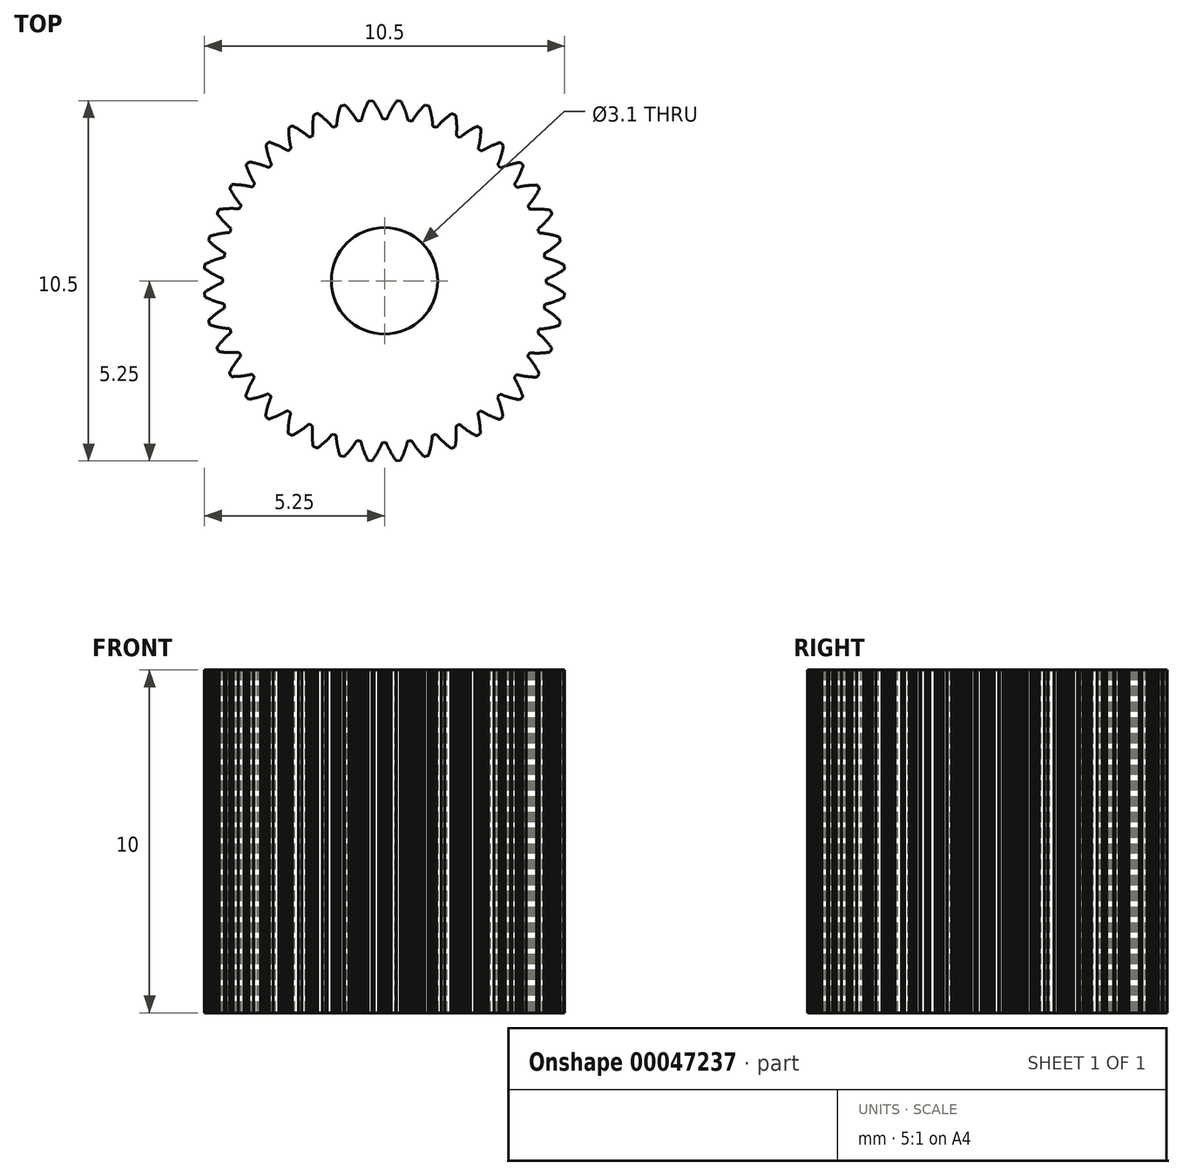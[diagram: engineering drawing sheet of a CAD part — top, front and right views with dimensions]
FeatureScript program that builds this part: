
annotation { "Feature Type Name" : "Feature", "Feature Type Description" : "" }
export const myFeature = defineFeature(function(context is Context, id is Id, definition is map)
    precondition{}
    {
        {
            var Q0;
            Q0=qCreatedBy(makeId("Top.planeOp"),FACE);
            var sketch = newSketch(context, id + "F0", { "sketchPlane" : qUnion([Q0])});
            skLineSegment(sketch, "E0", {"start": v(-0.35, 5.25) * mm, "end": v(-0.46, 5.24) * mm});
            skLineSegment(sketch, "E1", {"start": v(-0.46, 5.24) * mm, "end": v(-0.47, 5.23) * mm});
            skLineSegment(sketch, "E2", {"start": v(-0.47, 5.23) * mm, "end": v(-0.49, 5.2) * mm});
            skLineSegment(sketch, "E3", {"start": v(-0.49, 5.2) * mm, "end": v(-0.5, 5.18) * mm});
            skLineSegment(sketch, "E4", {"start": v(-0.5, 5.18) * mm, "end": v(-0.5, 5.16) * mm});
            skLineSegment(sketch, "E5", {"start": v(-0.5, 5.16) * mm, "end": v(-0.52, 5.14) * mm});
            skLineSegment(sketch, "E6", {"start": v(-0.52, 5.14) * mm, "end": v(-0.52, 5.12) * mm});
            skLineSegment(sketch, "E7", {"start": v(-0.52, 5.12) * mm, "end": v(-0.53, 5.1) * mm});
            skLineSegment(sketch, "E8", {"start": v(-0.53, 5.1) * mm, "end": v(-0.54, 5.08) * mm});
            skLineSegment(sketch, "E9", {"start": v(-0.54, 5.08) * mm, "end": v(-0.55, 5.06) * mm});
            skLineSegment(sketch, "E10", {"start": v(-0.55, 5.06) * mm, "end": v(-0.56, 5.04) * mm});
            skLineSegment(sketch, "E11", {"start": v(-0.56, 5.04) * mm, "end": v(-0.57, 5.02) * mm});
            skLineSegment(sketch, "E12", {"start": v(-0.57, 5.02) * mm, "end": v(-0.57, 5) * mm});
            skLineSegment(sketch, "E13", {"start": v(-0.57, 5) * mm, "end": v(-0.58, 4.98) * mm});
            skLineSegment(sketch, "E14", {"start": v(-0.58, 4.98) * mm, "end": v(-0.59, 4.96) * mm});
            skLineSegment(sketch, "E15", {"start": v(-0.59, 4.96) * mm, "end": v(-0.6, 4.94) * mm});
            skLineSegment(sketch, "E16", {"start": v(-0.6, 4.94) * mm, "end": v(-0.6, 4.93) * mm});
            skLineSegment(sketch, "E17", {"start": v(-0.6, 4.93) * mm, "end": v(-0.6, 4.9) * mm});
            skLineSegment(sketch, "E18", {"start": v(-0.6, 4.9) * mm, "end": v(-0.61, 4.9) * mm});
            skLineSegment(sketch, "E19", {"start": v(-0.61, 4.9) * mm, "end": v(-0.62, 4.87) * mm});
            skLineSegment(sketch, "E20", {"start": v(-0.62, 4.87) * mm, "end": v(-0.62, 4.86) * mm});
            skLineSegment(sketch, "E21", {"start": v(-0.62, 4.86) * mm, "end": v(-0.63, 4.84) * mm});
            skLineSegment(sketch, "E22", {"start": v(-0.63, 4.84) * mm, "end": v(-0.63, 4.82) * mm});
            skLineSegment(sketch, "E23", {"start": v(-0.63, 4.82) * mm, "end": v(-0.64, 4.8) * mm});
            skLineSegment(sketch, "E24", {"start": v(-0.64, 4.8) * mm, "end": v(-0.64, 4.8) * mm});
            skLineSegment(sketch, "E25", {"start": v(-0.64, 4.8) * mm, "end": v(-0.65, 4.78) * mm});
            skLineSegment(sketch, "E26", {"start": v(-0.65, 4.78) * mm, "end": v(-0.65, 4.76) * mm});
            skLineSegment(sketch, "E27", {"start": v(-0.65, 4.76) * mm, "end": v(-0.66, 4.74) * mm});
            skLineSegment(sketch, "E28", {"start": v(-0.66, 4.74) * mm, "end": v(-0.66, 4.73) * mm});
            skLineSegment(sketch, "E29", {"start": v(-0.66, 4.73) * mm, "end": v(-0.66, 4.72) * mm});
            skLineSegment(sketch, "E30", {"start": v(-0.66, 4.72) * mm, "end": v(-0.67, 4.7) * mm});
            skLineSegment(sketch, "E31", {"start": v(-0.67, 4.7) * mm, "end": v(-0.67, 4.69) * mm});
            skLineSegment(sketch, "E32", {"start": v(-0.67, 4.69) * mm, "end": v(-0.67, 4.68) * mm});
            skLineSegment(sketch, "E33", {"start": v(-0.67, 4.68) * mm, "end": v(-0.72, 4.67) * mm});
            skLineSegment(sketch, "E34", {"start": v(-0.72, 4.67) * mm, "end": v(-0.74, 4.66) * mm});
            skLineSegment(sketch, "E35", {"start": v(-0.74, 4.66) * mm, "end": v(-0.8, 4.66) * mm});
            skLineSegment(sketch, "E36", {"start": v(-0.8, 4.66) * mm, "end": v(-0.8, 4.67) * mm});
            skLineSegment(sketch, "E37", {"start": v(-0.8, 4.67) * mm, "end": v(-0.8, 4.68) * mm});
            skLineSegment(sketch, "E38", {"start": v(-0.8, 4.68) * mm, "end": v(-0.81, 4.7) * mm});
            skLineSegment(sketch, "E39", {"start": v(-0.81, 4.7) * mm, "end": v(-0.82, 4.7) * mm});
            skLineSegment(sketch, "E40", {"start": v(-0.82, 4.7) * mm, "end": v(-0.83, 4.72) * mm});
            skLineSegment(sketch, "E41", {"start": v(-0.83, 4.72) * mm, "end": v(-0.84, 4.73) * mm});
            skLineSegment(sketch, "E42", {"start": v(-0.84, 4.73) * mm, "end": v(-0.85, 4.74) * mm});
            skLineSegment(sketch, "E43", {"start": v(-0.85, 4.74) * mm, "end": v(-0.85, 4.76) * mm});
            skLineSegment(sketch, "E44", {"start": v(-0.85, 4.76) * mm, "end": v(-0.86, 4.77) * mm});
            skLineSegment(sketch, "E45", {"start": v(-0.86, 4.77) * mm, "end": v(-0.87, 4.79) * mm});
            skLineSegment(sketch, "E46", {"start": v(-0.87, 4.79) * mm, "end": v(-0.88, 4.8) * mm});
            skLineSegment(sketch, "E47", {"start": v(-0.88, 4.8) * mm, "end": v(-0.9, 4.81) * mm});
            skLineSegment(sketch, "E48", {"start": v(-0.9, 4.81) * mm, "end": v(-0.9, 4.83) * mm});
            skLineSegment(sketch, "E49", {"start": v(-0.9, 4.83) * mm, "end": v(-0.91, 4.84) * mm});
            skLineSegment(sketch, "E50", {"start": v(-0.91, 4.84) * mm, "end": v(-0.92, 4.86) * mm});
            skLineSegment(sketch, "E51", {"start": v(-0.92, 4.86) * mm, "end": v(-0.94, 4.87) * mm});
            skLineSegment(sketch, "E52", {"start": v(-0.94, 4.87) * mm, "end": v(-0.95, 4.89) * mm});
            skLineSegment(sketch, "E53", {"start": v(-0.95, 4.89) * mm, "end": v(-0.96, 4.9) * mm});
            skLineSegment(sketch, "E54", {"start": v(-0.96, 4.9) * mm, "end": v(-0.97, 4.92) * mm});
            skLineSegment(sketch, "E55", {"start": v(-0.97, 4.92) * mm, "end": v(-0.98, 4.94) * mm});
            skLineSegment(sketch, "E56", {"start": v(-0.98, 4.94) * mm, "end": v(-1, 4.95) * mm});
            skLineSegment(sketch, "E57", {"start": v(-1, 4.95) * mm, "end": v(-1.01, 4.97) * mm});
            skLineSegment(sketch, "E58", {"start": v(-1.01, 4.97) * mm, "end": v(-1.02, 4.98) * mm});
            skLineSegment(sketch, "E59", {"start": v(-1.02, 4.98) * mm, "end": v(-1.04, 5) * mm});
            skLineSegment(sketch, "E60", {"start": v(-1.04, 5) * mm, "end": v(-1.05, 5.02) * mm});
            skLineSegment(sketch, "E61", {"start": v(-1.05, 5.02) * mm, "end": v(-1.07, 5.03) * mm});
            skLineSegment(sketch, "E62", {"start": v(-1.07, 5.03) * mm, "end": v(-1.08, 5.05) * mm});
            skLineSegment(sketch, "E63", {"start": v(-1.08, 5.05) * mm, "end": v(-1.1, 5.07) * mm});
            skLineSegment(sketch, "E64", {"start": v(-1.1, 5.07) * mm, "end": v(-1.11, 5.08) * mm});
            skLineSegment(sketch, "E65", {"start": v(-1.11, 5.08) * mm, "end": v(-1.13, 5.1) * mm});
            skLineSegment(sketch, "E66", {"start": v(-1.13, 5.1) * mm, "end": v(-1.15, 5.12) * mm});
            skLineSegment(sketch, "E67", {"start": v(-1.15, 5.12) * mm, "end": v(-1.17, 5.13) * mm});
            skLineSegment(sketch, "E68", {"start": v(-1.17, 5.13) * mm, "end": v(-1.27, 5.1) * mm});
            skLineSegment(sketch, "E69", {"start": v(-1.27, 5.1) * mm, "end": v(-1.29, 5.09) * mm});
            skLineSegment(sketch, "E70", {"start": v(-1.29, 5.09) * mm, "end": v(-1.3, 5.06) * mm});
            skLineSegment(sketch, "E71", {"start": v(-1.3, 5.06) * mm, "end": v(-1.3, 5.04) * mm});
            skLineSegment(sketch, "E72", {"start": v(-1.3, 5.04) * mm, "end": v(-1.3, 5.02) * mm});
            skLineSegment(sketch, "E73", {"start": v(-1.3, 5.02) * mm, "end": v(-1.31, 5) * mm});
            skLineSegment(sketch, "E74", {"start": v(-1.31, 5) * mm, "end": v(-1.32, 4.97) * mm});
            skLineSegment(sketch, "E75", {"start": v(-1.32, 4.97) * mm, "end": v(-1.33, 4.95) * mm});
            skLineSegment(sketch, "E76", {"start": v(-1.33, 4.95) * mm, "end": v(-1.33, 4.93) * mm});
            skLineSegment(sketch, "E77", {"start": v(-1.33, 4.93) * mm, "end": v(-1.34, 4.91) * mm});
            skLineSegment(sketch, "E78", {"start": v(-1.34, 4.91) * mm, "end": v(-1.34, 4.89) * mm});
            skLineSegment(sketch, "E79", {"start": v(-1.34, 4.89) * mm, "end": v(-1.35, 4.87) * mm});
            skLineSegment(sketch, "E80", {"start": v(-1.35, 4.87) * mm, "end": v(-1.35, 4.85) * mm});
            skLineSegment(sketch, "E81", {"start": v(-1.35, 4.85) * mm, "end": v(-1.35, 4.83) * mm});
            skLineSegment(sketch, "E82", {"start": v(-1.35, 4.83) * mm, "end": v(-1.36, 4.8) * mm});
            skLineSegment(sketch, "E83", {"start": v(-1.36, 4.8) * mm, "end": v(-1.36, 4.8) * mm});
            skLineSegment(sketch, "E84", {"start": v(-1.36, 4.8) * mm, "end": v(-1.37, 4.77) * mm});
            skLineSegment(sketch, "E85", {"start": v(-1.37, 4.77) * mm, "end": v(-1.37, 4.75) * mm});
            skLineSegment(sketch, "E86", {"start": v(-1.37, 4.75) * mm, "end": v(-1.37, 4.73) * mm});
            skLineSegment(sketch, "E87", {"start": v(-1.37, 4.73) * mm, "end": v(-1.37, 4.72) * mm});
            skLineSegment(sketch, "E88", {"start": v(-1.37, 4.72) * mm, "end": v(-1.38, 4.7) * mm});
            skLineSegment(sketch, "E89", {"start": v(-1.38, 4.7) * mm, "end": v(-1.38, 4.68) * mm});
            skLineSegment(sketch, "E90", {"start": v(-1.38, 4.68) * mm, "end": v(-1.38, 4.66) * mm});
            skLineSegment(sketch, "E91", {"start": v(-1.38, 4.66) * mm, "end": v(-1.38, 4.65) * mm});
            skLineSegment(sketch, "E92", {"start": v(-1.38, 4.65) * mm, "end": v(-1.39, 4.63) * mm});
            skLineSegment(sketch, "E93", {"start": v(-1.39, 4.63) * mm, "end": v(-1.39, 4.62) * mm});
            skLineSegment(sketch, "E94", {"start": v(-1.39, 4.62) * mm, "end": v(-1.39, 4.6) * mm});
            skLineSegment(sketch, "E95", {"start": v(-1.39, 4.6) * mm, "end": v(-1.4, 4.58) * mm});
            skLineSegment(sketch, "E96", {"start": v(-1.4, 4.58) * mm, "end": v(-1.4, 4.57) * mm});
            skLineSegment(sketch, "E97", {"start": v(-1.4, 4.57) * mm, "end": v(-1.4, 4.55) * mm});
            skLineSegment(sketch, "E98", {"start": v(-1.4, 4.55) * mm, "end": v(-1.4, 4.54) * mm});
            skLineSegment(sketch, "E99", {"start": v(-1.4, 4.54) * mm, "end": v(-1.4, 4.53) * mm});
            skLineSegment(sketch, "E100", {"start": v(-1.4, 4.53) * mm, "end": v(-1.4, 4.52) * mm});
            skLineSegment(sketch, "E101", {"start": v(-1.4, 4.52) * mm, "end": v(-1.45, 4.5) * mm});
            skLineSegment(sketch, "E102", {"start": v(-1.45, 4.5) * mm, "end": v(-1.46, 4.5) * mm});
            skLineSegment(sketch, "E103", {"start": v(-1.46, 4.5) * mm, "end": v(-1.51, 4.48) * mm});
            skLineSegment(sketch, "E104", {"start": v(-1.51, 4.48) * mm, "end": v(-1.52, 4.49) * mm});
            skLineSegment(sketch, "E105", {"start": v(-1.52, 4.49) * mm, "end": v(-1.53, 4.5) * mm});
            skLineSegment(sketch, "E106", {"start": v(-1.53, 4.5) * mm, "end": v(-1.54, 4.5) * mm});
            skLineSegment(sketch, "E107", {"start": v(-1.54, 4.5) * mm, "end": v(-1.55, 4.52) * mm});
            skLineSegment(sketch, "E108", {"start": v(-1.55, 4.52) * mm, "end": v(-1.56, 4.53) * mm});
            skLineSegment(sketch, "E109", {"start": v(-1.56, 4.53) * mm, "end": v(-1.57, 4.54) * mm});
            skLineSegment(sketch, "E110", {"start": v(-1.57, 4.54) * mm, "end": v(-1.58, 4.55) * mm});
            skLineSegment(sketch, "E111", {"start": v(-1.58, 4.55) * mm, "end": v(-1.59, 4.57) * mm});
            skLineSegment(sketch, "E112", {"start": v(-1.59, 4.57) * mm, "end": v(-1.6, 4.58) * mm});
            skLineSegment(sketch, "E113", {"start": v(-1.6, 4.58) * mm, "end": v(-1.61, 4.6) * mm});
            skLineSegment(sketch, "E114", {"start": v(-1.61, 4.6) * mm, "end": v(-1.62, 4.6) * mm});
            skLineSegment(sketch, "E115", {"start": v(-1.62, 4.6) * mm, "end": v(-1.63, 4.62) * mm});
            skLineSegment(sketch, "E116", {"start": v(-1.63, 4.62) * mm, "end": v(-1.65, 4.63) * mm});
            skLineSegment(sketch, "E117", {"start": v(-1.65, 4.63) * mm, "end": v(-1.66, 4.64) * mm});
            skLineSegment(sketch, "E118", {"start": v(-1.66, 4.64) * mm, "end": v(-1.67, 4.65) * mm});
            skLineSegment(sketch, "E119", {"start": v(-1.67, 4.65) * mm, "end": v(-1.69, 4.67) * mm});
            skLineSegment(sketch, "E120", {"start": v(-1.69, 4.67) * mm, "end": v(-1.7, 4.68) * mm});
            skLineSegment(sketch, "E121", {"start": v(-1.7, 4.68) * mm, "end": v(-1.71, 4.7) * mm});
            skLineSegment(sketch, "E122", {"start": v(-1.71, 4.7) * mm, "end": v(-1.73, 4.7) * mm});
            skLineSegment(sketch, "E123", {"start": v(-1.73, 4.7) * mm, "end": v(-1.74, 4.72) * mm});
            skLineSegment(sketch, "E124", {"start": v(-1.74, 4.72) * mm, "end": v(-1.76, 4.74) * mm});
            skLineSegment(sketch, "E125", {"start": v(-1.76, 4.74) * mm, "end": v(-1.78, 4.75) * mm});
            skLineSegment(sketch, "E126", {"start": v(-1.78, 4.75) * mm, "end": v(-1.8, 4.76) * mm});
            skLineSegment(sketch, "E127", {"start": v(-1.8, 4.76) * mm, "end": v(-1.8, 4.78) * mm});
            skLineSegment(sketch, "E128", {"start": v(-1.8, 4.78) * mm, "end": v(-1.82, 4.8) * mm});
            skLineSegment(sketch, "E129", {"start": v(-1.82, 4.8) * mm, "end": v(-1.84, 4.8) * mm});
            skLineSegment(sketch, "E130", {"start": v(-1.84, 4.8) * mm, "end": v(-1.86, 4.82) * mm});
            skLineSegment(sketch, "E131", {"start": v(-1.86, 4.82) * mm, "end": v(-1.88, 4.83) * mm});
            skLineSegment(sketch, "E132", {"start": v(-1.88, 4.83) * mm, "end": v(-1.9, 4.85) * mm});
            skLineSegment(sketch, "E133", {"start": v(-1.9, 4.85) * mm, "end": v(-1.91, 4.86) * mm});
            skLineSegment(sketch, "E134", {"start": v(-1.91, 4.86) * mm, "end": v(-1.94, 4.88) * mm});
            skLineSegment(sketch, "E135", {"start": v(-1.94, 4.88) * mm, "end": v(-1.96, 4.88) * mm});
            skLineSegment(sketch, "E136", {"start": v(-1.96, 4.88) * mm, "end": v(-2.05, 4.84) * mm});
            skLineSegment(sketch, "E137", {"start": v(-2.05, 4.84) * mm, "end": v(-2.07, 4.82) * mm});
            skLineSegment(sketch, "E138", {"start": v(-2.07, 4.82) * mm, "end": v(-2.07, 4.8) * mm});
            skLineSegment(sketch, "E139", {"start": v(-2.07, 4.8) * mm, "end": v(-2.07, 4.78) * mm});
            skLineSegment(sketch, "E140", {"start": v(-2.07, 4.78) * mm, "end": v(-2.08, 4.75) * mm});
            skLineSegment(sketch, "E141", {"start": v(-2.08, 4.75) * mm, "end": v(-2.08, 4.73) * mm});
            skLineSegment(sketch, "E142", {"start": v(-2.08, 4.73) * mm, "end": v(-2.08, 4.7) * mm});
            skLineSegment(sketch, "E143", {"start": v(-2.08, 4.7) * mm, "end": v(-2.08, 4.68) * mm});
            skLineSegment(sketch, "E144", {"start": v(-2.08, 4.68) * mm, "end": v(-2.09, 4.66) * mm});
            skLineSegment(sketch, "E145", {"start": v(-2.09, 4.66) * mm, "end": v(-2.09, 4.64) * mm});
            skLineSegment(sketch, "E146", {"start": v(-2.09, 4.64) * mm, "end": v(-2.09, 4.62) * mm});
            skLineSegment(sketch, "E147", {"start": v(-2.09, 4.62) * mm, "end": v(-2.1, 4.6) * mm});
            skLineSegment(sketch, "E148", {"start": v(-2.1, 4.6) * mm, "end": v(-2.1, 4.58) * mm});
            skLineSegment(sketch, "E149", {"start": v(-2.1, 4.58) * mm, "end": v(-2.1, 4.56) * mm});
            skLineSegment(sketch, "E150", {"start": v(-2.1, 4.56) * mm, "end": v(-2.1, 4.54) * mm});
            skLineSegment(sketch, "E151", {"start": v(-2.1, 4.54) * mm, "end": v(-2.1, 4.52) * mm});
            skLineSegment(sketch, "E152", {"start": v(-2.1, 4.52) * mm, "end": v(-2.1, 4.5) * mm});
            skLineSegment(sketch, "E153", {"start": v(-2.1, 4.5) * mm, "end": v(-2.1, 4.48) * mm});
            skLineSegment(sketch, "E154", {"start": v(-2.1, 4.48) * mm, "end": v(-2.1, 4.46) * mm});
            skLineSegment(sketch, "E155", {"start": v(-2.1, 4.46) * mm, "end": v(-2.1, 4.44) * mm});
            skLineSegment(sketch, "E156", {"start": v(-2.1, 4.44) * mm, "end": v(-2.1, 4.43) * mm});
            skLineSegment(sketch, "E157", {"start": v(-2.1, 4.43) * mm, "end": v(-2.1, 4.4) * mm});
            skLineSegment(sketch, "E158", {"start": v(-2.1, 4.4) * mm, "end": v(-2.1, 4.4) * mm});
            skLineSegment(sketch, "E159", {"start": v(-2.1, 4.4) * mm, "end": v(-2.1, 4.37) * mm});
            skLineSegment(sketch, "E160", {"start": v(-2.1, 4.37) * mm, "end": v(-2.1, 4.36) * mm});
            skLineSegment(sketch, "E161", {"start": v(-2.1, 4.36) * mm, "end": v(-2.1, 4.34) * mm});
            skLineSegment(sketch, "E162", {"start": v(-2.1, 4.34) * mm, "end": v(-2.1, 4.33) * mm});
            skLineSegment(sketch, "E163", {"start": v(-2.1, 4.33) * mm, "end": v(-2.1, 4.31) * mm});
            skLineSegment(sketch, "E164", {"start": v(-2.1, 4.31) * mm, "end": v(-2.09, 4.3) * mm});
            skLineSegment(sketch, "E165", {"start": v(-2.09, 4.3) * mm, "end": v(-2.09, 4.28) * mm});
            skLineSegment(sketch, "E166", {"start": v(-2.09, 4.28) * mm, "end": v(-2.09, 4.27) * mm});
            skLineSegment(sketch, "E167", {"start": v(-2.09, 4.27) * mm, "end": v(-2.08, 4.25) * mm});
            skLineSegment(sketch, "E168", {"start": v(-2.08, 4.25) * mm, "end": v(-2.08, 4.24) * mm});
            skLineSegment(sketch, "E169", {"start": v(-2.08, 4.24) * mm, "end": v(-2.13, 4.21) * mm});
            skLineSegment(sketch, "E170", {"start": v(-2.13, 4.21) * mm, "end": v(-2.14, 4.2) * mm});
            skLineSegment(sketch, "E171", {"start": v(-2.14, 4.2) * mm, "end": v(-2.2, 4.19) * mm});
            skLineSegment(sketch, "E172", {"start": v(-2.2, 4.19) * mm, "end": v(-2.2, 4.2) * mm});
            skLineSegment(sketch, "E173", {"start": v(-2.2, 4.2) * mm, "end": v(-2.21, 4.2) * mm});
            skLineSegment(sketch, "E174", {"start": v(-2.21, 4.2) * mm, "end": v(-2.22, 4.21) * mm});
            skLineSegment(sketch, "E175", {"start": v(-2.22, 4.21) * mm, "end": v(-2.23, 4.22) * mm});
            skLineSegment(sketch, "E176", {"start": v(-2.23, 4.22) * mm, "end": v(-2.25, 4.23) * mm});
            skLineSegment(sketch, "E177", {"start": v(-2.25, 4.23) * mm, "end": v(-2.26, 4.24) * mm});
            skLineSegment(sketch, "E178", {"start": v(-2.26, 4.24) * mm, "end": v(-2.27, 4.25) * mm});
            skLineSegment(sketch, "E179", {"start": v(-2.27, 4.25) * mm, "end": v(-2.28, 4.26) * mm});
            skLineSegment(sketch, "E180", {"start": v(-2.28, 4.26) * mm, "end": v(-2.3, 4.27) * mm});
            skLineSegment(sketch, "E181", {"start": v(-2.3, 4.27) * mm, "end": v(-2.3, 4.28) * mm});
            skLineSegment(sketch, "E182", {"start": v(-2.3, 4.28) * mm, "end": v(-2.32, 4.3) * mm});
            skLineSegment(sketch, "E183", {"start": v(-2.32, 4.3) * mm, "end": v(-2.34, 4.3) * mm});
            skLineSegment(sketch, "E184", {"start": v(-2.34, 4.3) * mm, "end": v(-2.35, 4.31) * mm});
            skLineSegment(sketch, "E185", {"start": v(-2.35, 4.31) * mm, "end": v(-2.37, 4.33) * mm});
            skLineSegment(sketch, "E186", {"start": v(-2.37, 4.33) * mm, "end": v(-2.38, 4.34) * mm});
            skLineSegment(sketch, "E187", {"start": v(-2.38, 4.34) * mm, "end": v(-2.4, 4.35) * mm});
            skLineSegment(sketch, "E188", {"start": v(-2.4, 4.35) * mm, "end": v(-2.41, 4.36) * mm});
            skLineSegment(sketch, "E189", {"start": v(-2.41, 4.36) * mm, "end": v(-2.43, 4.37) * mm});
            skLineSegment(sketch, "E190", {"start": v(-2.43, 4.37) * mm, "end": v(-2.44, 4.38) * mm});
            skLineSegment(sketch, "E191", {"start": v(-2.44, 4.38) * mm, "end": v(-2.46, 4.4) * mm});
            skLineSegment(sketch, "E192", {"start": v(-2.46, 4.4) * mm, "end": v(-2.48, 4.4) * mm});
            skLineSegment(sketch, "E193", {"start": v(-2.48, 4.4) * mm, "end": v(-2.5, 4.41) * mm});
            skLineSegment(sketch, "E194", {"start": v(-2.5, 4.41) * mm, "end": v(-2.51, 4.42) * mm});
            skLineSegment(sketch, "E195", {"start": v(-2.51, 4.42) * mm, "end": v(-2.53, 4.44) * mm});
            skLineSegment(sketch, "E196", {"start": v(-2.53, 4.44) * mm, "end": v(-2.55, 4.45) * mm});
            skLineSegment(sketch, "E197", {"start": v(-2.55, 4.45) * mm, "end": v(-2.57, 4.46) * mm});
            skLineSegment(sketch, "E198", {"start": v(-2.57, 4.46) * mm, "end": v(-2.6, 4.47) * mm});
            skLineSegment(sketch, "E199", {"start": v(-2.6, 4.47) * mm, "end": v(-2.61, 4.48) * mm});
            skLineSegment(sketch, "E200", {"start": v(-2.61, 4.48) * mm, "end": v(-2.63, 4.5) * mm});
            skLineSegment(sketch, "E201", {"start": v(-2.63, 4.5) * mm, "end": v(-2.65, 4.5) * mm});
            skLineSegment(sketch, "E202", {"start": v(-2.65, 4.5) * mm, "end": v(-2.68, 4.52) * mm});
            skLineSegment(sketch, "E203", {"start": v(-2.68, 4.52) * mm, "end": v(-2.7, 4.52) * mm});
            skLineSegment(sketch, "E204", {"start": v(-2.7, 4.52) * mm, "end": v(-2.79, 4.46) * mm});
            skLineSegment(sketch, "E205", {"start": v(-2.79, 4.46) * mm, "end": v(-2.8, 4.44) * mm});
            skLineSegment(sketch, "E206", {"start": v(-2.8, 4.44) * mm, "end": v(-2.8, 4.42) * mm});
            skLineSegment(sketch, "E207", {"start": v(-2.8, 4.42) * mm, "end": v(-2.8, 4.4) * mm});
            skLineSegment(sketch, "E208", {"start": v(-2.8, 4.4) * mm, "end": v(-2.8, 4.37) * mm});
            skLineSegment(sketch, "E209", {"start": v(-2.8, 4.37) * mm, "end": v(-2.8, 4.35) * mm});
            skLineSegment(sketch, "E210", {"start": v(-2.8, 4.35) * mm, "end": v(-2.8, 4.32) * mm});
            skLineSegment(sketch, "E211", {"start": v(-2.8, 4.32) * mm, "end": v(-2.8, 4.3) * mm});
            skLineSegment(sketch, "E212", {"start": v(-2.8, 4.3) * mm, "end": v(-2.79, 4.28) * mm});
            skLineSegment(sketch, "E213", {"start": v(-2.79, 4.28) * mm, "end": v(-2.79, 4.26) * mm});
            skLineSegment(sketch, "E214", {"start": v(-2.79, 4.26) * mm, "end": v(-2.79, 4.24) * mm});
            skLineSegment(sketch, "E215", {"start": v(-2.79, 4.24) * mm, "end": v(-2.78, 4.22) * mm});
            skLineSegment(sketch, "E216", {"start": v(-2.78, 4.22) * mm, "end": v(-2.78, 4.2) * mm});
            skLineSegment(sketch, "E217", {"start": v(-2.78, 4.2) * mm, "end": v(-2.78, 4.17) * mm});
            skLineSegment(sketch, "E218", {"start": v(-2.78, 4.17) * mm, "end": v(-2.78, 4.16) * mm});
            skLineSegment(sketch, "E219", {"start": v(-2.78, 4.16) * mm, "end": v(-2.78, 4.14) * mm});
            skLineSegment(sketch, "E220", {"start": v(-2.78, 4.14) * mm, "end": v(-2.77, 4.12) * mm});
            skLineSegment(sketch, "E221", {"start": v(-2.77, 4.12) * mm, "end": v(-2.77, 4.1) * mm});
            skLineSegment(sketch, "E222", {"start": v(-2.77, 4.1) * mm, "end": v(-2.77, 4.08) * mm});
            skLineSegment(sketch, "E223", {"start": v(-2.77, 4.08) * mm, "end": v(-2.76, 4.06) * mm});
            skLineSegment(sketch, "E224", {"start": v(-2.76, 4.06) * mm, "end": v(-2.76, 4.04) * mm});
            skLineSegment(sketch, "E225", {"start": v(-2.76, 4.04) * mm, "end": v(-2.76, 4.03) * mm});
            skLineSegment(sketch, "E226", {"start": v(-2.76, 4.03) * mm, "end": v(-2.76, 4) * mm});
            skLineSegment(sketch, "E227", {"start": v(-2.76, 4) * mm, "end": v(-2.75, 4) * mm});
            skLineSegment(sketch, "E228", {"start": v(-2.75, 4) * mm, "end": v(-2.75, 3.98) * mm});
            skLineSegment(sketch, "E229", {"start": v(-2.75, 3.98) * mm, "end": v(-2.75, 3.96) * mm});
            skLineSegment(sketch, "E230", {"start": v(-2.75, 3.96) * mm, "end": v(-2.74, 3.95) * mm});
            skLineSegment(sketch, "E231", {"start": v(-2.74, 3.95) * mm, "end": v(-2.74, 3.93) * mm});
            skLineSegment(sketch, "E232", {"start": v(-2.74, 3.93) * mm, "end": v(-2.73, 3.92) * mm});
            skLineSegment(sketch, "E233", {"start": v(-2.73, 3.92) * mm, "end": v(-2.73, 3.9) * mm});
            skLineSegment(sketch, "E234", {"start": v(-2.73, 3.9) * mm, "end": v(-2.73, 3.89) * mm});
            skLineSegment(sketch, "E235", {"start": v(-2.73, 3.89) * mm, "end": v(-2.72, 3.87) * mm});
            skLineSegment(sketch, "E236", {"start": v(-2.72, 3.87) * mm, "end": v(-2.72, 3.87) * mm});
            skLineSegment(sketch, "E237", {"start": v(-2.72, 3.87) * mm, "end": v(-2.76, 3.83) * mm});
            skLineSegment(sketch, "E238", {"start": v(-2.76, 3.83) * mm, "end": v(-2.78, 3.82) * mm});
            skLineSegment(sketch, "E239", {"start": v(-2.78, 3.82) * mm, "end": v(-2.82, 3.8) * mm});
            skLineSegment(sketch, "E240", {"start": v(-2.82, 3.8) * mm, "end": v(-2.83, 3.8) * mm});
            skLineSegment(sketch, "E241", {"start": v(-2.83, 3.8) * mm, "end": v(-2.84, 3.8) * mm});
            skLineSegment(sketch, "E242", {"start": v(-2.84, 3.8) * mm, "end": v(-2.85, 3.81) * mm});
            skLineSegment(sketch, "E243", {"start": v(-2.85, 3.81) * mm, "end": v(-2.87, 3.82) * mm});
            skLineSegment(sketch, "E244", {"start": v(-2.87, 3.82) * mm, "end": v(-2.88, 3.83) * mm});
            skLineSegment(sketch, "E245", {"start": v(-2.88, 3.83) * mm, "end": v(-2.9, 3.84) * mm});
            skLineSegment(sketch, "E246", {"start": v(-2.9, 3.84) * mm, "end": v(-2.9, 3.84) * mm});
            skLineSegment(sketch, "E247", {"start": v(-2.9, 3.84) * mm, "end": v(-2.92, 3.85) * mm});
            skLineSegment(sketch, "E248", {"start": v(-2.92, 3.85) * mm, "end": v(-2.94, 3.86) * mm});
            skLineSegment(sketch, "E249", {"start": v(-2.94, 3.86) * mm, "end": v(-2.95, 3.87) * mm});
            skLineSegment(sketch, "E250", {"start": v(-2.95, 3.87) * mm, "end": v(-2.97, 3.88) * mm});
            skLineSegment(sketch, "E251", {"start": v(-2.97, 3.88) * mm, "end": v(-2.98, 3.89) * mm});
            skLineSegment(sketch, "E252", {"start": v(-2.98, 3.89) * mm, "end": v(-3, 3.9) * mm});
            skLineSegment(sketch, "E253", {"start": v(-3, 3.9) * mm, "end": v(-3.01, 3.9) * mm});
            skLineSegment(sketch, "E254", {"start": v(-3.01, 3.9) * mm, "end": v(-3.03, 3.91) * mm});
            skLineSegment(sketch, "E255", {"start": v(-3.03, 3.91) * mm, "end": v(-3.05, 3.92) * mm});
            skLineSegment(sketch, "E256", {"start": v(-3.05, 3.92) * mm, "end": v(-3.06, 3.93) * mm});
            skLineSegment(sketch, "E257", {"start": v(-3.06, 3.93) * mm, "end": v(-3.08, 3.94) * mm});
            skLineSegment(sketch, "E258", {"start": v(-3.08, 3.94) * mm, "end": v(-3.1, 3.94) * mm});
            skLineSegment(sketch, "E259", {"start": v(-3.1, 3.94) * mm, "end": v(-3.12, 3.95) * mm});
            skLineSegment(sketch, "E260", {"start": v(-3.12, 3.95) * mm, "end": v(-3.14, 3.96) * mm});
            skLineSegment(sketch, "E261", {"start": v(-3.14, 3.96) * mm, "end": v(-3.16, 3.97) * mm});
            skLineSegment(sketch, "E262", {"start": v(-3.16, 3.97) * mm, "end": v(-3.18, 3.98) * mm});
            skLineSegment(sketch, "E263", {"start": v(-3.18, 3.98) * mm, "end": v(-3.2, 3.99) * mm});
            skLineSegment(sketch, "E264", {"start": v(-3.2, 3.99) * mm, "end": v(-3.22, 4) * mm});
            skLineSegment(sketch, "E265", {"start": v(-3.22, 4) * mm, "end": v(-3.24, 4) * mm});
            skLineSegment(sketch, "E266", {"start": v(-3.24, 4) * mm, "end": v(-3.26, 4) * mm});
            skLineSegment(sketch, "E267", {"start": v(-3.26, 4) * mm, "end": v(-3.28, 4.02) * mm});
            skLineSegment(sketch, "E268", {"start": v(-3.28, 4.02) * mm, "end": v(-3.3, 4.03) * mm});
            skLineSegment(sketch, "E269", {"start": v(-3.3, 4.03) * mm, "end": v(-3.32, 4.03) * mm});
            skLineSegment(sketch, "E270", {"start": v(-3.32, 4.03) * mm, "end": v(-3.35, 4.04) * mm});
            skLineSegment(sketch, "E271", {"start": v(-3.35, 4.04) * mm, "end": v(-3.37, 4.04) * mm});
            skLineSegment(sketch, "E272", {"start": v(-3.37, 4.04) * mm, "end": v(-3.45, 3.97) * mm});
            skLineSegment(sketch, "E273", {"start": v(-3.45, 3.97) * mm, "end": v(-3.46, 3.95) * mm});
            skLineSegment(sketch, "E274", {"start": v(-3.46, 3.95) * mm, "end": v(-3.45, 3.92) * mm});
            skLineSegment(sketch, "E275", {"start": v(-3.45, 3.92) * mm, "end": v(-3.45, 3.9) * mm});
            skLineSegment(sketch, "E276", {"start": v(-3.45, 3.9) * mm, "end": v(-3.44, 3.88) * mm});
            skLineSegment(sketch, "E277", {"start": v(-3.44, 3.88) * mm, "end": v(-3.44, 3.86) * mm});
            skLineSegment(sketch, "E278", {"start": v(-3.44, 3.86) * mm, "end": v(-3.43, 3.83) * mm});
            skLineSegment(sketch, "E279", {"start": v(-3.43, 3.83) * mm, "end": v(-3.43, 3.81) * mm});
            skLineSegment(sketch, "E280", {"start": v(-3.43, 3.81) * mm, "end": v(-3.42, 3.8) * mm});
            skLineSegment(sketch, "E281", {"start": v(-3.42, 3.8) * mm, "end": v(-3.42, 3.77) * mm});
            skLineSegment(sketch, "E282", {"start": v(-3.42, 3.77) * mm, "end": v(-3.41, 3.75) * mm});
            skLineSegment(sketch, "E283", {"start": v(-3.41, 3.75) * mm, "end": v(-3.4, 3.73) * mm});
            skLineSegment(sketch, "E284", {"start": v(-3.4, 3.73) * mm, "end": v(-3.4, 3.7) * mm});
            skLineSegment(sketch, "E285", {"start": v(-3.4, 3.7) * mm, "end": v(-3.4, 3.69) * mm});
            skLineSegment(sketch, "E286", {"start": v(-3.4, 3.69) * mm, "end": v(-3.4, 3.67) * mm});
            skLineSegment(sketch, "E287", {"start": v(-3.4, 3.67) * mm, "end": v(-3.39, 3.65) * mm});
            skLineSegment(sketch, "E288", {"start": v(-3.39, 3.65) * mm, "end": v(-3.38, 3.63) * mm});
            skLineSegment(sketch, "E289", {"start": v(-3.38, 3.63) * mm, "end": v(-3.38, 3.61) * mm});
            skLineSegment(sketch, "E290", {"start": v(-3.38, 3.61) * mm, "end": v(-3.37, 3.6) * mm});
            skLineSegment(sketch, "E291", {"start": v(-3.37, 3.6) * mm, "end": v(-3.37, 3.58) * mm});
            skLineSegment(sketch, "E292", {"start": v(-3.37, 3.58) * mm, "end": v(-3.36, 3.56) * mm});
            skLineSegment(sketch, "E293", {"start": v(-3.36, 3.56) * mm, "end": v(-3.35, 3.55) * mm});
            skLineSegment(sketch, "E294", {"start": v(-3.35, 3.55) * mm, "end": v(-3.35, 3.53) * mm});
            skLineSegment(sketch, "E295", {"start": v(-3.35, 3.53) * mm, "end": v(-3.34, 3.51) * mm});
            skLineSegment(sketch, "E296", {"start": v(-3.34, 3.51) * mm, "end": v(-3.34, 3.5) * mm});
            skLineSegment(sketch, "E297", {"start": v(-3.34, 3.5) * mm, "end": v(-3.33, 3.48) * mm});
            skLineSegment(sketch, "E298", {"start": v(-3.33, 3.48) * mm, "end": v(-3.33, 3.47) * mm});
            skLineSegment(sketch, "E299", {"start": v(-3.33, 3.47) * mm, "end": v(-3.32, 3.45) * mm});
            skLineSegment(sketch, "E300", {"start": v(-3.32, 3.45) * mm, "end": v(-3.31, 3.44) * mm});
            skLineSegment(sketch, "E301", {"start": v(-3.31, 3.44) * mm, "end": v(-3.3, 3.43) * mm});
            skLineSegment(sketch, "E302", {"start": v(-3.3, 3.43) * mm, "end": v(-3.3, 3.41) * mm});
            skLineSegment(sketch, "E303", {"start": v(-3.3, 3.41) * mm, "end": v(-3.3, 3.4) * mm});
            skLineSegment(sketch, "E304", {"start": v(-3.3, 3.4) * mm, "end": v(-3.3, 3.4) * mm});
            skLineSegment(sketch, "E305", {"start": v(-3.3, 3.4) * mm, "end": v(-3.33, 3.35) * mm});
            skLineSegment(sketch, "E306", {"start": v(-3.33, 3.35) * mm, "end": v(-3.34, 3.34) * mm});
            skLineSegment(sketch, "E307", {"start": v(-3.34, 3.34) * mm, "end": v(-3.38, 3.3) * mm});
            skLineSegment(sketch, "E308", {"start": v(-3.38, 3.3) * mm, "end": v(-3.39, 3.3) * mm});
            skLineSegment(sketch, "E309", {"start": v(-3.39, 3.3) * mm, "end": v(-3.4, 3.31) * mm});
            skLineSegment(sketch, "E310", {"start": v(-3.4, 3.31) * mm, "end": v(-3.42, 3.32) * mm});
            skLineSegment(sketch, "E311", {"start": v(-3.42, 3.32) * mm, "end": v(-3.43, 3.32) * mm});
            skLineSegment(sketch, "E312", {"start": v(-3.43, 3.32) * mm, "end": v(-3.44, 3.33) * mm});
            skLineSegment(sketch, "E313", {"start": v(-3.44, 3.33) * mm, "end": v(-3.46, 3.34) * mm});
            skLineSegment(sketch, "E314", {"start": v(-3.46, 3.34) * mm, "end": v(-3.47, 3.34) * mm});
            skLineSegment(sketch, "E315", {"start": v(-3.47, 3.34) * mm, "end": v(-3.49, 3.35) * mm});
            skLineSegment(sketch, "E316", {"start": v(-3.49, 3.35) * mm, "end": v(-3.5, 3.35) * mm});
            skLineSegment(sketch, "E317", {"start": v(-3.5, 3.35) * mm, "end": v(-3.52, 3.36) * mm});
            skLineSegment(sketch, "E318", {"start": v(-3.52, 3.36) * mm, "end": v(-3.54, 3.37) * mm});
            skLineSegment(sketch, "E319", {"start": v(-3.54, 3.37) * mm, "end": v(-3.55, 3.37) * mm});
            skLineSegment(sketch, "E320", {"start": v(-3.55, 3.37) * mm, "end": v(-3.57, 3.38) * mm});
            skLineSegment(sketch, "E321", {"start": v(-3.57, 3.38) * mm, "end": v(-3.59, 3.38) * mm});
            skLineSegment(sketch, "E322", {"start": v(-3.59, 3.38) * mm, "end": v(-3.6, 3.39) * mm});
            skLineSegment(sketch, "E323", {"start": v(-3.6, 3.39) * mm, "end": v(-3.62, 3.4) * mm});
            skLineSegment(sketch, "E324", {"start": v(-3.62, 3.4) * mm, "end": v(-3.64, 3.4) * mm});
            skLineSegment(sketch, "E325", {"start": v(-3.64, 3.4) * mm, "end": v(-3.66, 3.4) * mm});
            skLineSegment(sketch, "E326", {"start": v(-3.66, 3.4) * mm, "end": v(-3.68, 3.41) * mm});
            skLineSegment(sketch, "E327", {"start": v(-3.68, 3.41) * mm, "end": v(-3.7, 3.42) * mm});
            skLineSegment(sketch, "E328", {"start": v(-3.7, 3.42) * mm, "end": v(-3.72, 3.42) * mm});
            skLineSegment(sketch, "E329", {"start": v(-3.72, 3.42) * mm, "end": v(-3.74, 3.43) * mm});
            skLineSegment(sketch, "E330", {"start": v(-3.74, 3.43) * mm, "end": v(-3.76, 3.43) * mm});
            skLineSegment(sketch, "E331", {"start": v(-3.76, 3.43) * mm, "end": v(-3.78, 3.44) * mm});
            skLineSegment(sketch, "E332", {"start": v(-3.78, 3.44) * mm, "end": v(-3.8, 3.44) * mm});
            skLineSegment(sketch, "E333", {"start": v(-3.8, 3.44) * mm, "end": v(-3.82, 3.45) * mm});
            skLineSegment(sketch, "E334", {"start": v(-3.82, 3.45) * mm, "end": v(-3.85, 3.45) * mm});
            skLineSegment(sketch, "E335", {"start": v(-3.85, 3.45) * mm, "end": v(-3.87, 3.45) * mm});
            skLineSegment(sketch, "E336", {"start": v(-3.87, 3.45) * mm, "end": v(-3.9, 3.46) * mm});
            skLineSegment(sketch, "E337", {"start": v(-3.9, 3.46) * mm, "end": v(-3.91, 3.46) * mm});
            skLineSegment(sketch, "E338", {"start": v(-3.91, 3.46) * mm, "end": v(-3.94, 3.47) * mm});
            skLineSegment(sketch, "E339", {"start": v(-3.94, 3.47) * mm, "end": v(-3.96, 3.46) * mm});
            skLineSegment(sketch, "E340", {"start": v(-3.96, 3.46) * mm, "end": v(-4.03, 3.38) * mm});
            skLineSegment(sketch, "E341", {"start": v(-4.03, 3.38) * mm, "end": v(-4.03, 3.36) * mm});
            skLineSegment(sketch, "E342", {"start": v(-4.03, 3.36) * mm, "end": v(-4.02, 3.34) * mm});
            skLineSegment(sketch, "E343", {"start": v(-4.02, 3.34) * mm, "end": v(-4.01, 3.31) * mm});
            skLineSegment(sketch, "E344", {"start": v(-4.01, 3.31) * mm, "end": v(-4, 3.3) * mm});
            skLineSegment(sketch, "E345", {"start": v(-4, 3.3) * mm, "end": v(-4, 3.27) * mm});
            skLineSegment(sketch, "E346", {"start": v(-4, 3.27) * mm, "end": v(-4, 3.25) * mm});
            skLineSegment(sketch, "E347", {"start": v(-4, 3.25) * mm, "end": v(-3.98, 3.23) * mm});
            skLineSegment(sketch, "E348", {"start": v(-3.98, 3.23) * mm, "end": v(-3.98, 3.2) * mm});
            skLineSegment(sketch, "E349", {"start": v(-3.98, 3.2) * mm, "end": v(-3.97, 3.19) * mm});
            skLineSegment(sketch, "E350", {"start": v(-3.97, 3.19) * mm, "end": v(-3.96, 3.17) * mm});
            skLineSegment(sketch, "E351", {"start": v(-3.96, 3.17) * mm, "end": v(-3.95, 3.15) * mm});
            skLineSegment(sketch, "E352", {"start": v(-3.95, 3.15) * mm, "end": v(-3.94, 3.13) * mm});
            skLineSegment(sketch, "E353", {"start": v(-3.94, 3.13) * mm, "end": v(-3.93, 3.11) * mm});
            skLineSegment(sketch, "E354", {"start": v(-3.93, 3.11) * mm, "end": v(-3.93, 3.1) * mm});
            skLineSegment(sketch, "E355", {"start": v(-3.93, 3.1) * mm, "end": v(-3.92, 3.08) * mm});
            skLineSegment(sketch, "E356", {"start": v(-3.92, 3.08) * mm, "end": v(-3.9, 3.06) * mm});
            skLineSegment(sketch, "E357", {"start": v(-3.9, 3.06) * mm, "end": v(-3.9, 3.04) * mm});
            skLineSegment(sketch, "E358", {"start": v(-3.9, 3.04) * mm, "end": v(-3.9, 3.02) * mm});
            skLineSegment(sketch, "E359", {"start": v(-3.9, 3.02) * mm, "end": v(-3.88, 3) * mm});
            skLineSegment(sketch, "E360", {"start": v(-3.88, 3) * mm, "end": v(-3.88, 3) * mm});
            skLineSegment(sketch, "E361", {"start": v(-3.88, 3) * mm, "end": v(-3.87, 2.98) * mm});
            skLineSegment(sketch, "E362", {"start": v(-3.87, 2.98) * mm, "end": v(-3.86, 2.96) * mm});
            skLineSegment(sketch, "E363", {"start": v(-3.86, 2.96) * mm, "end": v(-3.85, 2.95) * mm});
            skLineSegment(sketch, "E364", {"start": v(-3.85, 2.95) * mm, "end": v(-3.84, 2.93) * mm});
            skLineSegment(sketch, "E365", {"start": v(-3.84, 2.93) * mm, "end": v(-3.84, 2.92) * mm});
            skLineSegment(sketch, "E366", {"start": v(-3.84, 2.92) * mm, "end": v(-3.83, 2.9) * mm});
            skLineSegment(sketch, "E367", {"start": v(-3.83, 2.9) * mm, "end": v(-3.82, 2.9) * mm});
            skLineSegment(sketch, "E368", {"start": v(-3.82, 2.9) * mm, "end": v(-3.81, 2.88) * mm});
            skLineSegment(sketch, "E369", {"start": v(-3.81, 2.88) * mm, "end": v(-3.8, 2.87) * mm});
            skLineSegment(sketch, "E370", {"start": v(-3.8, 2.87) * mm, "end": v(-3.8, 2.85) * mm});
            skLineSegment(sketch, "E371", {"start": v(-3.8, 2.85) * mm, "end": v(-3.79, 2.84) * mm});
            skLineSegment(sketch, "E372", {"start": v(-3.79, 2.84) * mm, "end": v(-3.78, 2.84) * mm});
            skLineSegment(sketch, "E373", {"start": v(-3.78, 2.84) * mm, "end": v(-3.81, 2.79) * mm});
            skLineSegment(sketch, "E374", {"start": v(-3.81, 2.79) * mm, "end": v(-3.82, 2.78) * mm});
            skLineSegment(sketch, "E375", {"start": v(-3.82, 2.78) * mm, "end": v(-3.86, 2.73) * mm});
            skLineSegment(sketch, "E376", {"start": v(-3.86, 2.73) * mm, "end": v(-3.87, 2.74) * mm});
            skLineSegment(sketch, "E377", {"start": v(-3.87, 2.74) * mm, "end": v(-3.88, 2.74) * mm});
            skLineSegment(sketch, "E378", {"start": v(-3.88, 2.74) * mm, "end": v(-3.9, 2.74) * mm});
            skLineSegment(sketch, "E379", {"start": v(-3.9, 2.74) * mm, "end": v(-3.9, 2.75) * mm});
            skLineSegment(sketch, "E380", {"start": v(-3.9, 2.75) * mm, "end": v(-3.92, 2.75) * mm});
            skLineSegment(sketch, "E381", {"start": v(-3.92, 2.75) * mm, "end": v(-3.94, 2.75) * mm});
            skLineSegment(sketch, "E382", {"start": v(-3.94, 2.75) * mm, "end": v(-3.95, 2.76) * mm});
            skLineSegment(sketch, "E383", {"start": v(-3.95, 2.76) * mm, "end": v(-3.97, 2.76) * mm});
            skLineSegment(sketch, "E384", {"start": v(-3.97, 2.76) * mm, "end": v(-3.98, 2.76) * mm});
            skLineSegment(sketch, "E385", {"start": v(-3.98, 2.76) * mm, "end": v(-4, 2.77) * mm});
            skLineSegment(sketch, "E386", {"start": v(-4, 2.77) * mm, "end": v(-4.02, 2.77) * mm});
            skLineSegment(sketch, "E387", {"start": v(-4.02, 2.77) * mm, "end": v(-4.04, 2.77) * mm});
            skLineSegment(sketch, "E388", {"start": v(-4.04, 2.77) * mm, "end": v(-4.05, 2.78) * mm});
            skLineSegment(sketch, "E389", {"start": v(-4.05, 2.78) * mm, "end": v(-4.07, 2.78) * mm});
            skLineSegment(sketch, "E390", {"start": v(-4.07, 2.78) * mm, "end": v(-4.09, 2.78) * mm});
            skLineSegment(sketch, "E391", {"start": v(-4.09, 2.78) * mm, "end": v(-4.1, 2.79) * mm});
            skLineSegment(sketch, "E392", {"start": v(-4.1, 2.79) * mm, "end": v(-4.13, 2.79) * mm});
            skLineSegment(sketch, "E393", {"start": v(-4.13, 2.79) * mm, "end": v(-4.15, 2.8) * mm});
            skLineSegment(sketch, "E394", {"start": v(-4.15, 2.8) * mm, "end": v(-4.17, 2.8) * mm});
            skLineSegment(sketch, "E395", {"start": v(-4.17, 2.8) * mm, "end": v(-4.19, 2.8) * mm});
            skLineSegment(sketch, "E396", {"start": v(-4.19, 2.8) * mm, "end": v(-4.2, 2.8) * mm});
            skLineSegment(sketch, "E397", {"start": v(-4.2, 2.8) * mm, "end": v(-4.23, 2.8) * mm});
            skLineSegment(sketch, "E398", {"start": v(-4.23, 2.8) * mm, "end": v(-4.25, 2.8) * mm});
            skLineSegment(sketch, "E399", {"start": v(-4.25, 2.8) * mm, "end": v(-4.27, 2.8) * mm});
            skLineSegment(sketch, "E400", {"start": v(-4.27, 2.8) * mm, "end": v(-4.3, 2.8) * mm});
            skLineSegment(sketch, "E401", {"start": v(-4.3, 2.8) * mm, "end": v(-4.31, 2.8) * mm});
            skLineSegment(sketch, "E402", {"start": v(-4.31, 2.8) * mm, "end": v(-4.34, 2.8) * mm});
            skLineSegment(sketch, "E403", {"start": v(-4.34, 2.8) * mm, "end": v(-4.36, 2.8) * mm});
            skLineSegment(sketch, "E404", {"start": v(-4.36, 2.8) * mm, "end": v(-4.38, 2.8) * mm});
            skLineSegment(sketch, "E405", {"start": v(-4.38, 2.8) * mm, "end": v(-4.4, 2.8) * mm});
            skLineSegment(sketch, "E406", {"start": v(-4.4, 2.8) * mm, "end": v(-4.43, 2.8) * mm});
            skLineSegment(sketch, "E407", {"start": v(-4.43, 2.8) * mm, "end": v(-4.45, 2.8) * mm});
            skLineSegment(sketch, "E408", {"start": v(-4.45, 2.8) * mm, "end": v(-4.5, 2.71) * mm});
            skLineSegment(sketch, "E409", {"start": v(-4.5, 2.71) * mm, "end": v(-4.5, 2.69) * mm});
            skLineSegment(sketch, "E410", {"start": v(-4.5, 2.69) * mm, "end": v(-4.5, 2.67) * mm});
            skLineSegment(sketch, "E411", {"start": v(-4.5, 2.67) * mm, "end": v(-4.48, 2.65) * mm});
            skLineSegment(sketch, "E412", {"start": v(-4.48, 2.65) * mm, "end": v(-4.47, 2.62) * mm});
            skLineSegment(sketch, "E413", {"start": v(-4.47, 2.62) * mm, "end": v(-4.46, 2.6) * mm});
            skLineSegment(sketch, "E414", {"start": v(-4.46, 2.6) * mm, "end": v(-4.45, 2.59) * mm});
            skLineSegment(sketch, "E415", {"start": v(-4.45, 2.59) * mm, "end": v(-4.44, 2.57) * mm});
            skLineSegment(sketch, "E416", {"start": v(-4.44, 2.57) * mm, "end": v(-4.43, 2.55) * mm});
            skLineSegment(sketch, "E417", {"start": v(-4.43, 2.55) * mm, "end": v(-4.42, 2.53) * mm});
            skLineSegment(sketch, "E418", {"start": v(-4.42, 2.53) * mm, "end": v(-4.4, 2.51) * mm});
            skLineSegment(sketch, "E419", {"start": v(-4.4, 2.51) * mm, "end": v(-4.4, 2.5) * mm});
            skLineSegment(sketch, "E420", {"start": v(-4.4, 2.5) * mm, "end": v(-4.38, 2.48) * mm});
            skLineSegment(sketch, "E421", {"start": v(-4.38, 2.48) * mm, "end": v(-4.37, 2.46) * mm});
            skLineSegment(sketch, "E422", {"start": v(-4.37, 2.46) * mm, "end": v(-4.36, 2.44) * mm});
            skLineSegment(sketch, "E423", {"start": v(-4.36, 2.44) * mm, "end": v(-4.35, 2.43) * mm});
            skLineSegment(sketch, "E424", {"start": v(-4.35, 2.43) * mm, "end": v(-4.34, 2.4) * mm});
            skLineSegment(sketch, "E425", {"start": v(-4.34, 2.4) * mm, "end": v(-4.33, 2.4) * mm});
            skLineSegment(sketch, "E426", {"start": v(-4.33, 2.4) * mm, "end": v(-4.32, 2.38) * mm});
            skLineSegment(sketch, "E427", {"start": v(-4.32, 2.38) * mm, "end": v(-4.3, 2.36) * mm});
            skLineSegment(sketch, "E428", {"start": v(-4.3, 2.36) * mm, "end": v(-4.3, 2.35) * mm});
            skLineSegment(sketch, "E429", {"start": v(-4.3, 2.35) * mm, "end": v(-4.29, 2.34) * mm});
            skLineSegment(sketch, "E430", {"start": v(-4.29, 2.34) * mm, "end": v(-4.28, 2.32) * mm});
            skLineSegment(sketch, "E431", {"start": v(-4.28, 2.32) * mm, "end": v(-4.27, 2.3) * mm});
            skLineSegment(sketch, "E432", {"start": v(-4.27, 2.3) * mm, "end": v(-4.25, 2.3) * mm});
            skLineSegment(sketch, "E433", {"start": v(-4.25, 2.3) * mm, "end": v(-4.24, 2.28) * mm});
            skLineSegment(sketch, "E434", {"start": v(-4.24, 2.28) * mm, "end": v(-4.23, 2.27) * mm});
            skLineSegment(sketch, "E435", {"start": v(-4.23, 2.27) * mm, "end": v(-4.22, 2.26) * mm});
            skLineSegment(sketch, "E436", {"start": v(-4.22, 2.26) * mm, "end": v(-4.21, 2.25) * mm});
            skLineSegment(sketch, "E437", {"start": v(-4.21, 2.25) * mm, "end": v(-4.2, 2.24) * mm});
            skLineSegment(sketch, "E438", {"start": v(-4.2, 2.24) * mm, "end": v(-4.2, 2.23) * mm});
            skLineSegment(sketch, "E439", {"start": v(-4.2, 2.23) * mm, "end": v(-4.19, 2.22) * mm});
            skLineSegment(sketch, "E440", {"start": v(-4.19, 2.22) * mm, "end": v(-4.18, 2.2) * mm});
            skLineSegment(sketch, "E441", {"start": v(-4.18, 2.2) * mm, "end": v(-4.2, 2.16) * mm});
            skLineSegment(sketch, "E442", {"start": v(-4.2, 2.16) * mm, "end": v(-4.2, 2.14) * mm});
            skLineSegment(sketch, "E443", {"start": v(-4.2, 2.14) * mm, "end": v(-4.24, 2.1) * mm});
            skLineSegment(sketch, "E444", {"start": v(-4.24, 2.1) * mm, "end": v(-4.25, 2.1) * mm});
            skLineSegment(sketch, "E445", {"start": v(-4.25, 2.1) * mm, "end": v(-4.26, 2.1) * mm});
            skLineSegment(sketch, "E446", {"start": v(-4.26, 2.1) * mm, "end": v(-4.27, 2.1) * mm});
            skLineSegment(sketch, "E447", {"start": v(-4.27, 2.1) * mm, "end": v(-4.29, 2.1) * mm});
            skLineSegment(sketch, "E448", {"start": v(-4.29, 2.1) * mm, "end": v(-4.3, 2.1) * mm});
            skLineSegment(sketch, "E449", {"start": v(-4.3, 2.1) * mm, "end": v(-4.32, 2.1) * mm});
            skLineSegment(sketch, "E450", {"start": v(-4.32, 2.1) * mm, "end": v(-4.34, 2.1) * mm});
            skLineSegment(sketch, "E451", {"start": v(-4.34, 2.1) * mm, "end": v(-4.35, 2.1) * mm});
            skLineSegment(sketch, "E452", {"start": v(-4.35, 2.1) * mm, "end": v(-4.37, 2.1) * mm});
            skLineSegment(sketch, "E453", {"start": v(-4.37, 2.1) * mm, "end": v(-4.38, 2.1) * mm});
            skLineSegment(sketch, "E454", {"start": v(-4.38, 2.1) * mm, "end": v(-4.4, 2.1) * mm});
            skLineSegment(sketch, "E455", {"start": v(-4.4, 2.1) * mm, "end": v(-4.42, 2.1) * mm});
            skLineSegment(sketch, "E456", {"start": v(-4.42, 2.1) * mm, "end": v(-4.44, 2.1) * mm});
            skLineSegment(sketch, "E457", {"start": v(-4.44, 2.1) * mm, "end": v(-4.46, 2.1) * mm});
            skLineSegment(sketch, "E458", {"start": v(-4.46, 2.1) * mm, "end": v(-4.47, 2.1) * mm});
            skLineSegment(sketch, "E459", {"start": v(-4.47, 2.1) * mm, "end": v(-4.5, 2.1) * mm});
            skLineSegment(sketch, "E460", {"start": v(-4.5, 2.1) * mm, "end": v(-4.51, 2.1) * mm});
            skLineSegment(sketch, "E461", {"start": v(-4.51, 2.1) * mm, "end": v(-4.53, 2.1) * mm});
            skLineSegment(sketch, "E462", {"start": v(-4.53, 2.1) * mm, "end": v(-4.55, 2.1) * mm});
            skLineSegment(sketch, "E463", {"start": v(-4.55, 2.1) * mm, "end": v(-4.57, 2.1) * mm});
            skLineSegment(sketch, "E464", {"start": v(-4.57, 2.1) * mm, "end": v(-4.6, 2.1) * mm});
            skLineSegment(sketch, "E465", {"start": v(-4.6, 2.1) * mm, "end": v(-4.61, 2.1) * mm});
            skLineSegment(sketch, "E466", {"start": v(-4.61, 2.1) * mm, "end": v(-4.64, 2.1) * mm});
            skLineSegment(sketch, "E467", {"start": v(-4.64, 2.1) * mm, "end": v(-4.66, 2.1) * mm});
            skLineSegment(sketch, "E468", {"start": v(-4.66, 2.1) * mm, "end": v(-4.68, 2.1) * mm});
            skLineSegment(sketch, "E469", {"start": v(-4.68, 2.1) * mm, "end": v(-4.7, 2.1) * mm});
            skLineSegment(sketch, "E470", {"start": v(-4.7, 2.1) * mm, "end": v(-4.72, 2.1) * mm});
            skLineSegment(sketch, "E471", {"start": v(-4.72, 2.1) * mm, "end": v(-4.75, 2.1) * mm});
            skLineSegment(sketch, "E472", {"start": v(-4.75, 2.1) * mm, "end": v(-4.77, 2.09) * mm});
            skLineSegment(sketch, "E473", {"start": v(-4.77, 2.09) * mm, "end": v(-4.8, 2.08) * mm});
            skLineSegment(sketch, "E474", {"start": v(-4.8, 2.08) * mm, "end": v(-4.82, 2.08) * mm});
            skLineSegment(sketch, "E475", {"start": v(-4.82, 2.08) * mm, "end": v(-4.84, 2.07) * mm});
            skLineSegment(sketch, "E476", {"start": v(-4.84, 2.07) * mm, "end": v(-4.88, 1.97) * mm});
            skLineSegment(sketch, "E477", {"start": v(-4.88, 1.97) * mm, "end": v(-4.87, 1.95) * mm});
            skLineSegment(sketch, "E478", {"start": v(-4.87, 1.95) * mm, "end": v(-4.86, 1.93) * mm});
            skLineSegment(sketch, "E479", {"start": v(-4.86, 1.93) * mm, "end": v(-4.84, 1.91) * mm});
            skLineSegment(sketch, "E480", {"start": v(-4.84, 1.91) * mm, "end": v(-4.83, 1.9) * mm});
            skLineSegment(sketch, "E481", {"start": v(-4.83, 1.9) * mm, "end": v(-4.81, 1.87) * mm});
            skLineSegment(sketch, "E482", {"start": v(-4.81, 1.87) * mm, "end": v(-4.8, 1.86) * mm});
            skLineSegment(sketch, "E483", {"start": v(-4.8, 1.86) * mm, "end": v(-4.79, 1.84) * mm});
            skLineSegment(sketch, "E484", {"start": v(-4.79, 1.84) * mm, "end": v(-4.77, 1.82) * mm});
            skLineSegment(sketch, "E485", {"start": v(-4.77, 1.82) * mm, "end": v(-4.76, 1.8) * mm});
            skLineSegment(sketch, "E486", {"start": v(-4.76, 1.8) * mm, "end": v(-4.74, 1.8) * mm});
            skLineSegment(sketch, "E487", {"start": v(-4.74, 1.8) * mm, "end": v(-4.73, 1.77) * mm});
            skLineSegment(sketch, "E488", {"start": v(-4.73, 1.77) * mm, "end": v(-4.72, 1.76) * mm});
            skLineSegment(sketch, "E489", {"start": v(-4.72, 1.76) * mm, "end": v(-4.7, 1.74) * mm});
            skLineSegment(sketch, "E490", {"start": v(-4.7, 1.74) * mm, "end": v(-4.69, 1.73) * mm});
            skLineSegment(sketch, "E491", {"start": v(-4.69, 1.73) * mm, "end": v(-4.68, 1.71) * mm});
            skLineSegment(sketch, "E492", {"start": v(-4.68, 1.71) * mm, "end": v(-4.66, 1.7) * mm});
            skLineSegment(sketch, "E493", {"start": v(-4.66, 1.7) * mm, "end": v(-4.65, 1.69) * mm});
            skLineSegment(sketch, "E494", {"start": v(-4.65, 1.69) * mm, "end": v(-4.64, 1.67) * mm});
            skLineSegment(sketch, "E495", {"start": v(-4.64, 1.67) * mm, "end": v(-4.62, 1.66) * mm});
            skLineSegment(sketch, "E496", {"start": v(-4.62, 1.66) * mm, "end": v(-4.61, 1.65) * mm});
            skLineSegment(sketch, "E497", {"start": v(-4.61, 1.65) * mm, "end": v(-4.6, 1.64) * mm});
            skLineSegment(sketch, "E498", {"start": v(-4.6, 1.64) * mm, "end": v(-4.59, 1.62) * mm});
            skLineSegment(sketch, "E499", {"start": v(-4.59, 1.62) * mm, "end": v(-4.57, 1.61) * mm});
            skLineSegment(sketch, "E500", {"start": v(-4.57, 1.61) * mm, "end": v(-4.56, 1.6) * mm});
            skLineSegment(sketch, "E501", {"start": v(-4.56, 1.6) * mm, "end": v(-4.55, 1.6) * mm});
            skLineSegment(sketch, "E502", {"start": v(-4.55, 1.6) * mm, "end": v(-4.54, 1.58) * mm});
            skLineSegment(sketch, "E503", {"start": v(-4.54, 1.58) * mm, "end": v(-4.53, 1.57) * mm});
            skLineSegment(sketch, "E504", {"start": v(-4.53, 1.57) * mm, "end": v(-4.51, 1.56) * mm});
            skLineSegment(sketch, "E505", {"start": v(-4.51, 1.56) * mm, "end": v(-4.5, 1.55) * mm});
            skLineSegment(sketch, "E506", {"start": v(-4.5, 1.55) * mm, "end": v(-4.5, 1.54) * mm});
            skLineSegment(sketch, "E507", {"start": v(-4.5, 1.54) * mm, "end": v(-4.48, 1.53) * mm});
            skLineSegment(sketch, "E508", {"start": v(-4.48, 1.53) * mm, "end": v(-4.47, 1.53) * mm});
            skLineSegment(sketch, "E509", {"start": v(-4.47, 1.53) * mm, "end": v(-4.49, 1.47) * mm});
            skLineSegment(sketch, "E510", {"start": v(-4.49, 1.47) * mm, "end": v(-4.5, 1.46) * mm});
            skLineSegment(sketch, "E511", {"start": v(-4.5, 1.46) * mm, "end": v(-4.51, 1.4) * mm});
            skLineSegment(sketch, "E512", {"start": v(-4.51, 1.4) * mm, "end": v(-4.52, 1.4) * mm});
            skLineSegment(sketch, "E513", {"start": v(-4.52, 1.4) * mm, "end": v(-4.54, 1.4) * mm});
            skLineSegment(sketch, "E514", {"start": v(-4.54, 1.4) * mm, "end": v(-4.55, 1.4) * mm});
            skLineSegment(sketch, "E515", {"start": v(-4.55, 1.4) * mm, "end": v(-4.57, 1.4) * mm});
            skLineSegment(sketch, "E516", {"start": v(-4.57, 1.4) * mm, "end": v(-4.58, 1.4) * mm});
            skLineSegment(sketch, "E517", {"start": v(-4.58, 1.4) * mm, "end": v(-4.6, 1.4) * mm});
            skLineSegment(sketch, "E518", {"start": v(-4.6, 1.4) * mm, "end": v(-4.61, 1.4) * mm});
            skLineSegment(sketch, "E519", {"start": v(-4.61, 1.4) * mm, "end": v(-4.63, 1.4) * mm});
            skLineSegment(sketch, "E520", {"start": v(-4.63, 1.4) * mm, "end": v(-4.64, 1.4) * mm});
            skLineSegment(sketch, "E521", {"start": v(-4.64, 1.4) * mm, "end": v(-4.66, 1.4) * mm});
            skLineSegment(sketch, "E522", {"start": v(-4.66, 1.4) * mm, "end": v(-4.68, 1.4) * mm});
            skLineSegment(sketch, "E523", {"start": v(-4.68, 1.4) * mm, "end": v(-4.7, 1.4) * mm});
            skLineSegment(sketch, "E524", {"start": v(-4.7, 1.4) * mm, "end": v(-4.71, 1.39) * mm});
            skLineSegment(sketch, "E525", {"start": v(-4.71, 1.39) * mm, "end": v(-4.73, 1.39) * mm});
            skLineSegment(sketch, "E526", {"start": v(-4.73, 1.39) * mm, "end": v(-4.75, 1.38) * mm});
            skLineSegment(sketch, "E527", {"start": v(-4.75, 1.38) * mm, "end": v(-4.77, 1.38) * mm});
            skLineSegment(sketch, "E528", {"start": v(-4.77, 1.38) * mm, "end": v(-4.79, 1.38) * mm});
            skLineSegment(sketch, "E529", {"start": v(-4.79, 1.38) * mm, "end": v(-4.8, 1.37) * mm});
            skLineSegment(sketch, "E530", {"start": v(-4.8, 1.37) * mm, "end": v(-4.83, 1.37) * mm});
            skLineSegment(sketch, "E531", {"start": v(-4.83, 1.37) * mm, "end": v(-4.85, 1.37) * mm});
            skLineSegment(sketch, "E532", {"start": v(-4.85, 1.37) * mm, "end": v(-4.87, 1.36) * mm});
            skLineSegment(sketch, "E533", {"start": v(-4.87, 1.36) * mm, "end": v(-4.89, 1.36) * mm});
            skLineSegment(sketch, "E534", {"start": v(-4.89, 1.36) * mm, "end": v(-4.9, 1.35) * mm});
            skLineSegment(sketch, "E535", {"start": v(-4.9, 1.35) * mm, "end": v(-4.93, 1.35) * mm});
            skLineSegment(sketch, "E536", {"start": v(-4.93, 1.35) * mm, "end": v(-4.95, 1.34) * mm});
            skLineSegment(sketch, "E537", {"start": v(-4.95, 1.34) * mm, "end": v(-4.97, 1.34) * mm});
            skLineSegment(sketch, "E538", {"start": v(-4.97, 1.34) * mm, "end": v(-5, 1.33) * mm});
            skLineSegment(sketch, "E539", {"start": v(-5, 1.33) * mm, "end": v(-5.01, 1.32) * mm});
            skLineSegment(sketch, "E540", {"start": v(-5.01, 1.32) * mm, "end": v(-5.04, 1.32) * mm});
            skLineSegment(sketch, "E541", {"start": v(-5.04, 1.32) * mm, "end": v(-5.06, 1.3) * mm});
            skLineSegment(sketch, "E542", {"start": v(-5.06, 1.3) * mm, "end": v(-5.08, 1.3) * mm});
            skLineSegment(sketch, "E543", {"start": v(-5.08, 1.3) * mm, "end": v(-5.1, 1.29) * mm});
            skLineSegment(sketch, "E544", {"start": v(-5.1, 1.29) * mm, "end": v(-5.13, 1.18) * mm});
            skLineSegment(sketch, "E545", {"start": v(-5.13, 1.18) * mm, "end": v(-5.12, 1.17) * mm});
            skLineSegment(sketch, "E546", {"start": v(-5.12, 1.17) * mm, "end": v(-5.1, 1.15) * mm});
            skLineSegment(sketch, "E547", {"start": v(-5.1, 1.15) * mm, "end": v(-5.08, 1.13) * mm});
            skLineSegment(sketch, "E548", {"start": v(-5.08, 1.13) * mm, "end": v(-5.07, 1.11) * mm});
            skLineSegment(sketch, "E549", {"start": v(-5.07, 1.11) * mm, "end": v(-5.05, 1.1) * mm});
            skLineSegment(sketch, "E550", {"start": v(-5.05, 1.1) * mm, "end": v(-5.03, 1.08) * mm});
            skLineSegment(sketch, "E551", {"start": v(-5.03, 1.08) * mm, "end": v(-5.01, 1.07) * mm});
            skLineSegment(sketch, "E552", {"start": v(-5.01, 1.07) * mm, "end": v(-5, 1.05) * mm});
            skLineSegment(sketch, "E553", {"start": v(-5, 1.05) * mm, "end": v(-4.98, 1.04) * mm});
            skLineSegment(sketch, "E554", {"start": v(-4.98, 1.04) * mm, "end": v(-4.97, 1.03) * mm});
            skLineSegment(sketch, "E555", {"start": v(-4.97, 1.03) * mm, "end": v(-4.95, 1.01) * mm});
            skLineSegment(sketch, "E556", {"start": v(-4.95, 1.01) * mm, "end": v(-4.93, 1) * mm});
            skLineSegment(sketch, "E557", {"start": v(-4.93, 1) * mm, "end": v(-4.92, 0.99) * mm});
            skLineSegment(sketch, "E558", {"start": v(-4.92, 0.99) * mm, "end": v(-4.9, 0.97) * mm});
            skLineSegment(sketch, "E559", {"start": v(-4.9, 0.97) * mm, "end": v(-4.89, 0.96) * mm});
            skLineSegment(sketch, "E560", {"start": v(-4.89, 0.96) * mm, "end": v(-4.87, 0.95) * mm});
            skLineSegment(sketch, "E561", {"start": v(-4.87, 0.95) * mm, "end": v(-4.86, 0.94) * mm});
            skLineSegment(sketch, "E562", {"start": v(-4.86, 0.94) * mm, "end": v(-4.84, 0.93) * mm});
            skLineSegment(sketch, "E563", {"start": v(-4.84, 0.93) * mm, "end": v(-4.83, 0.92) * mm});
            skLineSegment(sketch, "E564", {"start": v(-4.83, 0.92) * mm, "end": v(-4.81, 0.9) * mm});
            skLineSegment(sketch, "E565", {"start": v(-4.81, 0.9) * mm, "end": v(-4.8, 0.9) * mm});
            skLineSegment(sketch, "E566", {"start": v(-4.8, 0.9) * mm, "end": v(-4.78, 0.89) * mm});
            skLineSegment(sketch, "E567", {"start": v(-4.78, 0.89) * mm, "end": v(-4.77, 0.88) * mm});
            skLineSegment(sketch, "E568", {"start": v(-4.77, 0.88) * mm, "end": v(-4.76, 0.87) * mm});
            skLineSegment(sketch, "E569", {"start": v(-4.76, 0.87) * mm, "end": v(-4.74, 0.86) * mm});
            skLineSegment(sketch, "E570", {"start": v(-4.74, 0.86) * mm, "end": v(-4.73, 0.85) * mm});
            skLineSegment(sketch, "E571", {"start": v(-4.73, 0.85) * mm, "end": v(-4.72, 0.84) * mm});
            skLineSegment(sketch, "E572", {"start": v(-4.72, 0.84) * mm, "end": v(-4.7, 0.84) * mm});
            skLineSegment(sketch, "E573", {"start": v(-4.7, 0.84) * mm, "end": v(-4.7, 0.83) * mm});
            skLineSegment(sketch, "E574", {"start": v(-4.7, 0.83) * mm, "end": v(-4.68, 0.82) * mm});
            skLineSegment(sketch, "E575", {"start": v(-4.68, 0.82) * mm, "end": v(-4.67, 0.81) * mm});
            skLineSegment(sketch, "E576", {"start": v(-4.67, 0.81) * mm, "end": v(-4.66, 0.8) * mm});
            skLineSegment(sketch, "E577", {"start": v(-4.66, 0.8) * mm, "end": v(-4.66, 0.75) * mm});
            skLineSegment(sketch, "E578", {"start": v(-4.66, 0.75) * mm, "end": v(-4.67, 0.74) * mm});
            skLineSegment(sketch, "E579", {"start": v(-4.67, 0.74) * mm, "end": v(-4.68, 0.69) * mm});
            skLineSegment(sketch, "E580", {"start": v(-4.68, 0.69) * mm, "end": v(-4.69, 0.68) * mm});
            skLineSegment(sketch, "E581", {"start": v(-4.69, 0.68) * mm, "end": v(-4.7, 0.68) * mm});
            skLineSegment(sketch, "E582", {"start": v(-4.7, 0.68) * mm, "end": v(-4.71, 0.68) * mm});
            skLineSegment(sketch, "E583", {"start": v(-4.71, 0.68) * mm, "end": v(-4.73, 0.67) * mm});
            skLineSegment(sketch, "E584", {"start": v(-4.73, 0.67) * mm, "end": v(-4.74, 0.67) * mm});
            skLineSegment(sketch, "E585", {"start": v(-4.74, 0.67) * mm, "end": v(-4.76, 0.67) * mm});
            skLineSegment(sketch, "E586", {"start": v(-4.76, 0.67) * mm, "end": v(-4.77, 0.66) * mm});
            skLineSegment(sketch, "E587", {"start": v(-4.77, 0.66) * mm, "end": v(-4.79, 0.66) * mm});
            skLineSegment(sketch, "E588", {"start": v(-4.79, 0.66) * mm, "end": v(-4.8, 0.65) * mm});
            skLineSegment(sketch, "E589", {"start": v(-4.8, 0.65) * mm, "end": v(-4.82, 0.65) * mm});
            skLineSegment(sketch, "E590", {"start": v(-4.82, 0.65) * mm, "end": v(-4.84, 0.65) * mm});
            skLineSegment(sketch, "E591", {"start": v(-4.84, 0.65) * mm, "end": v(-4.86, 0.64) * mm});
            skLineSegment(sketch, "E592", {"start": v(-4.86, 0.64) * mm, "end": v(-4.87, 0.64) * mm});
            skLineSegment(sketch, "E593", {"start": v(-4.87, 0.64) * mm, "end": v(-4.89, 0.63) * mm});
            skLineSegment(sketch, "E594", {"start": v(-4.89, 0.63) * mm, "end": v(-4.9, 0.62) * mm});
            skLineSegment(sketch, "E595", {"start": v(-4.9, 0.62) * mm, "end": v(-4.93, 0.62) * mm});
            skLineSegment(sketch, "E596", {"start": v(-4.93, 0.62) * mm, "end": v(-4.94, 0.61) * mm});
            skLineSegment(sketch, "E597", {"start": v(-4.94, 0.61) * mm, "end": v(-4.96, 0.6) * mm});
            skLineSegment(sketch, "E598", {"start": v(-4.96, 0.6) * mm, "end": v(-4.98, 0.6) * mm});
            skLineSegment(sketch, "E599", {"start": v(-4.98, 0.6) * mm, "end": v(-5, 0.6) * mm});
            skLineSegment(sketch, "E600", {"start": v(-5, 0.6) * mm, "end": v(-5.02, 0.58) * mm});
            skLineSegment(sketch, "E601", {"start": v(-5.02, 0.58) * mm, "end": v(-5.04, 0.58) * mm});
            skLineSegment(sketch, "E602", {"start": v(-5.04, 0.58) * mm, "end": v(-5.06, 0.57) * mm});
            skLineSegment(sketch, "E603", {"start": v(-5.06, 0.57) * mm, "end": v(-5.08, 0.56) * mm});
            skLineSegment(sketch, "E604", {"start": v(-5.08, 0.56) * mm, "end": v(-5.1, 0.55) * mm});
            skLineSegment(sketch, "E605", {"start": v(-5.1, 0.55) * mm, "end": v(-5.12, 0.54) * mm});
            skLineSegment(sketch, "E606", {"start": v(-5.12, 0.54) * mm, "end": v(-5.14, 0.53) * mm});
            skLineSegment(sketch, "E607", {"start": v(-5.14, 0.53) * mm, "end": v(-5.16, 0.52) * mm});
            skLineSegment(sketch, "E608", {"start": v(-5.16, 0.52) * mm, "end": v(-5.18, 0.51) * mm});
            skLineSegment(sketch, "E609", {"start": v(-5.18, 0.51) * mm, "end": v(-5.2, 0.5) * mm});
            skLineSegment(sketch, "E610", {"start": v(-5.2, 0.5) * mm, "end": v(-5.23, 0.5) * mm});
            skLineSegment(sketch, "E611", {"start": v(-5.23, 0.5) * mm, "end": v(-5.24, 0.47) * mm});
            skLineSegment(sketch, "E612", {"start": v(-5.24, 0.47) * mm, "end": v(-5.25, 0.37) * mm});
            skLineSegment(sketch, "E613", {"start": v(-5.25, 0.37) * mm, "end": v(-5.24, 0.35) * mm});
            skLineSegment(sketch, "E614", {"start": v(-5.24, 0.35) * mm, "end": v(-5.22, 0.34) * mm});
            skLineSegment(sketch, "E615", {"start": v(-5.22, 0.34) * mm, "end": v(-5.2, 0.32) * mm});
            skLineSegment(sketch, "E616", {"start": v(-5.2, 0.32) * mm, "end": v(-5.18, 0.3) * mm});
            skLineSegment(sketch, "E617", {"start": v(-5.18, 0.3) * mm, "end": v(-5.16, 0.3) * mm});
            skLineSegment(sketch, "E618", {"start": v(-5.16, 0.3) * mm, "end": v(-5.14, 0.28) * mm});
            skLineSegment(sketch, "E619", {"start": v(-5.14, 0.28) * mm, "end": v(-5.12, 0.27) * mm});
            skLineSegment(sketch, "E620", {"start": v(-5.12, 0.27) * mm, "end": v(-5.1, 0.26) * mm});
            skLineSegment(sketch, "E621", {"start": v(-5.1, 0.26) * mm, "end": v(-5.08, 0.25) * mm});
            skLineSegment(sketch, "E622", {"start": v(-5.08, 0.25) * mm, "end": v(-5.07, 0.24) * mm});
            skLineSegment(sketch, "E623", {"start": v(-5.07, 0.24) * mm, "end": v(-5.05, 0.23) * mm});
            skLineSegment(sketch, "E624", {"start": v(-5.05, 0.23) * mm, "end": v(-5.03, 0.22) * mm});
            skLineSegment(sketch, "E625", {"start": v(-5.03, 0.22) * mm, "end": v(-5.01, 0.2) * mm});
            skLineSegment(sketch, "E626", {"start": v(-5.01, 0.2) * mm, "end": v(-5, 0.2) * mm});
            skLineSegment(sketch, "E627", {"start": v(-5, 0.2) * mm, "end": v(-4.98, 0.19) * mm});
            skLineSegment(sketch, "E628", {"start": v(-4.98, 0.19) * mm, "end": v(-4.96, 0.18) * mm});
            skLineSegment(sketch, "E629", {"start": v(-4.96, 0.18) * mm, "end": v(-4.94, 0.17) * mm});
            skLineSegment(sketch, "E630", {"start": v(-4.94, 0.17) * mm, "end": v(-4.93, 0.16) * mm});
            skLineSegment(sketch, "E631", {"start": v(-4.93, 0.16) * mm, "end": v(-4.91, 0.15) * mm});
            skLineSegment(sketch, "E632", {"start": v(-4.91, 0.15) * mm, "end": v(-4.9, 0.14) * mm});
            skLineSegment(sketch, "E633", {"start": v(-4.9, 0.14) * mm, "end": v(-4.88, 0.14) * mm});
            skLineSegment(sketch, "E634", {"start": v(-4.88, 0.14) * mm, "end": v(-4.86, 0.13) * mm});
            skLineSegment(sketch, "E635", {"start": v(-4.86, 0.13) * mm, "end": v(-4.85, 0.12) * mm});
            skLineSegment(sketch, "E636", {"start": v(-4.85, 0.12) * mm, "end": v(-4.83, 0.11) * mm});
            skLineSegment(sketch, "E637", {"start": v(-4.83, 0.11) * mm, "end": v(-4.82, 0.1) * mm});
            skLineSegment(sketch, "E638", {"start": v(-4.82, 0.1) * mm, "end": v(-4.8, 0.1) * mm});
            skLineSegment(sketch, "E639", {"start": v(-4.8, 0.1) * mm, "end": v(-4.79, 0.1) * mm});
            skLineSegment(sketch, "E640", {"start": v(-4.79, 0.1) * mm, "end": v(-4.78, 0.09) * mm});
            skLineSegment(sketch, "E641", {"start": v(-4.78, 0.09) * mm, "end": v(-4.76, 0.08) * mm});
            skLineSegment(sketch, "E642", {"start": v(-4.76, 0.08) * mm, "end": v(-4.75, 0.08) * mm});
            skLineSegment(sketch, "E643", {"start": v(-4.75, 0.08) * mm, "end": v(-4.74, 0.07) * mm});
            skLineSegment(sketch, "E644", {"start": v(-4.74, 0.07) * mm, "end": v(-4.73, 0.07) * mm});
            skLineSegment(sketch, "E645", {"start": v(-4.73, 0.07) * mm, "end": v(-4.72, 0.02) * mm});
            skLineSegment(sketch, "E646", {"start": v(-4.72, 0.02) * mm, "end": v(-4.72, 0) * mm});
            skLineSegment(sketch, "E647", {"start": v(-4.72, 0) * mm, "end": v(-4.73, -0.06) * mm});
            skLineSegment(sketch, "E648", {"start": v(-4.73, -0.06) * mm, "end": v(-4.74, -0.06) * mm});
            skLineSegment(sketch, "E649", {"start": v(-4.74, -0.06) * mm, "end": v(-4.75, -0.06) * mm});
            skLineSegment(sketch, "E650", {"start": v(-4.75, -0.06) * mm, "end": v(-4.76, -0.07) * mm});
            skLineSegment(sketch, "E651", {"start": v(-4.76, -0.07) * mm, "end": v(-4.78, -0.07) * mm});
            skLineSegment(sketch, "E652", {"start": v(-4.78, -0.07) * mm, "end": v(-4.8, -0.08) * mm});
            skLineSegment(sketch, "E653", {"start": v(-4.8, -0.08) * mm, "end": v(-4.8, -0.09) * mm});
            skLineSegment(sketch, "E654", {"start": v(-4.8, -0.09) * mm, "end": v(-4.82, -0.1) * mm});
            skLineSegment(sketch, "E655", {"start": v(-4.82, -0.1) * mm, "end": v(-4.83, -0.1) * mm});
            skLineSegment(sketch, "E656", {"start": v(-4.83, -0.1) * mm, "end": v(-4.85, -0.1) * mm});
            skLineSegment(sketch, "E657", {"start": v(-4.85, -0.1) * mm, "end": v(-4.86, -0.11) * mm});
            skLineSegment(sketch, "E658", {"start": v(-4.86, -0.11) * mm, "end": v(-4.88, -0.12) * mm});
            skLineSegment(sketch, "E659", {"start": v(-4.88, -0.12) * mm, "end": v(-4.9, -0.13) * mm});
            skLineSegment(sketch, "E660", {"start": v(-4.9, -0.13) * mm, "end": v(-4.91, -0.13) * mm});
            skLineSegment(sketch, "E661", {"start": v(-4.91, -0.13) * mm, "end": v(-4.93, -0.14) * mm});
            skLineSegment(sketch, "E662", {"start": v(-4.93, -0.14) * mm, "end": v(-4.94, -0.15) * mm});
            skLineSegment(sketch, "E663", {"start": v(-4.94, -0.15) * mm, "end": v(-4.96, -0.16) * mm});
            skLineSegment(sketch, "E664", {"start": v(-4.96, -0.16) * mm, "end": v(-4.98, -0.17) * mm});
            skLineSegment(sketch, "E665", {"start": v(-4.98, -0.17) * mm, "end": v(-5, -0.18) * mm});
            skLineSegment(sketch, "E666", {"start": v(-5, -0.18) * mm, "end": v(-5.01, -0.19) * mm});
            skLineSegment(sketch, "E667", {"start": v(-5.01, -0.19) * mm, "end": v(-5.03, -0.2) * mm});
            skLineSegment(sketch, "E668", {"start": v(-5.03, -0.2) * mm, "end": v(-5.05, -0.2) * mm});
            skLineSegment(sketch, "E669", {"start": v(-5.05, -0.2) * mm, "end": v(-5.07, -0.22) * mm});
            skLineSegment(sketch, "E670", {"start": v(-5.07, -0.22) * mm, "end": v(-5.08, -0.23) * mm});
            skLineSegment(sketch, "E671", {"start": v(-5.08, -0.23) * mm, "end": v(-5.1, -0.24) * mm});
            skLineSegment(sketch, "E672", {"start": v(-5.1, -0.24) * mm, "end": v(-5.12, -0.25) * mm});
            skLineSegment(sketch, "E673", {"start": v(-5.12, -0.25) * mm, "end": v(-5.14, -0.27) * mm});
            skLineSegment(sketch, "E674", {"start": v(-5.14, -0.27) * mm, "end": v(-5.16, -0.28) * mm});
            skLineSegment(sketch, "E675", {"start": v(-5.16, -0.28) * mm, "end": v(-5.18, -0.3) * mm});
            skLineSegment(sketch, "E676", {"start": v(-5.18, -0.3) * mm, "end": v(-5.2, -0.3) * mm});
            skLineSegment(sketch, "E677", {"start": v(-5.2, -0.3) * mm, "end": v(-5.22, -0.32) * mm});
            skLineSegment(sketch, "E678", {"start": v(-5.22, -0.32) * mm, "end": v(-5.24, -0.33) * mm});
            skLineSegment(sketch, "E679", {"start": v(-5.24, -0.33) * mm, "end": v(-5.25, -0.35) * mm});
            skLineSegment(sketch, "E680", {"start": v(-5.25, -0.35) * mm, "end": v(-5.24, -0.46) * mm});
            skLineSegment(sketch, "E681", {"start": v(-5.24, -0.46) * mm, "end": v(-5.23, -0.47) * mm});
            skLineSegment(sketch, "E682", {"start": v(-5.23, -0.47) * mm, "end": v(-5.2, -0.48) * mm});
            skLineSegment(sketch, "E683", {"start": v(-5.2, -0.48) * mm, "end": v(-5.18, -0.5) * mm});
            skLineSegment(sketch, "E684", {"start": v(-5.18, -0.5) * mm, "end": v(-5.16, -0.5) * mm});
            skLineSegment(sketch, "E685", {"start": v(-5.16, -0.5) * mm, "end": v(-5.14, -0.51) * mm});
            skLineSegment(sketch, "E686", {"start": v(-5.14, -0.51) * mm, "end": v(-5.12, -0.52) * mm});
            skLineSegment(sketch, "E687", {"start": v(-5.12, -0.52) * mm, "end": v(-5.1, -0.53) * mm});
            skLineSegment(sketch, "E688", {"start": v(-5.1, -0.53) * mm, "end": v(-5.08, -0.54) * mm});
            skLineSegment(sketch, "E689", {"start": v(-5.08, -0.54) * mm, "end": v(-5.06, -0.55) * mm});
            skLineSegment(sketch, "E690", {"start": v(-5.06, -0.55) * mm, "end": v(-5.04, -0.56) * mm});
            skLineSegment(sketch, "E691", {"start": v(-5.04, -0.56) * mm, "end": v(-5.02, -0.57) * mm});
            skLineSegment(sketch, "E692", {"start": v(-5.02, -0.57) * mm, "end": v(-5, -0.57) * mm});
            skLineSegment(sketch, "E693", {"start": v(-5, -0.57) * mm, "end": v(-4.98, -0.58) * mm});
            skLineSegment(sketch, "E694", {"start": v(-4.98, -0.58) * mm, "end": v(-4.96, -0.59) * mm});
            skLineSegment(sketch, "E695", {"start": v(-4.96, -0.59) * mm, "end": v(-4.95, -0.6) * mm});
            skLineSegment(sketch, "E696", {"start": v(-4.95, -0.6) * mm, "end": v(-4.93, -0.6) * mm});
            skLineSegment(sketch, "E697", {"start": v(-4.93, -0.6) * mm, "end": v(-4.9, -0.6) * mm});
            skLineSegment(sketch, "E698", {"start": v(-4.9, -0.6) * mm, "end": v(-4.9, -0.61) * mm});
            skLineSegment(sketch, "E699", {"start": v(-4.9, -0.61) * mm, "end": v(-4.87, -0.62) * mm});
            skLineSegment(sketch, "E700", {"start": v(-4.87, -0.62) * mm, "end": v(-4.86, -0.62) * mm});
            skLineSegment(sketch, "E701", {"start": v(-4.86, -0.62) * mm, "end": v(-4.84, -0.63) * mm});
            skLineSegment(sketch, "E702", {"start": v(-4.84, -0.63) * mm, "end": v(-4.82, -0.63) * mm});
            skLineSegment(sketch, "E703", {"start": v(-4.82, -0.63) * mm, "end": v(-4.8, -0.64) * mm});
            skLineSegment(sketch, "E704", {"start": v(-4.8, -0.64) * mm, "end": v(-4.8, -0.64) * mm});
            skLineSegment(sketch, "E705", {"start": v(-4.8, -0.64) * mm, "end": v(-4.78, -0.65) * mm});
            skLineSegment(sketch, "E706", {"start": v(-4.78, -0.65) * mm, "end": v(-4.76, -0.65) * mm});
            skLineSegment(sketch, "E707", {"start": v(-4.76, -0.65) * mm, "end": v(-4.75, -0.65) * mm});
            skLineSegment(sketch, "E708", {"start": v(-4.75, -0.65) * mm, "end": v(-4.73, -0.66) * mm});
            skLineSegment(sketch, "E709", {"start": v(-4.73, -0.66) * mm, "end": v(-4.72, -0.66) * mm});
            skLineSegment(sketch, "E710", {"start": v(-4.72, -0.66) * mm, "end": v(-4.7, -0.66) * mm});
            skLineSegment(sketch, "E711", {"start": v(-4.7, -0.66) * mm, "end": v(-4.69, -0.67) * mm});
            skLineSegment(sketch, "E712", {"start": v(-4.69, -0.67) * mm, "end": v(-4.68, -0.67) * mm});
            skLineSegment(sketch, "E713", {"start": v(-4.68, -0.67) * mm, "end": v(-4.67, -0.72) * mm});
            skLineSegment(sketch, "E714", {"start": v(-4.67, -0.72) * mm, "end": v(-4.67, -0.74) * mm});
            skLineSegment(sketch, "E715", {"start": v(-4.67, -0.74) * mm, "end": v(-4.66, -0.8) * mm});
            skLineSegment(sketch, "E716", {"start": v(-4.66, -0.8) * mm, "end": v(-4.67, -0.8) * mm});
            skLineSegment(sketch, "E717", {"start": v(-4.67, -0.8) * mm, "end": v(-4.68, -0.8) * mm});
            skLineSegment(sketch, "E718", {"start": v(-4.68, -0.8) * mm, "end": v(-4.7, -0.81) * mm});
            skLineSegment(sketch, "E719", {"start": v(-4.7, -0.81) * mm, "end": v(-4.7, -0.82) * mm});
            skLineSegment(sketch, "E720", {"start": v(-4.7, -0.82) * mm, "end": v(-4.72, -0.83) * mm});
            skLineSegment(sketch, "E721", {"start": v(-4.72, -0.83) * mm, "end": v(-4.73, -0.84) * mm});
            skLineSegment(sketch, "E722", {"start": v(-4.73, -0.84) * mm, "end": v(-4.75, -0.84) * mm});
            skLineSegment(sketch, "E723", {"start": v(-4.75, -0.84) * mm, "end": v(-4.76, -0.85) * mm});
            skLineSegment(sketch, "E724", {"start": v(-4.76, -0.85) * mm, "end": v(-4.77, -0.86) * mm});
            skLineSegment(sketch, "E725", {"start": v(-4.77, -0.86) * mm, "end": v(-4.79, -0.87) * mm});
            skLineSegment(sketch, "E726", {"start": v(-4.79, -0.87) * mm, "end": v(-4.8, -0.88) * mm});
            skLineSegment(sketch, "E727", {"start": v(-4.8, -0.88) * mm, "end": v(-4.82, -0.9) * mm});
            skLineSegment(sketch, "E728", {"start": v(-4.82, -0.9) * mm, "end": v(-4.83, -0.9) * mm});
            skLineSegment(sketch, "E729", {"start": v(-4.83, -0.9) * mm, "end": v(-4.84, -0.91) * mm});
            skLineSegment(sketch, "E730", {"start": v(-4.84, -0.91) * mm, "end": v(-4.86, -0.92) * mm});
            skLineSegment(sketch, "E731", {"start": v(-4.86, -0.92) * mm, "end": v(-4.88, -0.93) * mm});
            skLineSegment(sketch, "E732", {"start": v(-4.88, -0.93) * mm, "end": v(-4.9, -0.95) * mm});
            skLineSegment(sketch, "E733", {"start": v(-4.9, -0.95) * mm, "end": v(-4.9, -0.96) * mm});
            skLineSegment(sketch, "E734", {"start": v(-4.9, -0.96) * mm, "end": v(-4.92, -0.97) * mm});
            skLineSegment(sketch, "E735", {"start": v(-4.92, -0.97) * mm, "end": v(-4.94, -0.98) * mm});
            skLineSegment(sketch, "E736", {"start": v(-4.94, -0.98) * mm, "end": v(-4.95, -1) * mm});
            skLineSegment(sketch, "E737", {"start": v(-4.95, -1) * mm, "end": v(-4.97, -1) * mm});
            skLineSegment(sketch, "E738", {"start": v(-4.97, -1) * mm, "end": v(-4.99, -1.02) * mm});
            skLineSegment(sketch, "E739", {"start": v(-4.99, -1.02) * mm, "end": v(-5, -1.04) * mm});
            skLineSegment(sketch, "E740", {"start": v(-5, -1.04) * mm, "end": v(-5.02, -1.05) * mm});
            skLineSegment(sketch, "E741", {"start": v(-5.02, -1.05) * mm, "end": v(-5.04, -1.07) * mm});
            skLineSegment(sketch, "E742", {"start": v(-5.04, -1.07) * mm, "end": v(-5.05, -1.08) * mm});
            skLineSegment(sketch, "E743", {"start": v(-5.05, -1.08) * mm, "end": v(-5.07, -1.1) * mm});
            skLineSegment(sketch, "E744", {"start": v(-5.07, -1.1) * mm, "end": v(-5.09, -1.11) * mm});
            skLineSegment(sketch, "E745", {"start": v(-5.09, -1.11) * mm, "end": v(-5.1, -1.13) * mm});
            skLineSegment(sketch, "E746", {"start": v(-5.1, -1.13) * mm, "end": v(-5.12, -1.15) * mm});
            skLineSegment(sketch, "E747", {"start": v(-5.12, -1.15) * mm, "end": v(-5.13, -1.17) * mm});
            skLineSegment(sketch, "E748", {"start": v(-5.13, -1.17) * mm, "end": v(-5.1, -1.27) * mm});
            skLineSegment(sketch, "E749", {"start": v(-5.1, -1.27) * mm, "end": v(-5.09, -1.28) * mm});
            skLineSegment(sketch, "E750", {"start": v(-5.09, -1.28) * mm, "end": v(-5.06, -1.3) * mm});
            skLineSegment(sketch, "E751", {"start": v(-5.06, -1.3) * mm, "end": v(-5.04, -1.3) * mm});
            skLineSegment(sketch, "E752", {"start": v(-5.04, -1.3) * mm, "end": v(-5.02, -1.3) * mm});
            skLineSegment(sketch, "E753", {"start": v(-5.02, -1.3) * mm, "end": v(-5, -1.31) * mm});
            skLineSegment(sketch, "E754", {"start": v(-5, -1.31) * mm, "end": v(-4.98, -1.32) * mm});
            skLineSegment(sketch, "E755", {"start": v(-4.98, -1.32) * mm, "end": v(-4.95, -1.32) * mm});
            skLineSegment(sketch, "E756", {"start": v(-4.95, -1.32) * mm, "end": v(-4.93, -1.33) * mm});
            skLineSegment(sketch, "E757", {"start": v(-4.93, -1.33) * mm, "end": v(-4.91, -1.33) * mm});
            skLineSegment(sketch, "E758", {"start": v(-4.91, -1.33) * mm, "end": v(-4.9, -1.34) * mm});
            skLineSegment(sketch, "E759", {"start": v(-4.9, -1.34) * mm, "end": v(-4.87, -1.34) * mm});
            skLineSegment(sketch, "E760", {"start": v(-4.87, -1.34) * mm, "end": v(-4.85, -1.35) * mm});
            skLineSegment(sketch, "E761", {"start": v(-4.85, -1.35) * mm, "end": v(-4.83, -1.35) * mm});
            skLineSegment(sketch, "E762", {"start": v(-4.83, -1.35) * mm, "end": v(-4.81, -1.36) * mm});
            skLineSegment(sketch, "E763", {"start": v(-4.81, -1.36) * mm, "end": v(-4.8, -1.36) * mm});
            skLineSegment(sketch, "E764", {"start": v(-4.8, -1.36) * mm, "end": v(-4.77, -1.36) * mm});
            skLineSegment(sketch, "E765", {"start": v(-4.77, -1.36) * mm, "end": v(-4.75, -1.37) * mm});
            skLineSegment(sketch, "E766", {"start": v(-4.75, -1.37) * mm, "end": v(-4.74, -1.37) * mm});
            skLineSegment(sketch, "E767", {"start": v(-4.74, -1.37) * mm, "end": v(-4.72, -1.37) * mm});
            skLineSegment(sketch, "E768", {"start": v(-4.72, -1.37) * mm, "end": v(-4.7, -1.38) * mm});
            skLineSegment(sketch, "E769", {"start": v(-4.7, -1.38) * mm, "end": v(-4.68, -1.38) * mm});
            skLineSegment(sketch, "E770", {"start": v(-4.68, -1.38) * mm, "end": v(-4.67, -1.38) * mm});
            skLineSegment(sketch, "E771", {"start": v(-4.67, -1.38) * mm, "end": v(-4.65, -1.38) * mm});
            skLineSegment(sketch, "E772", {"start": v(-4.65, -1.38) * mm, "end": v(-4.63, -1.38) * mm});
            skLineSegment(sketch, "E773", {"start": v(-4.63, -1.38) * mm, "end": v(-4.62, -1.39) * mm});
            skLineSegment(sketch, "E774", {"start": v(-4.62, -1.39) * mm, "end": v(-4.6, -1.39) * mm});
            skLineSegment(sketch, "E775", {"start": v(-4.6, -1.39) * mm, "end": v(-4.58, -1.39) * mm});
            skLineSegment(sketch, "E776", {"start": v(-4.58, -1.39) * mm, "end": v(-4.57, -1.4) * mm});
            skLineSegment(sketch, "E777", {"start": v(-4.57, -1.4) * mm, "end": v(-4.55, -1.4) * mm});
            skLineSegment(sketch, "E778", {"start": v(-4.55, -1.4) * mm, "end": v(-4.54, -1.4) * mm});
            skLineSegment(sketch, "E779", {"start": v(-4.54, -1.4) * mm, "end": v(-4.53, -1.4) * mm});
            skLineSegment(sketch, "E780", {"start": v(-4.53, -1.4) * mm, "end": v(-4.52, -1.4) * mm});
            skLineSegment(sketch, "E781", {"start": v(-4.52, -1.4) * mm, "end": v(-4.5, -1.44) * mm});
            skLineSegment(sketch, "E782", {"start": v(-4.5, -1.44) * mm, "end": v(-4.5, -1.46) * mm});
            skLineSegment(sketch, "E783", {"start": v(-4.5, -1.46) * mm, "end": v(-4.48, -1.51) * mm});
            skLineSegment(sketch, "E784", {"start": v(-4.48, -1.51) * mm, "end": v(-4.49, -1.52) * mm});
            skLineSegment(sketch, "E785", {"start": v(-4.49, -1.52) * mm, "end": v(-4.5, -1.53) * mm});
            skLineSegment(sketch, "E786", {"start": v(-4.5, -1.53) * mm, "end": v(-4.5, -1.54) * mm});
            skLineSegment(sketch, "E787", {"start": v(-4.5, -1.54) * mm, "end": v(-4.52, -1.55) * mm});
            skLineSegment(sketch, "E788", {"start": v(-4.52, -1.55) * mm, "end": v(-4.53, -1.56) * mm});
            skLineSegment(sketch, "E789", {"start": v(-4.53, -1.56) * mm, "end": v(-4.54, -1.57) * mm});
            skLineSegment(sketch, "E790", {"start": v(-4.54, -1.57) * mm, "end": v(-4.55, -1.58) * mm});
            skLineSegment(sketch, "E791", {"start": v(-4.55, -1.58) * mm, "end": v(-4.57, -1.59) * mm});
            skLineSegment(sketch, "E792", {"start": v(-4.57, -1.59) * mm, "end": v(-4.58, -1.6) * mm});
            skLineSegment(sketch, "E793", {"start": v(-4.58, -1.6) * mm, "end": v(-4.6, -1.6) * mm});
            skLineSegment(sketch, "E794", {"start": v(-4.6, -1.6) * mm, "end": v(-4.6, -1.62) * mm});
            skLineSegment(sketch, "E795", {"start": v(-4.6, -1.62) * mm, "end": v(-4.62, -1.63) * mm});
            skLineSegment(sketch, "E796", {"start": v(-4.62, -1.63) * mm, "end": v(-4.63, -1.65) * mm});
            skLineSegment(sketch, "E797", {"start": v(-4.63, -1.65) * mm, "end": v(-4.64, -1.66) * mm});
            skLineSegment(sketch, "E798", {"start": v(-4.64, -1.66) * mm, "end": v(-4.66, -1.67) * mm});
            skLineSegment(sketch, "E799", {"start": v(-4.66, -1.67) * mm, "end": v(-4.67, -1.69) * mm});
            skLineSegment(sketch, "E800", {"start": v(-4.67, -1.69) * mm, "end": v(-4.68, -1.7) * mm});
            skLineSegment(sketch, "E801", {"start": v(-4.68, -1.7) * mm, "end": v(-4.7, -1.71) * mm});
            skLineSegment(sketch, "E802", {"start": v(-4.7, -1.71) * mm, "end": v(-4.7, -1.73) * mm});
            skLineSegment(sketch, "E803", {"start": v(-4.7, -1.73) * mm, "end": v(-4.72, -1.74) * mm});
            skLineSegment(sketch, "E804", {"start": v(-4.72, -1.74) * mm, "end": v(-4.74, -1.76) * mm});
            skLineSegment(sketch, "E805", {"start": v(-4.74, -1.76) * mm, "end": v(-4.75, -1.77) * mm});
            skLineSegment(sketch, "E806", {"start": v(-4.75, -1.77) * mm, "end": v(-4.76, -1.8) * mm});
            skLineSegment(sketch, "E807", {"start": v(-4.76, -1.8) * mm, "end": v(-4.78, -1.8) * mm});
            skLineSegment(sketch, "E808", {"start": v(-4.78, -1.8) * mm, "end": v(-4.8, -1.82) * mm});
            skLineSegment(sketch, "E809", {"start": v(-4.8, -1.82) * mm, "end": v(-4.8, -1.84) * mm});
            skLineSegment(sketch, "E810", {"start": v(-4.8, -1.84) * mm, "end": v(-4.82, -1.86) * mm});
            skLineSegment(sketch, "E811", {"start": v(-4.82, -1.86) * mm, "end": v(-4.83, -1.88) * mm});
            skLineSegment(sketch, "E812", {"start": v(-4.83, -1.88) * mm, "end": v(-4.85, -1.9) * mm});
            skLineSegment(sketch, "E813", {"start": v(-4.85, -1.9) * mm, "end": v(-4.86, -1.91) * mm});
            skLineSegment(sketch, "E814", {"start": v(-4.86, -1.91) * mm, "end": v(-4.88, -1.93) * mm});
            skLineSegment(sketch, "E815", {"start": v(-4.88, -1.93) * mm, "end": v(-4.88, -1.96) * mm});
            skLineSegment(sketch, "E816", {"start": v(-4.88, -1.96) * mm, "end": v(-4.84, -2.05) * mm});
            skLineSegment(sketch, "E817", {"start": v(-4.84, -2.05) * mm, "end": v(-4.83, -2.06) * mm});
            skLineSegment(sketch, "E818", {"start": v(-4.83, -2.06) * mm, "end": v(-4.8, -2.07) * mm});
            skLineSegment(sketch, "E819", {"start": v(-4.8, -2.07) * mm, "end": v(-4.78, -2.07) * mm});
            skLineSegment(sketch, "E820", {"start": v(-4.78, -2.07) * mm, "end": v(-4.75, -2.08) * mm});
            skLineSegment(sketch, "E821", {"start": v(-4.75, -2.08) * mm, "end": v(-4.73, -2.08) * mm});
            skLineSegment(sketch, "E822", {"start": v(-4.73, -2.08) * mm, "end": v(-4.7, -2.08) * mm});
            skLineSegment(sketch, "E823", {"start": v(-4.7, -2.08) * mm, "end": v(-4.69, -2.08) * mm});
            skLineSegment(sketch, "E824", {"start": v(-4.69, -2.08) * mm, "end": v(-4.66, -2.08) * mm});
            skLineSegment(sketch, "E825", {"start": v(-4.66, -2.08) * mm, "end": v(-4.64, -2.09) * mm});
            skLineSegment(sketch, "E826", {"start": v(-4.64, -2.09) * mm, "end": v(-4.62, -2.09) * mm});
            skLineSegment(sketch, "E827", {"start": v(-4.62, -2.09) * mm, "end": v(-4.6, -2.09) * mm});
            skLineSegment(sketch, "E828", {"start": v(-4.6, -2.09) * mm, "end": v(-4.58, -2.1) * mm});
            skLineSegment(sketch, "E829", {"start": v(-4.58, -2.1) * mm, "end": v(-4.56, -2.1) * mm});
            skLineSegment(sketch, "E830", {"start": v(-4.56, -2.1) * mm, "end": v(-4.54, -2.1) * mm});
            skLineSegment(sketch, "E831", {"start": v(-4.54, -2.1) * mm, "end": v(-4.52, -2.1) * mm});
            skLineSegment(sketch, "E832", {"start": v(-4.52, -2.1) * mm, "end": v(-4.5, -2.1) * mm});
            skLineSegment(sketch, "E833", {"start": v(-4.5, -2.1) * mm, "end": v(-4.48, -2.1) * mm});
            skLineSegment(sketch, "E834", {"start": v(-4.48, -2.1) * mm, "end": v(-4.46, -2.1) * mm});
            skLineSegment(sketch, "E835", {"start": v(-4.46, -2.1) * mm, "end": v(-4.44, -2.1) * mm});
            skLineSegment(sketch, "E836", {"start": v(-4.44, -2.1) * mm, "end": v(-4.43, -2.1) * mm});
            skLineSegment(sketch, "E837", {"start": v(-4.43, -2.1) * mm, "end": v(-4.4, -2.1) * mm});
            skLineSegment(sketch, "E838", {"start": v(-4.4, -2.1) * mm, "end": v(-4.4, -2.1) * mm});
            skLineSegment(sketch, "E839", {"start": v(-4.4, -2.1) * mm, "end": v(-4.38, -2.1) * mm});
            skLineSegment(sketch, "E840", {"start": v(-4.38, -2.1) * mm, "end": v(-4.36, -2.1) * mm});
            skLineSegment(sketch, "E841", {"start": v(-4.36, -2.1) * mm, "end": v(-4.34, -2.1) * mm});
            skLineSegment(sketch, "E842", {"start": v(-4.34, -2.1) * mm, "end": v(-4.33, -2.1) * mm});
            skLineSegment(sketch, "E843", {"start": v(-4.33, -2.1) * mm, "end": v(-4.31, -2.09) * mm});
            skLineSegment(sketch, "E844", {"start": v(-4.31, -2.09) * mm, "end": v(-4.3, -2.09) * mm});
            skLineSegment(sketch, "E845", {"start": v(-4.3, -2.09) * mm, "end": v(-4.28, -2.09) * mm});
            skLineSegment(sketch, "E846", {"start": v(-4.28, -2.09) * mm, "end": v(-4.27, -2.09) * mm});
            skLineSegment(sketch, "E847", {"start": v(-4.27, -2.09) * mm, "end": v(-4.25, -2.08) * mm});
            skLineSegment(sketch, "E848", {"start": v(-4.25, -2.08) * mm, "end": v(-4.25, -2.08) * mm});
            skLineSegment(sketch, "E849", {"start": v(-4.25, -2.08) * mm, "end": v(-4.22, -2.13) * mm});
            skLineSegment(sketch, "E850", {"start": v(-4.22, -2.13) * mm, "end": v(-4.2, -2.14) * mm});
            skLineSegment(sketch, "E851", {"start": v(-4.2, -2.14) * mm, "end": v(-4.19, -2.2) * mm});
            skLineSegment(sketch, "E852", {"start": v(-4.19, -2.2) * mm, "end": v(-4.2, -2.2) * mm});
            skLineSegment(sketch, "E853", {"start": v(-4.2, -2.2) * mm, "end": v(-4.2, -2.21) * mm});
            skLineSegment(sketch, "E854", {"start": v(-4.2, -2.21) * mm, "end": v(-4.21, -2.22) * mm});
            skLineSegment(sketch, "E855", {"start": v(-4.21, -2.22) * mm, "end": v(-4.22, -2.23) * mm});
            skLineSegment(sketch, "E856", {"start": v(-4.22, -2.23) * mm, "end": v(-4.23, -2.24) * mm});
            skLineSegment(sketch, "E857", {"start": v(-4.23, -2.24) * mm, "end": v(-4.24, -2.26) * mm});
            skLineSegment(sketch, "E858", {"start": v(-4.24, -2.26) * mm, "end": v(-4.25, -2.27) * mm});
            skLineSegment(sketch, "E859", {"start": v(-4.25, -2.27) * mm, "end": v(-4.26, -2.28) * mm});
            skLineSegment(sketch, "E860", {"start": v(-4.26, -2.28) * mm, "end": v(-4.27, -2.3) * mm});
            skLineSegment(sketch, "E861", {"start": v(-4.27, -2.3) * mm, "end": v(-4.28, -2.3) * mm});
            skLineSegment(sketch, "E862", {"start": v(-4.28, -2.3) * mm, "end": v(-4.3, -2.32) * mm});
            skLineSegment(sketch, "E863", {"start": v(-4.3, -2.32) * mm, "end": v(-4.3, -2.34) * mm});
            skLineSegment(sketch, "E864", {"start": v(-4.3, -2.34) * mm, "end": v(-4.32, -2.35) * mm});
            skLineSegment(sketch, "E865", {"start": v(-4.32, -2.35) * mm, "end": v(-4.33, -2.36) * mm});
            skLineSegment(sketch, "E866", {"start": v(-4.33, -2.36) * mm, "end": v(-4.34, -2.38) * mm});
            skLineSegment(sketch, "E867", {"start": v(-4.34, -2.38) * mm, "end": v(-4.35, -2.4) * mm});
            skLineSegment(sketch, "E868", {"start": v(-4.35, -2.4) * mm, "end": v(-4.36, -2.41) * mm});
            skLineSegment(sketch, "E869", {"start": v(-4.36, -2.41) * mm, "end": v(-4.37, -2.43) * mm});
            skLineSegment(sketch, "E870", {"start": v(-4.37, -2.43) * mm, "end": v(-4.38, -2.44) * mm});
            skLineSegment(sketch, "E871", {"start": v(-4.38, -2.44) * mm, "end": v(-4.4, -2.46) * mm});
            skLineSegment(sketch, "E872", {"start": v(-4.4, -2.46) * mm, "end": v(-4.4, -2.48) * mm});
            skLineSegment(sketch, "E873", {"start": v(-4.4, -2.48) * mm, "end": v(-4.41, -2.5) * mm});
            skLineSegment(sketch, "E874", {"start": v(-4.41, -2.5) * mm, "end": v(-4.43, -2.51) * mm});
            skLineSegment(sketch, "E875", {"start": v(-4.43, -2.51) * mm, "end": v(-4.44, -2.53) * mm});
            skLineSegment(sketch, "E876", {"start": v(-4.44, -2.53) * mm, "end": v(-4.45, -2.55) * mm});
            skLineSegment(sketch, "E877", {"start": v(-4.45, -2.55) * mm, "end": v(-4.46, -2.57) * mm});
            skLineSegment(sketch, "E878", {"start": v(-4.46, -2.57) * mm, "end": v(-4.47, -2.59) * mm});
            skLineSegment(sketch, "E879", {"start": v(-4.47, -2.59) * mm, "end": v(-4.48, -2.6) * mm});
            skLineSegment(sketch, "E880", {"start": v(-4.48, -2.6) * mm, "end": v(-4.5, -2.63) * mm});
            skLineSegment(sketch, "E881", {"start": v(-4.5, -2.63) * mm, "end": v(-4.5, -2.65) * mm});
            skLineSegment(sketch, "E882", {"start": v(-4.5, -2.65) * mm, "end": v(-4.52, -2.67) * mm});
            skLineSegment(sketch, "E883", {"start": v(-4.52, -2.67) * mm, "end": v(-4.52, -2.7) * mm});
            skLineSegment(sketch, "E884", {"start": v(-4.52, -2.7) * mm, "end": v(-4.46, -2.79) * mm});
            skLineSegment(sketch, "E885", {"start": v(-4.46, -2.79) * mm, "end": v(-4.44, -2.8) * mm});
            skLineSegment(sketch, "E886", {"start": v(-4.44, -2.8) * mm, "end": v(-4.42, -2.8) * mm});
            skLineSegment(sketch, "E887", {"start": v(-4.42, -2.8) * mm, "end": v(-4.4, -2.8) * mm});
            skLineSegment(sketch, "E888", {"start": v(-4.4, -2.8) * mm, "end": v(-4.37, -2.8) * mm});
            skLineSegment(sketch, "E889", {"start": v(-4.37, -2.8) * mm, "end": v(-4.35, -2.8) * mm});
            skLineSegment(sketch, "E890", {"start": v(-4.35, -2.8) * mm, "end": v(-4.32, -2.8) * mm});
            skLineSegment(sketch, "E891", {"start": v(-4.32, -2.8) * mm, "end": v(-4.3, -2.79) * mm});
            skLineSegment(sketch, "E892", {"start": v(-4.3, -2.79) * mm, "end": v(-4.28, -2.79) * mm});
            skLineSegment(sketch, "E893", {"start": v(-4.28, -2.79) * mm, "end": v(-4.26, -2.79) * mm});
            skLineSegment(sketch, "E894", {"start": v(-4.26, -2.79) * mm, "end": v(-4.24, -2.79) * mm});
            skLineSegment(sketch, "E895", {"start": v(-4.24, -2.79) * mm, "end": v(-4.22, -2.78) * mm});
            skLineSegment(sketch, "E896", {"start": v(-4.22, -2.78) * mm, "end": v(-4.2, -2.78) * mm});
            skLineSegment(sketch, "E897", {"start": v(-4.2, -2.78) * mm, "end": v(-4.18, -2.78) * mm});
            skLineSegment(sketch, "E898", {"start": v(-4.18, -2.78) * mm, "end": v(-4.16, -2.78) * mm});
            skLineSegment(sketch, "E899", {"start": v(-4.16, -2.78) * mm, "end": v(-4.14, -2.77) * mm});
            skLineSegment(sketch, "E900", {"start": v(-4.14, -2.77) * mm, "end": v(-4.12, -2.77) * mm});
            skLineSegment(sketch, "E901", {"start": v(-4.12, -2.77) * mm, "end": v(-4.1, -2.77) * mm});
            skLineSegment(sketch, "E902", {"start": v(-4.1, -2.77) * mm, "end": v(-4.08, -2.77) * mm});
            skLineSegment(sketch, "E903", {"start": v(-4.08, -2.77) * mm, "end": v(-4.06, -2.76) * mm});
            skLineSegment(sketch, "E904", {"start": v(-4.06, -2.76) * mm, "end": v(-4.04, -2.76) * mm});
            skLineSegment(sketch, "E905", {"start": v(-4.04, -2.76) * mm, "end": v(-4.03, -2.76) * mm});
            skLineSegment(sketch, "E906", {"start": v(-4.03, -2.76) * mm, "end": v(-4.01, -2.75) * mm});
            skLineSegment(sketch, "E907", {"start": v(-4.01, -2.75) * mm, "end": v(-4, -2.75) * mm});
            skLineSegment(sketch, "E908", {"start": v(-4, -2.75) * mm, "end": v(-3.98, -2.75) * mm});
            skLineSegment(sketch, "E909", {"start": v(-3.98, -2.75) * mm, "end": v(-3.96, -2.74) * mm});
            skLineSegment(sketch, "E910", {"start": v(-3.96, -2.74) * mm, "end": v(-3.95, -2.74) * mm});
            skLineSegment(sketch, "E911", {"start": v(-3.95, -2.74) * mm, "end": v(-3.93, -2.74) * mm});
            skLineSegment(sketch, "E912", {"start": v(-3.93, -2.74) * mm, "end": v(-3.92, -2.73) * mm});
            skLineSegment(sketch, "E913", {"start": v(-3.92, -2.73) * mm, "end": v(-3.9, -2.73) * mm});
            skLineSegment(sketch, "E914", {"start": v(-3.9, -2.73) * mm, "end": v(-3.89, -2.73) * mm});
            skLineSegment(sketch, "E915", {"start": v(-3.89, -2.73) * mm, "end": v(-3.87, -2.72) * mm});
            skLineSegment(sketch, "E916", {"start": v(-3.87, -2.72) * mm, "end": v(-3.87, -2.72) * mm});
            skLineSegment(sketch, "E917", {"start": v(-3.87, -2.72) * mm, "end": v(-3.83, -2.76) * mm});
            skLineSegment(sketch, "E918", {"start": v(-3.83, -2.76) * mm, "end": v(-3.82, -2.78) * mm});
            skLineSegment(sketch, "E919", {"start": v(-3.82, -2.78) * mm, "end": v(-3.8, -2.82) * mm});
            skLineSegment(sketch, "E920", {"start": v(-3.8, -2.82) * mm, "end": v(-3.8, -2.83) * mm});
            skLineSegment(sketch, "E921", {"start": v(-3.8, -2.83) * mm, "end": v(-3.8, -2.84) * mm});
            skLineSegment(sketch, "E922", {"start": v(-3.8, -2.84) * mm, "end": v(-3.81, -2.85) * mm});
            skLineSegment(sketch, "E923", {"start": v(-3.81, -2.85) * mm, "end": v(-3.82, -2.87) * mm});
            skLineSegment(sketch, "E924", {"start": v(-3.82, -2.87) * mm, "end": v(-3.83, -2.88) * mm});
            skLineSegment(sketch, "E925", {"start": v(-3.83, -2.88) * mm, "end": v(-3.84, -2.9) * mm});
            skLineSegment(sketch, "E926", {"start": v(-3.84, -2.9) * mm, "end": v(-3.84, -2.9) * mm});
            skLineSegment(sketch, "E927", {"start": v(-3.84, -2.9) * mm, "end": v(-3.85, -2.92) * mm});
            skLineSegment(sketch, "E928", {"start": v(-3.85, -2.92) * mm, "end": v(-3.86, -2.93) * mm});
            skLineSegment(sketch, "E929", {"start": v(-3.86, -2.93) * mm, "end": v(-3.87, -2.95) * mm});
            skLineSegment(sketch, "E930", {"start": v(-3.87, -2.95) * mm, "end": v(-3.88, -2.96) * mm});
            skLineSegment(sketch, "E931", {"start": v(-3.88, -2.96) * mm, "end": v(-3.89, -2.98) * mm});
            skLineSegment(sketch, "E932", {"start": v(-3.89, -2.98) * mm, "end": v(-3.9, -3) * mm});
            skLineSegment(sketch, "E933", {"start": v(-3.9, -3) * mm, "end": v(-3.9, -3.01) * mm});
            skLineSegment(sketch, "E934", {"start": v(-3.9, -3.01) * mm, "end": v(-3.91, -3.03) * mm});
            skLineSegment(sketch, "E935", {"start": v(-3.91, -3.03) * mm, "end": v(-3.92, -3.05) * mm});
            skLineSegment(sketch, "E936", {"start": v(-3.92, -3.05) * mm, "end": v(-3.93, -3.06) * mm});
            skLineSegment(sketch, "E937", {"start": v(-3.93, -3.06) * mm, "end": v(-3.94, -3.08) * mm});
            skLineSegment(sketch, "E938", {"start": v(-3.94, -3.08) * mm, "end": v(-3.94, -3.1) * mm});
            skLineSegment(sketch, "E939", {"start": v(-3.94, -3.1) * mm, "end": v(-3.95, -3.12) * mm});
            skLineSegment(sketch, "E940", {"start": v(-3.95, -3.12) * mm, "end": v(-3.96, -3.14) * mm});
            skLineSegment(sketch, "E941", {"start": v(-3.96, -3.14) * mm, "end": v(-3.97, -3.16) * mm});
            skLineSegment(sketch, "E942", {"start": v(-3.97, -3.16) * mm, "end": v(-3.98, -3.17) * mm});
            skLineSegment(sketch, "E943", {"start": v(-3.98, -3.17) * mm, "end": v(-3.99, -3.2) * mm});
            skLineSegment(sketch, "E944", {"start": v(-3.99, -3.2) * mm, "end": v(-4, -3.22) * mm});
            skLineSegment(sketch, "E945", {"start": v(-4, -3.22) * mm, "end": v(-4, -3.24) * mm});
            skLineSegment(sketch, "E946", {"start": v(-4, -3.24) * mm, "end": v(-4.01, -3.26) * mm});
            skLineSegment(sketch, "E947", {"start": v(-4.01, -3.26) * mm, "end": v(-4.02, -3.28) * mm});
            skLineSegment(sketch, "E948", {"start": v(-4.02, -3.28) * mm, "end": v(-4.03, -3.3) * mm});
            skLineSegment(sketch, "E949", {"start": v(-4.03, -3.3) * mm, "end": v(-4.03, -3.32) * mm});
            skLineSegment(sketch, "E950", {"start": v(-4.03, -3.32) * mm, "end": v(-4.04, -3.35) * mm});
            skLineSegment(sketch, "E951", {"start": v(-4.04, -3.35) * mm, "end": v(-4.04, -3.37) * mm});
            skLineSegment(sketch, "E952", {"start": v(-4.04, -3.37) * mm, "end": v(-3.97, -3.45) * mm});
            skLineSegment(sketch, "E953", {"start": v(-3.97, -3.45) * mm, "end": v(-3.95, -3.45) * mm});
            skLineSegment(sketch, "E954", {"start": v(-3.95, -3.45) * mm, "end": v(-3.93, -3.45) * mm});
            skLineSegment(sketch, "E955", {"start": v(-3.93, -3.45) * mm, "end": v(-3.9, -3.45) * mm});
            skLineSegment(sketch, "E956", {"start": v(-3.9, -3.45) * mm, "end": v(-3.88, -3.44) * mm});
            skLineSegment(sketch, "E957", {"start": v(-3.88, -3.44) * mm, "end": v(-3.86, -3.44) * mm});
            skLineSegment(sketch, "E958", {"start": v(-3.86, -3.44) * mm, "end": v(-3.83, -3.43) * mm});
            skLineSegment(sketch, "E959", {"start": v(-3.83, -3.43) * mm, "end": v(-3.81, -3.43) * mm});
            skLineSegment(sketch, "E960", {"start": v(-3.81, -3.43) * mm, "end": v(-3.8, -3.42) * mm});
            skLineSegment(sketch, "E961", {"start": v(-3.8, -3.42) * mm, "end": v(-3.77, -3.42) * mm});
            skLineSegment(sketch, "E962", {"start": v(-3.77, -3.42) * mm, "end": v(-3.75, -3.41) * mm});
            skLineSegment(sketch, "E963", {"start": v(-3.75, -3.41) * mm, "end": v(-3.73, -3.4) * mm});
            skLineSegment(sketch, "E964", {"start": v(-3.73, -3.4) * mm, "end": v(-3.7, -3.4) * mm});
            skLineSegment(sketch, "E965", {"start": v(-3.7, -3.4) * mm, "end": v(-3.69, -3.4) * mm});
            skLineSegment(sketch, "E966", {"start": v(-3.69, -3.4) * mm, "end": v(-3.67, -3.4) * mm});
            skLineSegment(sketch, "E967", {"start": v(-3.67, -3.4) * mm, "end": v(-3.65, -3.39) * mm});
            skLineSegment(sketch, "E968", {"start": v(-3.65, -3.39) * mm, "end": v(-3.63, -3.38) * mm});
            skLineSegment(sketch, "E969", {"start": v(-3.63, -3.38) * mm, "end": v(-3.62, -3.38) * mm});
            skLineSegment(sketch, "E970", {"start": v(-3.62, -3.38) * mm, "end": v(-3.6, -3.37) * mm});
            skLineSegment(sketch, "E971", {"start": v(-3.6, -3.37) * mm, "end": v(-3.58, -3.37) * mm});
            skLineSegment(sketch, "E972", {"start": v(-3.58, -3.37) * mm, "end": v(-3.56, -3.36) * mm});
            skLineSegment(sketch, "E973", {"start": v(-3.56, -3.36) * mm, "end": v(-3.55, -3.35) * mm});
            skLineSegment(sketch, "E974", {"start": v(-3.55, -3.35) * mm, "end": v(-3.53, -3.35) * mm});
            skLineSegment(sketch, "E975", {"start": v(-3.53, -3.35) * mm, "end": v(-3.51, -3.34) * mm});
            skLineSegment(sketch, "E976", {"start": v(-3.51, -3.34) * mm, "end": v(-3.5, -3.34) * mm});
            skLineSegment(sketch, "E977", {"start": v(-3.5, -3.34) * mm, "end": v(-3.48, -3.33) * mm});
            skLineSegment(sketch, "E978", {"start": v(-3.48, -3.33) * mm, "end": v(-3.47, -3.32) * mm});
            skLineSegment(sketch, "E979", {"start": v(-3.47, -3.32) * mm, "end": v(-3.45, -3.32) * mm});
            skLineSegment(sketch, "E980", {"start": v(-3.45, -3.32) * mm, "end": v(-3.44, -3.31) * mm});
            skLineSegment(sketch, "E981", {"start": v(-3.44, -3.31) * mm, "end": v(-3.43, -3.3) * mm});
            skLineSegment(sketch, "E982", {"start": v(-3.43, -3.3) * mm, "end": v(-3.41, -3.3) * mm});
            skLineSegment(sketch, "E983", {"start": v(-3.41, -3.3) * mm, "end": v(-3.4, -3.3) * mm});
            skLineSegment(sketch, "E984", {"start": v(-3.4, -3.3) * mm, "end": v(-3.4, -3.3) * mm});
            skLineSegment(sketch, "E985", {"start": v(-3.4, -3.3) * mm, "end": v(-3.35, -3.33) * mm});
            skLineSegment(sketch, "E986", {"start": v(-3.35, -3.33) * mm, "end": v(-3.34, -3.34) * mm});
            skLineSegment(sketch, "E987", {"start": v(-3.34, -3.34) * mm, "end": v(-3.3, -3.38) * mm});
            skLineSegment(sketch, "E988", {"start": v(-3.3, -3.38) * mm, "end": v(-3.3, -3.39) * mm});
            skLineSegment(sketch, "E989", {"start": v(-3.3, -3.39) * mm, "end": v(-3.31, -3.4) * mm});
            skLineSegment(sketch, "E990", {"start": v(-3.31, -3.4) * mm, "end": v(-3.32, -3.41) * mm});
            skLineSegment(sketch, "E991", {"start": v(-3.32, -3.41) * mm, "end": v(-3.33, -3.43) * mm});
            skLineSegment(sketch, "E992", {"start": v(-3.33, -3.43) * mm, "end": v(-3.33, -3.44) * mm});
            skLineSegment(sketch, "E993", {"start": v(-3.33, -3.44) * mm, "end": v(-3.34, -3.46) * mm});
            skLineSegment(sketch, "E994", {"start": v(-3.34, -3.46) * mm, "end": v(-3.34, -3.47) * mm});
            skLineSegment(sketch, "E995", {"start": v(-3.34, -3.47) * mm, "end": v(-3.35, -3.49) * mm});
            skLineSegment(sketch, "E996", {"start": v(-3.35, -3.49) * mm, "end": v(-3.35, -3.5) * mm});
            skLineSegment(sketch, "E997", {"start": v(-3.35, -3.5) * mm, "end": v(-3.36, -3.52) * mm});
            skLineSegment(sketch, "E998", {"start": v(-3.36, -3.52) * mm, "end": v(-3.37, -3.53) * mm});
            skLineSegment(sketch, "E999", {"start": v(-3.37, -3.53) * mm, "end": v(-3.37, -3.55) * mm});
            skLineSegment(sketch, "E1000", {"start": v(-3.37, -3.55) * mm, "end": v(-3.38, -3.57) * mm});
            skLineSegment(sketch, "E1001", {"start": v(-3.38, -3.57) * mm, "end": v(-3.38, -3.59) * mm});
            skLineSegment(sketch, "E1002", {"start": v(-3.38, -3.59) * mm, "end": v(-3.39, -3.6) * mm});
            skLineSegment(sketch, "E1003", {"start": v(-3.39, -3.6) * mm, "end": v(-3.4, -3.62) * mm});
            skLineSegment(sketch, "E1004", {"start": v(-3.4, -3.62) * mm, "end": v(-3.4, -3.64) * mm});
            skLineSegment(sketch, "E1005", {"start": v(-3.4, -3.64) * mm, "end": v(-3.4, -3.66) * mm});
            skLineSegment(sketch, "E1006", {"start": v(-3.4, -3.66) * mm, "end": v(-3.41, -3.68) * mm});
            skLineSegment(sketch, "E1007", {"start": v(-3.41, -3.68) * mm, "end": v(-3.42, -3.7) * mm});
            skLineSegment(sketch, "E1008", {"start": v(-3.42, -3.7) * mm, "end": v(-3.42, -3.72) * mm});
            skLineSegment(sketch, "E1009", {"start": v(-3.42, -3.72) * mm, "end": v(-3.43, -3.74) * mm});
            skLineSegment(sketch, "E1010", {"start": v(-3.43, -3.74) * mm, "end": v(-3.43, -3.76) * mm});
            skLineSegment(sketch, "E1011", {"start": v(-3.43, -3.76) * mm, "end": v(-3.44, -3.78) * mm});
            skLineSegment(sketch, "E1012", {"start": v(-3.44, -3.78) * mm, "end": v(-3.44, -3.8) * mm});
            skLineSegment(sketch, "E1013", {"start": v(-3.44, -3.8) * mm, "end": v(-3.45, -3.82) * mm});
            skLineSegment(sketch, "E1014", {"start": v(-3.45, -3.82) * mm, "end": v(-3.45, -3.84) * mm});
            skLineSegment(sketch, "E1015", {"start": v(-3.45, -3.84) * mm, "end": v(-3.46, -3.87) * mm});
            skLineSegment(sketch, "E1016", {"start": v(-3.46, -3.87) * mm, "end": v(-3.46, -3.89) * mm});
            skLineSegment(sketch, "E1017", {"start": v(-3.46, -3.89) * mm, "end": v(-3.46, -3.91) * mm});
            skLineSegment(sketch, "E1018", {"start": v(-3.46, -3.91) * mm, "end": v(-3.47, -3.94) * mm});
            skLineSegment(sketch, "E1019", {"start": v(-3.47, -3.94) * mm, "end": v(-3.46, -3.96) * mm});
            skLineSegment(sketch, "E1020", {"start": v(-3.46, -3.96) * mm, "end": v(-3.38, -4.03) * mm});
            skLineSegment(sketch, "E1021", {"start": v(-3.38, -4.03) * mm, "end": v(-3.36, -4.03) * mm});
            skLineSegment(sketch, "E1022", {"start": v(-3.36, -4.03) * mm, "end": v(-3.34, -4.02) * mm});
            skLineSegment(sketch, "E1023", {"start": v(-3.34, -4.02) * mm, "end": v(-3.32, -4.01) * mm});
            skLineSegment(sketch, "E1024", {"start": v(-3.32, -4.01) * mm, "end": v(-3.3, -4) * mm});
            skLineSegment(sketch, "E1025", {"start": v(-3.3, -4) * mm, "end": v(-3.27, -4) * mm});
            skLineSegment(sketch, "E1026", {"start": v(-3.27, -4) * mm, "end": v(-3.25, -4) * mm});
            skLineSegment(sketch, "E1027", {"start": v(-3.25, -4) * mm, "end": v(-3.23, -3.98) * mm});
            skLineSegment(sketch, "E1028", {"start": v(-3.23, -3.98) * mm, "end": v(-3.2, -3.97) * mm});
            skLineSegment(sketch, "E1029", {"start": v(-3.2, -3.97) * mm, "end": v(-3.19, -3.97) * mm});
            skLineSegment(sketch, "E1030", {"start": v(-3.19, -3.97) * mm, "end": v(-3.17, -3.96) * mm});
            skLineSegment(sketch, "E1031", {"start": v(-3.17, -3.96) * mm, "end": v(-3.15, -3.95) * mm});
            skLineSegment(sketch, "E1032", {"start": v(-3.15, -3.95) * mm, "end": v(-3.13, -3.94) * mm});
            skLineSegment(sketch, "E1033", {"start": v(-3.13, -3.94) * mm, "end": v(-3.11, -3.93) * mm});
            skLineSegment(sketch, "E1034", {"start": v(-3.11, -3.93) * mm, "end": v(-3.1, -3.93) * mm});
            skLineSegment(sketch, "E1035", {"start": v(-3.1, -3.93) * mm, "end": v(-3.08, -3.92) * mm});
            skLineSegment(sketch, "E1036", {"start": v(-3.08, -3.92) * mm, "end": v(-3.06, -3.9) * mm});
            skLineSegment(sketch, "E1037", {"start": v(-3.06, -3.9) * mm, "end": v(-3.04, -3.9) * mm});
            skLineSegment(sketch, "E1038", {"start": v(-3.04, -3.9) * mm, "end": v(-3.03, -3.9) * mm});
            skLineSegment(sketch, "E1039", {"start": v(-3.03, -3.9) * mm, "end": v(-3, -3.88) * mm});
            skLineSegment(sketch, "E1040", {"start": v(-3, -3.88) * mm, "end": v(-3, -3.88) * mm});
            skLineSegment(sketch, "E1041", {"start": v(-3, -3.88) * mm, "end": v(-2.98, -3.87) * mm});
            skLineSegment(sketch, "E1042", {"start": v(-2.98, -3.87) * mm, "end": v(-2.96, -3.86) * mm});
            skLineSegment(sketch, "E1043", {"start": v(-2.96, -3.86) * mm, "end": v(-2.95, -3.85) * mm});
            skLineSegment(sketch, "E1044", {"start": v(-2.95, -3.85) * mm, "end": v(-2.93, -3.84) * mm});
            skLineSegment(sketch, "E1045", {"start": v(-2.93, -3.84) * mm, "end": v(-2.92, -3.83) * mm});
            skLineSegment(sketch, "E1046", {"start": v(-2.92, -3.83) * mm, "end": v(-2.9, -3.83) * mm});
            skLineSegment(sketch, "E1047", {"start": v(-2.9, -3.83) * mm, "end": v(-2.9, -3.82) * mm});
            skLineSegment(sketch, "E1048", {"start": v(-2.9, -3.82) * mm, "end": v(-2.88, -3.81) * mm});
            skLineSegment(sketch, "E1049", {"start": v(-2.88, -3.81) * mm, "end": v(-2.87, -3.8) * mm});
            skLineSegment(sketch, "E1050", {"start": v(-2.87, -3.8) * mm, "end": v(-2.86, -3.8) * mm});
            skLineSegment(sketch, "E1051", {"start": v(-2.86, -3.8) * mm, "end": v(-2.84, -3.79) * mm});
            skLineSegment(sketch, "E1052", {"start": v(-2.84, -3.79) * mm, "end": v(-2.84, -3.78) * mm});
            skLineSegment(sketch, "E1053", {"start": v(-2.84, -3.78) * mm, "end": v(-2.79, -3.81) * mm});
            skLineSegment(sketch, "E1054", {"start": v(-2.79, -3.81) * mm, "end": v(-2.78, -3.82) * mm});
            skLineSegment(sketch, "E1055", {"start": v(-2.78, -3.82) * mm, "end": v(-2.74, -3.86) * mm});
            skLineSegment(sketch, "E1056", {"start": v(-2.74, -3.86) * mm, "end": v(-2.74, -3.86) * mm});
            skLineSegment(sketch, "E1057", {"start": v(-2.74, -3.86) * mm, "end": v(-2.74, -3.88) * mm});
            skLineSegment(sketch, "E1058", {"start": v(-2.74, -3.88) * mm, "end": v(-2.74, -3.9) * mm});
            skLineSegment(sketch, "E1059", {"start": v(-2.74, -3.9) * mm, "end": v(-2.75, -3.9) * mm});
            skLineSegment(sketch, "E1060", {"start": v(-2.75, -3.9) * mm, "end": v(-2.75, -3.92) * mm});
            skLineSegment(sketch, "E1061", {"start": v(-2.75, -3.92) * mm, "end": v(-2.76, -3.94) * mm});
            skLineSegment(sketch, "E1062", {"start": v(-2.76, -3.94) * mm, "end": v(-2.76, -3.95) * mm});
            skLineSegment(sketch, "E1063", {"start": v(-2.76, -3.95) * mm, "end": v(-2.76, -3.97) * mm});
            skLineSegment(sketch, "E1064", {"start": v(-2.76, -3.97) * mm, "end": v(-2.77, -3.98) * mm});
            skLineSegment(sketch, "E1065", {"start": v(-2.77, -3.98) * mm, "end": v(-2.77, -4) * mm});
            skLineSegment(sketch, "E1066", {"start": v(-2.77, -4) * mm, "end": v(-2.77, -4.02) * mm});
            skLineSegment(sketch, "E1067", {"start": v(-2.77, -4.02) * mm, "end": v(-2.78, -4.03) * mm});
            skLineSegment(sketch, "E1068", {"start": v(-2.78, -4.03) * mm, "end": v(-2.78, -4.05) * mm});
            skLineSegment(sketch, "E1069", {"start": v(-2.78, -4.05) * mm, "end": v(-2.78, -4.07) * mm});
            skLineSegment(sketch, "E1070", {"start": v(-2.78, -4.07) * mm, "end": v(-2.78, -4.09) * mm});
            skLineSegment(sketch, "E1071", {"start": v(-2.78, -4.09) * mm, "end": v(-2.79, -4.1) * mm});
            skLineSegment(sketch, "E1072", {"start": v(-2.79, -4.1) * mm, "end": v(-2.79, -4.13) * mm});
            skLineSegment(sketch, "E1073", {"start": v(-2.79, -4.13) * mm, "end": v(-2.8, -4.15) * mm});
            skLineSegment(sketch, "E1074", {"start": v(-2.8, -4.15) * mm, "end": v(-2.8, -4.17) * mm});
            skLineSegment(sketch, "E1075", {"start": v(-2.8, -4.17) * mm, "end": v(-2.8, -4.19) * mm});
            skLineSegment(sketch, "E1076", {"start": v(-2.8, -4.19) * mm, "end": v(-2.8, -4.2) * mm});
            skLineSegment(sketch, "E1077", {"start": v(-2.8, -4.2) * mm, "end": v(-2.8, -4.23) * mm});
            skLineSegment(sketch, "E1078", {"start": v(-2.8, -4.23) * mm, "end": v(-2.8, -4.25) * mm});
            skLineSegment(sketch, "E1079", {"start": v(-2.8, -4.25) * mm, "end": v(-2.8, -4.27) * mm});
            skLineSegment(sketch, "E1080", {"start": v(-2.8, -4.27) * mm, "end": v(-2.8, -4.3) * mm});
            skLineSegment(sketch, "E1081", {"start": v(-2.8, -4.3) * mm, "end": v(-2.8, -4.31) * mm});
            skLineSegment(sketch, "E1082", {"start": v(-2.8, -4.31) * mm, "end": v(-2.8, -4.34) * mm});
            skLineSegment(sketch, "E1083", {"start": v(-2.8, -4.34) * mm, "end": v(-2.8, -4.36) * mm});
            skLineSegment(sketch, "E1084", {"start": v(-2.8, -4.36) * mm, "end": v(-2.8, -4.38) * mm});
            skLineSegment(sketch, "E1085", {"start": v(-2.8, -4.38) * mm, "end": v(-2.8, -4.4) * mm});
            skLineSegment(sketch, "E1086", {"start": v(-2.8, -4.4) * mm, "end": v(-2.8, -4.43) * mm});
            skLineSegment(sketch, "E1087", {"start": v(-2.8, -4.43) * mm, "end": v(-2.8, -4.45) * mm});
            skLineSegment(sketch, "E1088", {"start": v(-2.8, -4.45) * mm, "end": v(-2.71, -4.5) * mm});
            skLineSegment(sketch, "E1089", {"start": v(-2.71, -4.5) * mm, "end": v(-2.7, -4.5) * mm});
            skLineSegment(sketch, "E1090", {"start": v(-2.7, -4.5) * mm, "end": v(-2.67, -4.5) * mm});
            skLineSegment(sketch, "E1091", {"start": v(-2.67, -4.5) * mm, "end": v(-2.65, -4.48) * mm});
            skLineSegment(sketch, "E1092", {"start": v(-2.65, -4.48) * mm, "end": v(-2.63, -4.47) * mm});
            skLineSegment(sketch, "E1093", {"start": v(-2.63, -4.47) * mm, "end": v(-2.6, -4.46) * mm});
            skLineSegment(sketch, "E1094", {"start": v(-2.6, -4.46) * mm, "end": v(-2.59, -4.45) * mm});
            skLineSegment(sketch, "E1095", {"start": v(-2.59, -4.45) * mm, "end": v(-2.57, -4.44) * mm});
            skLineSegment(sketch, "E1096", {"start": v(-2.57, -4.44) * mm, "end": v(-2.55, -4.43) * mm});
            skLineSegment(sketch, "E1097", {"start": v(-2.55, -4.43) * mm, "end": v(-2.53, -4.42) * mm});
            skLineSegment(sketch, "E1098", {"start": v(-2.53, -4.42) * mm, "end": v(-2.51, -4.4) * mm});
            skLineSegment(sketch, "E1099", {"start": v(-2.51, -4.4) * mm, "end": v(-2.5, -4.4) * mm});
            skLineSegment(sketch, "E1100", {"start": v(-2.5, -4.4) * mm, "end": v(-2.48, -4.38) * mm});
            skLineSegment(sketch, "E1101", {"start": v(-2.48, -4.38) * mm, "end": v(-2.46, -4.37) * mm});
            skLineSegment(sketch, "E1102", {"start": v(-2.46, -4.37) * mm, "end": v(-2.44, -4.36) * mm});
            skLineSegment(sketch, "E1103", {"start": v(-2.44, -4.36) * mm, "end": v(-2.43, -4.35) * mm});
            skLineSegment(sketch, "E1104", {"start": v(-2.43, -4.35) * mm, "end": v(-2.41, -4.34) * mm});
            skLineSegment(sketch, "E1105", {"start": v(-2.41, -4.34) * mm, "end": v(-2.4, -4.33) * mm});
            skLineSegment(sketch, "E1106", {"start": v(-2.4, -4.33) * mm, "end": v(-2.38, -4.32) * mm});
            skLineSegment(sketch, "E1107", {"start": v(-2.38, -4.32) * mm, "end": v(-2.36, -4.3) * mm});
            skLineSegment(sketch, "E1108", {"start": v(-2.36, -4.3) * mm, "end": v(-2.35, -4.3) * mm});
            skLineSegment(sketch, "E1109", {"start": v(-2.35, -4.3) * mm, "end": v(-2.34, -4.29) * mm});
            skLineSegment(sketch, "E1110", {"start": v(-2.34, -4.29) * mm, "end": v(-2.32, -4.27) * mm});
            skLineSegment(sketch, "E1111", {"start": v(-2.32, -4.27) * mm, "end": v(-2.3, -4.26) * mm});
            skLineSegment(sketch, "E1112", {"start": v(-2.3, -4.26) * mm, "end": v(-2.3, -4.25) * mm});
            skLineSegment(sketch, "E1113", {"start": v(-2.3, -4.25) * mm, "end": v(-2.28, -4.24) * mm});
            skLineSegment(sketch, "E1114", {"start": v(-2.28, -4.24) * mm, "end": v(-2.27, -4.23) * mm});
            skLineSegment(sketch, "E1115", {"start": v(-2.27, -4.23) * mm, "end": v(-2.26, -4.22) * mm});
            skLineSegment(sketch, "E1116", {"start": v(-2.26, -4.22) * mm, "end": v(-2.25, -4.21) * mm});
            skLineSegment(sketch, "E1117", {"start": v(-2.25, -4.21) * mm, "end": v(-2.24, -4.2) * mm});
            skLineSegment(sketch, "E1118", {"start": v(-2.24, -4.2) * mm, "end": v(-2.23, -4.2) * mm});
            skLineSegment(sketch, "E1119", {"start": v(-2.23, -4.2) * mm, "end": v(-2.22, -4.18) * mm});
            skLineSegment(sketch, "E1120", {"start": v(-2.22, -4.18) * mm, "end": v(-2.21, -4.18) * mm});
            skLineSegment(sketch, "E1121", {"start": v(-2.21, -4.18) * mm, "end": v(-2.16, -4.2) * mm});
            skLineSegment(sketch, "E1122", {"start": v(-2.16, -4.2) * mm, "end": v(-2.15, -4.2) * mm});
            skLineSegment(sketch, "E1123", {"start": v(-2.15, -4.2) * mm, "end": v(-2.1, -4.24) * mm});
            skLineSegment(sketch, "E1124", {"start": v(-2.1, -4.24) * mm, "end": v(-2.1, -4.24) * mm});
            skLineSegment(sketch, "E1125", {"start": v(-2.1, -4.24) * mm, "end": v(-2.1, -4.26) * mm});
            skLineSegment(sketch, "E1126", {"start": v(-2.1, -4.26) * mm, "end": v(-2.1, -4.27) * mm});
            skLineSegment(sketch, "E1127", {"start": v(-2.1, -4.27) * mm, "end": v(-2.1, -4.29) * mm});
            skLineSegment(sketch, "E1128", {"start": v(-2.1, -4.29) * mm, "end": v(-2.1, -4.3) * mm});
            skLineSegment(sketch, "E1129", {"start": v(-2.1, -4.3) * mm, "end": v(-2.1, -4.32) * mm});
            skLineSegment(sketch, "E1130", {"start": v(-2.1, -4.32) * mm, "end": v(-2.1, -4.33) * mm});
            skLineSegment(sketch, "E1131", {"start": v(-2.1, -4.33) * mm, "end": v(-2.1, -4.35) * mm});
            skLineSegment(sketch, "E1132", {"start": v(-2.1, -4.35) * mm, "end": v(-2.1, -4.37) * mm});
            skLineSegment(sketch, "E1133", {"start": v(-2.1, -4.37) * mm, "end": v(-2.1, -4.38) * mm});
            skLineSegment(sketch, "E1134", {"start": v(-2.1, -4.38) * mm, "end": v(-2.1, -4.4) * mm});
            skLineSegment(sketch, "E1135", {"start": v(-2.1, -4.4) * mm, "end": v(-2.1, -4.42) * mm});
            skLineSegment(sketch, "E1136", {"start": v(-2.1, -4.42) * mm, "end": v(-2.11, -4.44) * mm});
            skLineSegment(sketch, "E1137", {"start": v(-2.11, -4.44) * mm, "end": v(-2.11, -4.46) * mm});
            skLineSegment(sketch, "E1138", {"start": v(-2.11, -4.46) * mm, "end": v(-2.11, -4.47) * mm});
            skLineSegment(sketch, "E1139", {"start": v(-2.11, -4.47) * mm, "end": v(-2.1, -4.5) * mm});
            skLineSegment(sketch, "E1140", {"start": v(-2.1, -4.5) * mm, "end": v(-2.1, -4.51) * mm});
            skLineSegment(sketch, "E1141", {"start": v(-2.1, -4.51) * mm, "end": v(-2.1, -4.53) * mm});
            skLineSegment(sketch, "E1142", {"start": v(-2.1, -4.53) * mm, "end": v(-2.1, -4.55) * mm});
            skLineSegment(sketch, "E1143", {"start": v(-2.1, -4.55) * mm, "end": v(-2.1, -4.57) * mm});
            skLineSegment(sketch, "E1144", {"start": v(-2.1, -4.57) * mm, "end": v(-2.1, -4.6) * mm});
            skLineSegment(sketch, "E1145", {"start": v(-2.1, -4.6) * mm, "end": v(-2.1, -4.61) * mm});
            skLineSegment(sketch, "E1146", {"start": v(-2.1, -4.61) * mm, "end": v(-2.1, -4.63) * mm});
            skLineSegment(sketch, "E1147", {"start": v(-2.1, -4.63) * mm, "end": v(-2.1, -4.66) * mm});
            skLineSegment(sketch, "E1148", {"start": v(-2.1, -4.66) * mm, "end": v(-2.1, -4.68) * mm});
            skLineSegment(sketch, "E1149", {"start": v(-2.1, -4.68) * mm, "end": v(-2.1, -4.7) * mm});
            skLineSegment(sketch, "E1150", {"start": v(-2.1, -4.7) * mm, "end": v(-2.1, -4.72) * mm});
            skLineSegment(sketch, "E1151", {"start": v(-2.1, -4.72) * mm, "end": v(-2.1, -4.75) * mm});
            skLineSegment(sketch, "E1152", {"start": v(-2.1, -4.75) * mm, "end": v(-2.09, -4.77) * mm});
            skLineSegment(sketch, "E1153", {"start": v(-2.09, -4.77) * mm, "end": v(-2.09, -4.8) * mm});
            skLineSegment(sketch, "E1154", {"start": v(-2.09, -4.8) * mm, "end": v(-2.08, -4.82) * mm});
            skLineSegment(sketch, "E1155", {"start": v(-2.08, -4.82) * mm, "end": v(-2.07, -4.84) * mm});
            skLineSegment(sketch, "E1156", {"start": v(-2.07, -4.84) * mm, "end": v(-1.97, -4.88) * mm});
            skLineSegment(sketch, "E1157", {"start": v(-1.97, -4.88) * mm, "end": v(-1.95, -4.87) * mm});
            skLineSegment(sketch, "E1158", {"start": v(-1.95, -4.87) * mm, "end": v(-1.93, -4.86) * mm});
            skLineSegment(sketch, "E1159", {"start": v(-1.93, -4.86) * mm, "end": v(-1.91, -4.84) * mm});
            skLineSegment(sketch, "E1160", {"start": v(-1.91, -4.84) * mm, "end": v(-1.9, -4.83) * mm});
            skLineSegment(sketch, "E1161", {"start": v(-1.9, -4.83) * mm, "end": v(-1.88, -4.81) * mm});
            skLineSegment(sketch, "E1162", {"start": v(-1.88, -4.81) * mm, "end": v(-1.86, -4.8) * mm});
            skLineSegment(sketch, "E1163", {"start": v(-1.86, -4.8) * mm, "end": v(-1.84, -4.79) * mm});
            skLineSegment(sketch, "E1164", {"start": v(-1.84, -4.79) * mm, "end": v(-1.82, -4.77) * mm});
            skLineSegment(sketch, "E1165", {"start": v(-1.82, -4.77) * mm, "end": v(-1.8, -4.76) * mm});
            skLineSegment(sketch, "E1166", {"start": v(-1.8, -4.76) * mm, "end": v(-1.8, -4.74) * mm});
            skLineSegment(sketch, "E1167", {"start": v(-1.8, -4.74) * mm, "end": v(-1.78, -4.73) * mm});
            skLineSegment(sketch, "E1168", {"start": v(-1.78, -4.73) * mm, "end": v(-1.76, -4.72) * mm});
            skLineSegment(sketch, "E1169", {"start": v(-1.76, -4.72) * mm, "end": v(-1.74, -4.7) * mm});
            skLineSegment(sketch, "E1170", {"start": v(-1.74, -4.7) * mm, "end": v(-1.73, -4.69) * mm});
            skLineSegment(sketch, "E1171", {"start": v(-1.73, -4.69) * mm, "end": v(-1.72, -4.68) * mm});
            skLineSegment(sketch, "E1172", {"start": v(-1.72, -4.68) * mm, "end": v(-1.7, -4.66) * mm});
            skLineSegment(sketch, "E1173", {"start": v(-1.7, -4.66) * mm, "end": v(-1.69, -4.65) * mm});
            skLineSegment(sketch, "E1174", {"start": v(-1.69, -4.65) * mm, "end": v(-1.68, -4.64) * mm});
            skLineSegment(sketch, "E1175", {"start": v(-1.68, -4.64) * mm, "end": v(-1.66, -4.62) * mm});
            skLineSegment(sketch, "E1176", {"start": v(-1.66, -4.62) * mm, "end": v(-1.65, -4.61) * mm});
            skLineSegment(sketch, "E1177", {"start": v(-1.65, -4.61) * mm, "end": v(-1.64, -4.6) * mm});
            skLineSegment(sketch, "E1178", {"start": v(-1.64, -4.6) * mm, "end": v(-1.63, -4.59) * mm});
            skLineSegment(sketch, "E1179", {"start": v(-1.63, -4.59) * mm, "end": v(-1.61, -4.57) * mm});
            skLineSegment(sketch, "E1180", {"start": v(-1.61, -4.57) * mm, "end": v(-1.6, -4.56) * mm});
            skLineSegment(sketch, "E1181", {"start": v(-1.6, -4.56) * mm, "end": v(-1.6, -4.55) * mm});
            skLineSegment(sketch, "E1182", {"start": v(-1.6, -4.55) * mm, "end": v(-1.58, -4.54) * mm});
            skLineSegment(sketch, "E1183", {"start": v(-1.58, -4.54) * mm, "end": v(-1.57, -4.53) * mm});
            skLineSegment(sketch, "E1184", {"start": v(-1.57, -4.53) * mm, "end": v(-1.56, -4.51) * mm});
            skLineSegment(sketch, "E1185", {"start": v(-1.56, -4.51) * mm, "end": v(-1.55, -4.5) * mm});
            skLineSegment(sketch, "E1186", {"start": v(-1.55, -4.5) * mm, "end": v(-1.54, -4.5) * mm});
            skLineSegment(sketch, "E1187", {"start": v(-1.54, -4.5) * mm, "end": v(-1.53, -4.48) * mm});
            skLineSegment(sketch, "E1188", {"start": v(-1.53, -4.48) * mm, "end": v(-1.53, -4.47) * mm});
            skLineSegment(sketch, "E1189", {"start": v(-1.53, -4.47) * mm, "end": v(-1.47, -4.49) * mm});
            skLineSegment(sketch, "E1190", {"start": v(-1.47, -4.49) * mm, "end": v(-1.46, -4.5) * mm});
            skLineSegment(sketch, "E1191", {"start": v(-1.46, -4.5) * mm, "end": v(-1.4, -4.51) * mm});
            skLineSegment(sketch, "E1192", {"start": v(-1.4, -4.51) * mm, "end": v(-1.4, -4.52) * mm});
            skLineSegment(sketch, "E1193", {"start": v(-1.4, -4.52) * mm, "end": v(-1.4, -4.53) * mm});
            skLineSegment(sketch, "E1194", {"start": v(-1.4, -4.53) * mm, "end": v(-1.4, -4.55) * mm});
            skLineSegment(sketch, "E1195", {"start": v(-1.4, -4.55) * mm, "end": v(-1.4, -4.56) * mm});
            skLineSegment(sketch, "E1196", {"start": v(-1.4, -4.56) * mm, "end": v(-1.4, -4.58) * mm});
            skLineSegment(sketch, "E1197", {"start": v(-1.4, -4.58) * mm, "end": v(-1.4, -4.6) * mm});
            skLineSegment(sketch, "E1198", {"start": v(-1.4, -4.6) * mm, "end": v(-1.4, -4.61) * mm});
            skLineSegment(sketch, "E1199", {"start": v(-1.4, -4.61) * mm, "end": v(-1.4, -4.63) * mm});
            skLineSegment(sketch, "E1200", {"start": v(-1.4, -4.63) * mm, "end": v(-1.4, -4.64) * mm});
            skLineSegment(sketch, "E1201", {"start": v(-1.4, -4.64) * mm, "end": v(-1.4, -4.66) * mm});
            skLineSegment(sketch, "E1202", {"start": v(-1.4, -4.66) * mm, "end": v(-1.4, -4.68) * mm});
            skLineSegment(sketch, "E1203", {"start": v(-1.4, -4.68) * mm, "end": v(-1.4, -4.7) * mm});
            skLineSegment(sketch, "E1204", {"start": v(-1.4, -4.7) * mm, "end": v(-1.4, -4.71) * mm});
            skLineSegment(sketch, "E1205", {"start": v(-1.4, -4.71) * mm, "end": v(-1.39, -4.73) * mm});
            skLineSegment(sketch, "E1206", {"start": v(-1.39, -4.73) * mm, "end": v(-1.38, -4.75) * mm});
            skLineSegment(sketch, "E1207", {"start": v(-1.38, -4.75) * mm, "end": v(-1.38, -4.77) * mm});
            skLineSegment(sketch, "E1208", {"start": v(-1.38, -4.77) * mm, "end": v(-1.38, -4.79) * mm});
            skLineSegment(sketch, "E1209", {"start": v(-1.38, -4.79) * mm, "end": v(-1.37, -4.8) * mm});
            skLineSegment(sketch, "E1210", {"start": v(-1.37, -4.8) * mm, "end": v(-1.37, -4.82) * mm});
            skLineSegment(sketch, "E1211", {"start": v(-1.37, -4.82) * mm, "end": v(-1.37, -4.84) * mm});
            skLineSegment(sketch, "E1212", {"start": v(-1.37, -4.84) * mm, "end": v(-1.36, -4.86) * mm});
            skLineSegment(sketch, "E1213", {"start": v(-1.36, -4.86) * mm, "end": v(-1.36, -4.89) * mm});
            skLineSegment(sketch, "E1214", {"start": v(-1.36, -4.89) * mm, "end": v(-1.35, -4.9) * mm});
            skLineSegment(sketch, "E1215", {"start": v(-1.35, -4.9) * mm, "end": v(-1.35, -4.93) * mm});
            skLineSegment(sketch, "E1216", {"start": v(-1.35, -4.93) * mm, "end": v(-1.34, -4.95) * mm});
            skLineSegment(sketch, "E1217", {"start": v(-1.34, -4.95) * mm, "end": v(-1.34, -4.97) * mm});
            skLineSegment(sketch, "E1218", {"start": v(-1.34, -4.97) * mm, "end": v(-1.33, -5) * mm});
            skLineSegment(sketch, "E1219", {"start": v(-1.33, -5) * mm, "end": v(-1.32, -5.01) * mm});
            skLineSegment(sketch, "E1220", {"start": v(-1.32, -5.01) * mm, "end": v(-1.32, -5.04) * mm});
            skLineSegment(sketch, "E1221", {"start": v(-1.32, -5.04) * mm, "end": v(-1.31, -5.06) * mm});
            skLineSegment(sketch, "E1222", {"start": v(-1.31, -5.06) * mm, "end": v(-1.3, -5.08) * mm});
            skLineSegment(sketch, "E1223", {"start": v(-1.3, -5.08) * mm, "end": v(-1.29, -5.1) * mm});
            skLineSegment(sketch, "E1224", {"start": v(-1.29, -5.1) * mm, "end": v(-1.19, -5.12) * mm});
            skLineSegment(sketch, "E1225", {"start": v(-1.19, -5.12) * mm, "end": v(-1.17, -5.12) * mm});
            skLineSegment(sketch, "E1226", {"start": v(-1.17, -5.12) * mm, "end": v(-1.15, -5.1) * mm});
            skLineSegment(sketch, "E1227", {"start": v(-1.15, -5.1) * mm, "end": v(-1.13, -5.08) * mm});
            skLineSegment(sketch, "E1228", {"start": v(-1.13, -5.08) * mm, "end": v(-1.12, -5.06) * mm});
            skLineSegment(sketch, "E1229", {"start": v(-1.12, -5.06) * mm, "end": v(-1.1, -5.05) * mm});
            skLineSegment(sketch, "E1230", {"start": v(-1.1, -5.05) * mm, "end": v(-1.08, -5.03) * mm});
            skLineSegment(sketch, "E1231", {"start": v(-1.08, -5.03) * mm, "end": v(-1.07, -5.01) * mm});
            skLineSegment(sketch, "E1232", {"start": v(-1.07, -5.01) * mm, "end": v(-1.05, -5) * mm});
            skLineSegment(sketch, "E1233", {"start": v(-1.05, -5) * mm, "end": v(-1.04, -4.98) * mm});
            skLineSegment(sketch, "E1234", {"start": v(-1.04, -4.98) * mm, "end": v(-1.03, -4.97) * mm});
            skLineSegment(sketch, "E1235", {"start": v(-1.03, -4.97) * mm, "end": v(-1.01, -4.95) * mm});
            skLineSegment(sketch, "E1236", {"start": v(-1.01, -4.95) * mm, "end": v(-1, -4.93) * mm});
            skLineSegment(sketch, "E1237", {"start": v(-1, -4.93) * mm, "end": v(-0.99, -4.92) * mm});
            skLineSegment(sketch, "E1238", {"start": v(-0.99, -4.92) * mm, "end": v(-0.98, -4.9) * mm});
            skLineSegment(sketch, "E1239", {"start": v(-0.98, -4.9) * mm, "end": v(-0.96, -4.89) * mm});
            skLineSegment(sketch, "E1240", {"start": v(-0.96, -4.89) * mm, "end": v(-0.95, -4.87) * mm});
            skLineSegment(sketch, "E1241", {"start": v(-0.95, -4.87) * mm, "end": v(-0.94, -4.86) * mm});
            skLineSegment(sketch, "E1242", {"start": v(-0.94, -4.86) * mm, "end": v(-0.93, -4.84) * mm});
            skLineSegment(sketch, "E1243", {"start": v(-0.93, -4.84) * mm, "end": v(-0.92, -4.83) * mm});
            skLineSegment(sketch, "E1244", {"start": v(-0.92, -4.83) * mm, "end": v(-0.9, -4.81) * mm});
            skLineSegment(sketch, "E1245", {"start": v(-0.9, -4.81) * mm, "end": v(-0.9, -4.8) * mm});
            skLineSegment(sketch, "E1246", {"start": v(-0.9, -4.8) * mm, "end": v(-0.89, -4.78) * mm});
            skLineSegment(sketch, "E1247", {"start": v(-0.89, -4.78) * mm, "end": v(-0.88, -4.77) * mm});
            skLineSegment(sketch, "E1248", {"start": v(-0.88, -4.77) * mm, "end": v(-0.87, -4.76) * mm});
            skLineSegment(sketch, "E1249", {"start": v(-0.87, -4.76) * mm, "end": v(-0.86, -4.74) * mm});
            skLineSegment(sketch, "E1250", {"start": v(-0.86, -4.74) * mm, "end": v(-0.85, -4.73) * mm});
            skLineSegment(sketch, "E1251", {"start": v(-0.85, -4.73) * mm, "end": v(-0.84, -4.72) * mm});
            skLineSegment(sketch, "E1252", {"start": v(-0.84, -4.72) * mm, "end": v(-0.84, -4.7) * mm});
            skLineSegment(sketch, "E1253", {"start": v(-0.84, -4.7) * mm, "end": v(-0.83, -4.69) * mm});
            skLineSegment(sketch, "E1254", {"start": v(-0.83, -4.69) * mm, "end": v(-0.82, -4.68) * mm});
            skLineSegment(sketch, "E1255", {"start": v(-0.82, -4.68) * mm, "end": v(-0.81, -4.66) * mm});
            skLineSegment(sketch, "E1256", {"start": v(-0.81, -4.66) * mm, "end": v(-0.81, -4.66) * mm});
            skLineSegment(sketch, "E1257", {"start": v(-0.81, -4.66) * mm, "end": v(-0.75, -4.66) * mm});
            skLineSegment(sketch, "E1258", {"start": v(-0.75, -4.66) * mm, "end": v(-0.74, -4.66) * mm});
            skLineSegment(sketch, "E1259", {"start": v(-0.74, -4.66) * mm, "end": v(-0.69, -4.68) * mm});
            skLineSegment(sketch, "E1260", {"start": v(-0.69, -4.68) * mm, "end": v(-0.68, -4.69) * mm});
            skLineSegment(sketch, "E1261", {"start": v(-0.68, -4.69) * mm, "end": v(-0.68, -4.7) * mm});
            skLineSegment(sketch, "E1262", {"start": v(-0.68, -4.7) * mm, "end": v(-0.68, -4.71) * mm});
            skLineSegment(sketch, "E1263", {"start": v(-0.68, -4.71) * mm, "end": v(-0.68, -4.73) * mm});
            skLineSegment(sketch, "E1264", {"start": v(-0.68, -4.73) * mm, "end": v(-0.67, -4.74) * mm});
            skLineSegment(sketch, "E1265", {"start": v(-0.67, -4.74) * mm, "end": v(-0.67, -4.76) * mm});
            skLineSegment(sketch, "E1266", {"start": v(-0.67, -4.76) * mm, "end": v(-0.66, -4.77) * mm});
            skLineSegment(sketch, "E1267", {"start": v(-0.66, -4.77) * mm, "end": v(-0.66, -4.79) * mm});
            skLineSegment(sketch, "E1268", {"start": v(-0.66, -4.79) * mm, "end": v(-0.66, -4.8) * mm});
            skLineSegment(sketch, "E1269", {"start": v(-0.66, -4.8) * mm, "end": v(-0.65, -4.82) * mm});
            skLineSegment(sketch, "E1270", {"start": v(-0.65, -4.82) * mm, "end": v(-0.65, -4.84) * mm});
            skLineSegment(sketch, "E1271", {"start": v(-0.65, -4.84) * mm, "end": v(-0.64, -4.85) * mm});
            skLineSegment(sketch, "E1272", {"start": v(-0.64, -4.85) * mm, "end": v(-0.64, -4.87) * mm});
            skLineSegment(sketch, "E1273", {"start": v(-0.64, -4.87) * mm, "end": v(-0.63, -4.89) * mm});
            skLineSegment(sketch, "E1274", {"start": v(-0.63, -4.89) * mm, "end": v(-0.62, -4.9) * mm});
            skLineSegment(sketch, "E1275", {"start": v(-0.62, -4.9) * mm, "end": v(-0.62, -4.92) * mm});
            skLineSegment(sketch, "E1276", {"start": v(-0.62, -4.92) * mm, "end": v(-0.61, -4.94) * mm});
            skLineSegment(sketch, "E1277", {"start": v(-0.61, -4.94) * mm, "end": v(-0.6, -4.96) * mm});
            skLineSegment(sketch, "E1278", {"start": v(-0.6, -4.96) * mm, "end": v(-0.6, -4.98) * mm});
            skLineSegment(sketch, "E1279", {"start": v(-0.6, -4.98) * mm, "end": v(-0.6, -5) * mm});
            skLineSegment(sketch, "E1280", {"start": v(-0.6, -5) * mm, "end": v(-0.58, -5.02) * mm});
            skLineSegment(sketch, "E1281", {"start": v(-0.58, -5.02) * mm, "end": v(-0.58, -5.04) * mm});
            skLineSegment(sketch, "E1282", {"start": v(-0.58, -5.04) * mm, "end": v(-0.57, -5.06) * mm});
            skLineSegment(sketch, "E1283", {"start": v(-0.57, -5.06) * mm, "end": v(-0.56, -5.08) * mm});
            skLineSegment(sketch, "E1284", {"start": v(-0.56, -5.08) * mm, "end": v(-0.55, -5.1) * mm});
            skLineSegment(sketch, "E1285", {"start": v(-0.55, -5.1) * mm, "end": v(-0.54, -5.12) * mm});
            skLineSegment(sketch, "E1286", {"start": v(-0.54, -5.12) * mm, "end": v(-0.53, -5.14) * mm});
            skLineSegment(sketch, "E1287", {"start": v(-0.53, -5.14) * mm, "end": v(-0.52, -5.16) * mm});
            skLineSegment(sketch, "E1288", {"start": v(-0.52, -5.16) * mm, "end": v(-0.51, -5.18) * mm});
            skLineSegment(sketch, "E1289", {"start": v(-0.51, -5.18) * mm, "end": v(-0.5, -5.2) * mm});
            skLineSegment(sketch, "E1290", {"start": v(-0.5, -5.2) * mm, "end": v(-0.5, -5.22) * mm});
            skLineSegment(sketch, "E1291", {"start": v(-0.5, -5.22) * mm, "end": v(-0.48, -5.24) * mm});
            skLineSegment(sketch, "E1292", {"start": v(-0.48, -5.24) * mm, "end": v(-0.37, -5.25) * mm});
            skLineSegment(sketch, "E1293", {"start": v(-0.37, -5.25) * mm, "end": v(-0.35, -5.24) * mm});
            skLineSegment(sketch, "E1294", {"start": v(-0.35, -5.24) * mm, "end": v(-0.34, -5.21) * mm});
            skLineSegment(sketch, "E1295", {"start": v(-0.34, -5.21) * mm, "end": v(-0.32, -5.2) * mm});
            skLineSegment(sketch, "E1296", {"start": v(-0.32, -5.2) * mm, "end": v(-0.3, -5.18) * mm});
            skLineSegment(sketch, "E1297", {"start": v(-0.3, -5.18) * mm, "end": v(-0.3, -5.16) * mm});
            skLineSegment(sketch, "E1298", {"start": v(-0.3, -5.16) * mm, "end": v(-0.28, -5.14) * mm});
            skLineSegment(sketch, "E1299", {"start": v(-0.28, -5.14) * mm, "end": v(-0.27, -5.12) * mm});
            skLineSegment(sketch, "E1300", {"start": v(-0.27, -5.12) * mm, "end": v(-0.26, -5.1) * mm});
            skLineSegment(sketch, "E1301", {"start": v(-0.26, -5.1) * mm, "end": v(-0.25, -5.08) * mm});
            skLineSegment(sketch, "E1302", {"start": v(-0.25, -5.08) * mm, "end": v(-0.24, -5.06) * mm});
            skLineSegment(sketch, "E1303", {"start": v(-0.24, -5.06) * mm, "end": v(-0.23, -5.05) * mm});
            skLineSegment(sketch, "E1304", {"start": v(-0.23, -5.05) * mm, "end": v(-0.22, -5.03) * mm});
            skLineSegment(sketch, "E1305", {"start": v(-0.22, -5.03) * mm, "end": v(-0.2, -5.01) * mm});
            skLineSegment(sketch, "E1306", {"start": v(-0.2, -5.01) * mm, "end": v(-0.2, -5) * mm});
            skLineSegment(sketch, "E1307", {"start": v(-0.2, -5) * mm, "end": v(-0.19, -4.98) * mm});
            skLineSegment(sketch, "E1308", {"start": v(-0.19, -4.98) * mm, "end": v(-0.18, -4.96) * mm});
            skLineSegment(sketch, "E1309", {"start": v(-0.18, -4.96) * mm, "end": v(-0.17, -4.94) * mm});
            skLineSegment(sketch, "E1310", {"start": v(-0.17, -4.94) * mm, "end": v(-0.16, -4.93) * mm});
            skLineSegment(sketch, "E1311", {"start": v(-0.16, -4.93) * mm, "end": v(-0.15, -4.91) * mm});
            skLineSegment(sketch, "E1312", {"start": v(-0.15, -4.91) * mm, "end": v(-0.14, -4.9) * mm});
            skLineSegment(sketch, "E1313", {"start": v(-0.14, -4.9) * mm, "end": v(-0.14, -4.88) * mm});
            skLineSegment(sketch, "E1314", {"start": v(-0.14, -4.88) * mm, "end": v(-0.13, -4.86) * mm});
            skLineSegment(sketch, "E1315", {"start": v(-0.13, -4.86) * mm, "end": v(-0.12, -4.85) * mm});
            skLineSegment(sketch, "E1316", {"start": v(-0.12, -4.85) * mm, "end": v(-0.12, -4.83) * mm});
            skLineSegment(sketch, "E1317", {"start": v(-0.12, -4.83) * mm, "end": v(-0.1, -4.82) * mm});
            skLineSegment(sketch, "E1318", {"start": v(-0.1, -4.82) * mm, "end": v(-0.1, -4.8) * mm});
            skLineSegment(sketch, "E1319", {"start": v(-0.1, -4.8) * mm, "end": v(-0.1, -4.79) * mm});
            skLineSegment(sketch, "E1320", {"start": v(-0.1, -4.79) * mm, "end": v(-0.1, -4.77) * mm});
            skLineSegment(sketch, "E1321", {"start": v(-0.1, -4.77) * mm, "end": v(-0.08, -4.76) * mm});
            skLineSegment(sketch, "E1322", {"start": v(-0.08, -4.76) * mm, "end": v(-0.08, -4.75) * mm});
            skLineSegment(sketch, "E1323", {"start": v(-0.08, -4.75) * mm, "end": v(-0.07, -4.73) * mm});
            skLineSegment(sketch, "E1324", {"start": v(-0.07, -4.73) * mm, "end": v(-0.07, -4.73) * mm});
            skLineSegment(sketch, "E1325", {"start": v(-0.07, -4.73) * mm, "end": v(-0.02, -4.72) * mm});
            skLineSegment(sketch, "E1326", {"start": v(-0.02, -4.72) * mm, "end": v(0, -4.72) * mm});
            skLineSegment(sketch, "E1327", {"start": v(0, -4.72) * mm, "end": v(0.05, -4.73) * mm});
            skLineSegment(sketch, "E1328", {"start": v(0.05, -4.73) * mm, "end": v(0.06, -4.73) * mm});
            skLineSegment(sketch, "E1329", {"start": v(0.06, -4.73) * mm, "end": v(0.06, -4.75) * mm});
            skLineSegment(sketch, "E1330", {"start": v(0.06, -4.75) * mm, "end": v(0.07, -4.76) * mm});
            skLineSegment(sketch, "E1331", {"start": v(0.07, -4.76) * mm, "end": v(0.07, -4.78) * mm});
            skLineSegment(sketch, "E1332", {"start": v(0.07, -4.78) * mm, "end": v(0.08, -4.79) * mm});
            skLineSegment(sketch, "E1333", {"start": v(0.08, -4.79) * mm, "end": v(0.08, -4.8) * mm});
            skLineSegment(sketch, "E1334", {"start": v(0.08, -4.8) * mm, "end": v(0.1, -4.82) * mm});
            skLineSegment(sketch, "E1335", {"start": v(0.1, -4.82) * mm, "end": v(0.1, -4.83) * mm});
            skLineSegment(sketch, "E1336", {"start": v(0.1, -4.83) * mm, "end": v(0.1, -4.85) * mm});
            skLineSegment(sketch, "E1337", {"start": v(0.1, -4.85) * mm, "end": v(0.11, -4.86) * mm});
            skLineSegment(sketch, "E1338", {"start": v(0.11, -4.86) * mm, "end": v(0.12, -4.88) * mm});
            skLineSegment(sketch, "E1339", {"start": v(0.12, -4.88) * mm, "end": v(0.13, -4.9) * mm});
            skLineSegment(sketch, "E1340", {"start": v(0.13, -4.9) * mm, "end": v(0.13, -4.91) * mm});
            skLineSegment(sketch, "E1341", {"start": v(0.13, -4.91) * mm, "end": v(0.14, -4.93) * mm});
            skLineSegment(sketch, "E1342", {"start": v(0.14, -4.93) * mm, "end": v(0.15, -4.94) * mm});
            skLineSegment(sketch, "E1343", {"start": v(0.15, -4.94) * mm, "end": v(0.16, -4.96) * mm});
            skLineSegment(sketch, "E1344", {"start": v(0.16, -4.96) * mm, "end": v(0.17, -4.98) * mm});
            skLineSegment(sketch, "E1345", {"start": v(0.17, -4.98) * mm, "end": v(0.18, -5) * mm});
            skLineSegment(sketch, "E1346", {"start": v(0.18, -5) * mm, "end": v(0.19, -5.01) * mm});
            skLineSegment(sketch, "E1347", {"start": v(0.19, -5.01) * mm, "end": v(0.2, -5.03) * mm});
            skLineSegment(sketch, "E1348", {"start": v(0.2, -5.03) * mm, "end": v(0.2, -5.05) * mm});
            skLineSegment(sketch, "E1349", {"start": v(0.2, -5.05) * mm, "end": v(0.22, -5.07) * mm});
            skLineSegment(sketch, "E1350", {"start": v(0.22, -5.07) * mm, "end": v(0.23, -5.08) * mm});
            skLineSegment(sketch, "E1351", {"start": v(0.23, -5.08) * mm, "end": v(0.24, -5.1) * mm});
            skLineSegment(sketch, "E1352", {"start": v(0.24, -5.1) * mm, "end": v(0.25, -5.12) * mm});
            skLineSegment(sketch, "E1353", {"start": v(0.25, -5.12) * mm, "end": v(0.27, -5.14) * mm});
            skLineSegment(sketch, "E1354", {"start": v(0.27, -5.14) * mm, "end": v(0.28, -5.16) * mm});
            skLineSegment(sketch, "E1355", {"start": v(0.28, -5.16) * mm, "end": v(0.3, -5.18) * mm});
            skLineSegment(sketch, "E1356", {"start": v(0.3, -5.18) * mm, "end": v(0.3, -5.2) * mm});
            skLineSegment(sketch, "E1357", {"start": v(0.3, -5.2) * mm, "end": v(0.32, -5.22) * mm});
            skLineSegment(sketch, "E1358", {"start": v(0.32, -5.22) * mm, "end": v(0.33, -5.24) * mm});
            skLineSegment(sketch, "E1359", {"start": v(0.33, -5.24) * mm, "end": v(0.35, -5.25) * mm});
            skLineSegment(sketch, "E1360", {"start": v(0.35, -5.25) * mm, "end": v(0.46, -5.24) * mm});
            skLineSegment(sketch, "E1361", {"start": v(0.46, -5.24) * mm, "end": v(0.47, -5.23) * mm});
            skLineSegment(sketch, "E1362", {"start": v(0.47, -5.23) * mm, "end": v(0.48, -5.2) * mm});
            skLineSegment(sketch, "E1363", {"start": v(0.48, -5.2) * mm, "end": v(0.5, -5.18) * mm});
            skLineSegment(sketch, "E1364", {"start": v(0.5, -5.18) * mm, "end": v(0.5, -5.16) * mm});
            skLineSegment(sketch, "E1365", {"start": v(0.5, -5.16) * mm, "end": v(0.51, -5.14) * mm});
            skLineSegment(sketch, "E1366", {"start": v(0.51, -5.14) * mm, "end": v(0.52, -5.12) * mm});
            skLineSegment(sketch, "E1367", {"start": v(0.52, -5.12) * mm, "end": v(0.53, -5.1) * mm});
            skLineSegment(sketch, "E1368", {"start": v(0.53, -5.1) * mm, "end": v(0.54, -5.08) * mm});
            skLineSegment(sketch, "E1369", {"start": v(0.54, -5.08) * mm, "end": v(0.55, -5.06) * mm});
            skLineSegment(sketch, "E1370", {"start": v(0.55, -5.06) * mm, "end": v(0.56, -5.04) * mm});
            skLineSegment(sketch, "E1371", {"start": v(0.56, -5.04) * mm, "end": v(0.57, -5.02) * mm});
            skLineSegment(sketch, "E1372", {"start": v(0.57, -5.02) * mm, "end": v(0.57, -5) * mm});
            skLineSegment(sketch, "E1373", {"start": v(0.57, -5) * mm, "end": v(0.58, -4.98) * mm});
            skLineSegment(sketch, "E1374", {"start": v(0.58, -4.98) * mm, "end": v(0.59, -4.96) * mm});
            skLineSegment(sketch, "E1375", {"start": v(0.59, -4.96) * mm, "end": v(0.6, -4.94) * mm});
            skLineSegment(sketch, "E1376", {"start": v(0.6, -4.94) * mm, "end": v(0.6, -4.93) * mm});
            skLineSegment(sketch, "E1377", {"start": v(0.6, -4.93) * mm, "end": v(0.6, -4.9) * mm});
            skLineSegment(sketch, "E1378", {"start": v(0.6, -4.9) * mm, "end": v(0.61, -4.9) * mm});
            skLineSegment(sketch, "E1379", {"start": v(0.61, -4.9) * mm, "end": v(0.62, -4.87) * mm});
            skLineSegment(sketch, "E1380", {"start": v(0.62, -4.87) * mm, "end": v(0.62, -4.86) * mm});
            skLineSegment(sketch, "E1381", {"start": v(0.62, -4.86) * mm, "end": v(0.63, -4.84) * mm});
            skLineSegment(sketch, "E1382", {"start": v(0.63, -4.84) * mm, "end": v(0.63, -4.82) * mm});
            skLineSegment(sketch, "E1383", {"start": v(0.63, -4.82) * mm, "end": v(0.64, -4.8) * mm});
            skLineSegment(sketch, "E1384", {"start": v(0.64, -4.8) * mm, "end": v(0.64, -4.8) * mm});
            skLineSegment(sketch, "E1385", {"start": v(0.64, -4.8) * mm, "end": v(0.65, -4.78) * mm});
            skLineSegment(sketch, "E1386", {"start": v(0.65, -4.78) * mm, "end": v(0.65, -4.76) * mm});
            skLineSegment(sketch, "E1387", {"start": v(0.65, -4.76) * mm, "end": v(0.65, -4.74) * mm});
            skLineSegment(sketch, "E1388", {"start": v(0.65, -4.74) * mm, "end": v(0.66, -4.73) * mm});
            skLineSegment(sketch, "E1389", {"start": v(0.66, -4.73) * mm, "end": v(0.66, -4.72) * mm});
            skLineSegment(sketch, "E1390", {"start": v(0.66, -4.72) * mm, "end": v(0.66, -4.7) * mm});
            skLineSegment(sketch, "E1391", {"start": v(0.66, -4.7) * mm, "end": v(0.67, -4.69) * mm});
            skLineSegment(sketch, "E1392", {"start": v(0.67, -4.69) * mm, "end": v(0.67, -4.68) * mm});
            skLineSegment(sketch, "E1393", {"start": v(0.67, -4.68) * mm, "end": v(0.72, -4.67) * mm});
            skLineSegment(sketch, "E1394", {"start": v(0.72, -4.67) * mm, "end": v(0.74, -4.66) * mm});
            skLineSegment(sketch, "E1395", {"start": v(0.74, -4.66) * mm, "end": v(0.8, -4.66) * mm});
            skLineSegment(sketch, "E1396", {"start": v(0.8, -4.66) * mm, "end": v(0.8, -4.67) * mm});
            skLineSegment(sketch, "E1397", {"start": v(0.8, -4.67) * mm, "end": v(0.8, -4.68) * mm});
            skLineSegment(sketch, "E1398", {"start": v(0.8, -4.68) * mm, "end": v(0.81, -4.7) * mm});
            skLineSegment(sketch, "E1399", {"start": v(0.81, -4.7) * mm, "end": v(0.82, -4.7) * mm});
            skLineSegment(sketch, "E1400", {"start": v(0.82, -4.7) * mm, "end": v(0.83, -4.72) * mm});
            skLineSegment(sketch, "E1401", {"start": v(0.83, -4.72) * mm, "end": v(0.83, -4.73) * mm});
            skLineSegment(sketch, "E1402", {"start": v(0.83, -4.73) * mm, "end": v(0.84, -4.74) * mm});
            skLineSegment(sketch, "E1403", {"start": v(0.84, -4.74) * mm, "end": v(0.85, -4.76) * mm});
            skLineSegment(sketch, "E1404", {"start": v(0.85, -4.76) * mm, "end": v(0.86, -4.77) * mm});
            skLineSegment(sketch, "E1405", {"start": v(0.86, -4.77) * mm, "end": v(0.87, -4.79) * mm});
            skLineSegment(sketch, "E1406", {"start": v(0.87, -4.79) * mm, "end": v(0.88, -4.8) * mm});
            skLineSegment(sketch, "E1407", {"start": v(0.88, -4.8) * mm, "end": v(0.9, -4.81) * mm});
            skLineSegment(sketch, "E1408", {"start": v(0.9, -4.81) * mm, "end": v(0.9, -4.83) * mm});
            skLineSegment(sketch, "E1409", {"start": v(0.9, -4.83) * mm, "end": v(0.91, -4.84) * mm});
            skLineSegment(sketch, "E1410", {"start": v(0.91, -4.84) * mm, "end": v(0.92, -4.86) * mm});
            skLineSegment(sketch, "E1411", {"start": v(0.92, -4.86) * mm, "end": v(0.93, -4.87) * mm});
            skLineSegment(sketch, "E1412", {"start": v(0.93, -4.87) * mm, "end": v(0.95, -4.89) * mm});
            skLineSegment(sketch, "E1413", {"start": v(0.95, -4.89) * mm, "end": v(0.96, -4.9) * mm});
            skLineSegment(sketch, "E1414", {"start": v(0.96, -4.9) * mm, "end": v(0.97, -4.92) * mm});
            skLineSegment(sketch, "E1415", {"start": v(0.97, -4.92) * mm, "end": v(0.98, -4.94) * mm});
            skLineSegment(sketch, "E1416", {"start": v(0.98, -4.94) * mm, "end": v(1, -4.95) * mm});
            skLineSegment(sketch, "E1417", {"start": v(1, -4.95) * mm, "end": v(1, -4.97) * mm});
            skLineSegment(sketch, "E1418", {"start": v(1, -4.97) * mm, "end": v(1.02, -4.98) * mm});
            skLineSegment(sketch, "E1419", {"start": v(1.02, -4.98) * mm, "end": v(1.04, -5) * mm});
            skLineSegment(sketch, "E1420", {"start": v(1.04, -5) * mm, "end": v(1.05, -5.02) * mm});
            skLineSegment(sketch, "E1421", {"start": v(1.05, -5.02) * mm, "end": v(1.07, -5.03) * mm});
            skLineSegment(sketch, "E1422", {"start": v(1.07, -5.03) * mm, "end": v(1.08, -5.05) * mm});
            skLineSegment(sketch, "E1423", {"start": v(1.08, -5.05) * mm, "end": v(1.1, -5.07) * mm});
            skLineSegment(sketch, "E1424", {"start": v(1.1, -5.07) * mm, "end": v(1.11, -5.08) * mm});
            skLineSegment(sketch, "E1425", {"start": v(1.11, -5.08) * mm, "end": v(1.13, -5.1) * mm});
            skLineSegment(sketch, "E1426", {"start": v(1.13, -5.1) * mm, "end": v(1.15, -5.12) * mm});
            skLineSegment(sketch, "E1427", {"start": v(1.15, -5.12) * mm, "end": v(1.17, -5.13) * mm});
            skLineSegment(sketch, "E1428", {"start": v(1.17, -5.13) * mm, "end": v(1.27, -5.1) * mm});
            skLineSegment(sketch, "E1429", {"start": v(1.27, -5.1) * mm, "end": v(1.28, -5.09) * mm});
            skLineSegment(sketch, "E1430", {"start": v(1.28, -5.09) * mm, "end": v(1.3, -5.06) * mm});
            skLineSegment(sketch, "E1431", {"start": v(1.3, -5.06) * mm, "end": v(1.3, -5.04) * mm});
            skLineSegment(sketch, "E1432", {"start": v(1.3, -5.04) * mm, "end": v(1.3, -5.02) * mm});
            skLineSegment(sketch, "E1433", {"start": v(1.3, -5.02) * mm, "end": v(1.31, -5) * mm});
            skLineSegment(sketch, "E1434", {"start": v(1.31, -5) * mm, "end": v(1.32, -4.97) * mm});
            skLineSegment(sketch, "E1435", {"start": v(1.32, -4.97) * mm, "end": v(1.32, -4.95) * mm});
            skLineSegment(sketch, "E1436", {"start": v(1.32, -4.95) * mm, "end": v(1.33, -4.93) * mm});
            skLineSegment(sketch, "E1437", {"start": v(1.33, -4.93) * mm, "end": v(1.33, -4.91) * mm});
            skLineSegment(sketch, "E1438", {"start": v(1.33, -4.91) * mm, "end": v(1.34, -4.89) * mm});
            skLineSegment(sketch, "E1439", {"start": v(1.34, -4.89) * mm, "end": v(1.34, -4.87) * mm});
            skLineSegment(sketch, "E1440", {"start": v(1.34, -4.87) * mm, "end": v(1.35, -4.85) * mm});
            skLineSegment(sketch, "E1441", {"start": v(1.35, -4.85) * mm, "end": v(1.35, -4.83) * mm});
            skLineSegment(sketch, "E1442", {"start": v(1.35, -4.83) * mm, "end": v(1.36, -4.8) * mm});
            skLineSegment(sketch, "E1443", {"start": v(1.36, -4.8) * mm, "end": v(1.36, -4.8) * mm});
            skLineSegment(sketch, "E1444", {"start": v(1.36, -4.8) * mm, "end": v(1.36, -4.77) * mm});
            skLineSegment(sketch, "E1445", {"start": v(1.36, -4.77) * mm, "end": v(1.37, -4.75) * mm});
            skLineSegment(sketch, "E1446", {"start": v(1.37, -4.75) * mm, "end": v(1.37, -4.73) * mm});
            skLineSegment(sketch, "E1447", {"start": v(1.37, -4.73) * mm, "end": v(1.37, -4.72) * mm});
            skLineSegment(sketch, "E1448", {"start": v(1.37, -4.72) * mm, "end": v(1.38, -4.7) * mm});
            skLineSegment(sketch, "E1449", {"start": v(1.38, -4.7) * mm, "end": v(1.38, -4.68) * mm});
            skLineSegment(sketch, "E1450", {"start": v(1.38, -4.68) * mm, "end": v(1.38, -4.66) * mm});
            skLineSegment(sketch, "E1451", {"start": v(1.38, -4.66) * mm, "end": v(1.38, -4.65) * mm});
            skLineSegment(sketch, "E1452", {"start": v(1.38, -4.65) * mm, "end": v(1.38, -4.63) * mm});
            skLineSegment(sketch, "E1453", {"start": v(1.38, -4.63) * mm, "end": v(1.39, -4.62) * mm});
            skLineSegment(sketch, "E1454", {"start": v(1.39, -4.62) * mm, "end": v(1.39, -4.6) * mm});
            skLineSegment(sketch, "E1455", {"start": v(1.39, -4.6) * mm, "end": v(1.39, -4.58) * mm});
            skLineSegment(sketch, "E1456", {"start": v(1.39, -4.58) * mm, "end": v(1.39, -4.57) * mm});
            skLineSegment(sketch, "E1457", {"start": v(1.39, -4.57) * mm, "end": v(1.4, -4.55) * mm});
            skLineSegment(sketch, "E1458", {"start": v(1.4, -4.55) * mm, "end": v(1.4, -4.54) * mm});
            skLineSegment(sketch, "E1459", {"start": v(1.4, -4.54) * mm, "end": v(1.4, -4.53) * mm});
            skLineSegment(sketch, "E1460", {"start": v(1.4, -4.53) * mm, "end": v(1.4, -4.52) * mm});
            skLineSegment(sketch, "E1461", {"start": v(1.4, -4.52) * mm, "end": v(1.44, -4.5) * mm});
            skLineSegment(sketch, "E1462", {"start": v(1.44, -4.5) * mm, "end": v(1.46, -4.5) * mm});
            skLineSegment(sketch, "E1463", {"start": v(1.46, -4.5) * mm, "end": v(1.51, -4.48) * mm});
            skLineSegment(sketch, "E1464", {"start": v(1.51, -4.48) * mm, "end": v(1.52, -4.49) * mm});
            skLineSegment(sketch, "E1465", {"start": v(1.52, -4.49) * mm, "end": v(1.53, -4.5) * mm});
            skLineSegment(sketch, "E1466", {"start": v(1.53, -4.5) * mm, "end": v(1.54, -4.5) * mm});
            skLineSegment(sketch, "E1467", {"start": v(1.54, -4.5) * mm, "end": v(1.54, -4.52) * mm});
            skLineSegment(sketch, "E1468", {"start": v(1.54, -4.52) * mm, "end": v(1.55, -4.53) * mm});
            skLineSegment(sketch, "E1469", {"start": v(1.55, -4.53) * mm, "end": v(1.56, -4.54) * mm});
            skLineSegment(sketch, "E1470", {"start": v(1.56, -4.54) * mm, "end": v(1.58, -4.55) * mm});
            skLineSegment(sketch, "E1471", {"start": v(1.58, -4.55) * mm, "end": v(1.59, -4.57) * mm});
            skLineSegment(sketch, "E1472", {"start": v(1.59, -4.57) * mm, "end": v(1.6, -4.58) * mm});
            skLineSegment(sketch, "E1473", {"start": v(1.6, -4.58) * mm, "end": v(1.6, -4.6) * mm});
            skLineSegment(sketch, "E1474", {"start": v(1.6, -4.6) * mm, "end": v(1.62, -4.6) * mm});
            skLineSegment(sketch, "E1475", {"start": v(1.62, -4.6) * mm, "end": v(1.63, -4.62) * mm});
            skLineSegment(sketch, "E1476", {"start": v(1.63, -4.62) * mm, "end": v(1.64, -4.63) * mm});
            skLineSegment(sketch, "E1477", {"start": v(1.64, -4.63) * mm, "end": v(1.66, -4.64) * mm});
            skLineSegment(sketch, "E1478", {"start": v(1.66, -4.64) * mm, "end": v(1.67, -4.65) * mm});
            skLineSegment(sketch, "E1479", {"start": v(1.67, -4.65) * mm, "end": v(1.68, -4.67) * mm});
            skLineSegment(sketch, "E1480", {"start": v(1.68, -4.67) * mm, "end": v(1.7, -4.68) * mm});
            skLineSegment(sketch, "E1481", {"start": v(1.7, -4.68) * mm, "end": v(1.71, -4.7) * mm});
            skLineSegment(sketch, "E1482", {"start": v(1.71, -4.7) * mm, "end": v(1.73, -4.7) * mm});
            skLineSegment(sketch, "E1483", {"start": v(1.73, -4.7) * mm, "end": v(1.74, -4.72) * mm});
            skLineSegment(sketch, "E1484", {"start": v(1.74, -4.72) * mm, "end": v(1.76, -4.74) * mm});
            skLineSegment(sketch, "E1485", {"start": v(1.76, -4.74) * mm, "end": v(1.77, -4.75) * mm});
            skLineSegment(sketch, "E1486", {"start": v(1.77, -4.75) * mm, "end": v(1.79, -4.76) * mm});
            skLineSegment(sketch, "E1487", {"start": v(1.79, -4.76) * mm, "end": v(1.8, -4.78) * mm});
            skLineSegment(sketch, "E1488", {"start": v(1.8, -4.78) * mm, "end": v(1.82, -4.8) * mm});
            skLineSegment(sketch, "E1489", {"start": v(1.82, -4.8) * mm, "end": v(1.84, -4.8) * mm});
            skLineSegment(sketch, "E1490", {"start": v(1.84, -4.8) * mm, "end": v(1.86, -4.82) * mm});
            skLineSegment(sketch, "E1491", {"start": v(1.86, -4.82) * mm, "end": v(1.88, -4.83) * mm});
            skLineSegment(sketch, "E1492", {"start": v(1.88, -4.83) * mm, "end": v(1.9, -4.85) * mm});
            skLineSegment(sketch, "E1493", {"start": v(1.9, -4.85) * mm, "end": v(1.91, -4.86) * mm});
            skLineSegment(sketch, "E1494", {"start": v(1.91, -4.86) * mm, "end": v(1.93, -4.88) * mm});
            skLineSegment(sketch, "E1495", {"start": v(1.93, -4.88) * mm, "end": v(1.95, -4.88) * mm});
            skLineSegment(sketch, "E1496", {"start": v(1.95, -4.88) * mm, "end": v(2.05, -4.84) * mm});
            skLineSegment(sketch, "E1497", {"start": v(2.05, -4.84) * mm, "end": v(2.06, -4.82) * mm});
            skLineSegment(sketch, "E1498", {"start": v(2.06, -4.82) * mm, "end": v(2.07, -4.8) * mm});
            skLineSegment(sketch, "E1499", {"start": v(2.07, -4.8) * mm, "end": v(2.07, -4.78) * mm});
            skLineSegment(sketch, "E1500", {"start": v(2.07, -4.78) * mm, "end": v(2.07, -4.75) * mm});
            skLineSegment(sketch, "E1501", {"start": v(2.07, -4.75) * mm, "end": v(2.08, -4.73) * mm});
            skLineSegment(sketch, "E1502", {"start": v(2.08, -4.73) * mm, "end": v(2.08, -4.7) * mm});
            skLineSegment(sketch, "E1503", {"start": v(2.08, -4.7) * mm, "end": v(2.08, -4.68) * mm});
            skLineSegment(sketch, "E1504", {"start": v(2.08, -4.68) * mm, "end": v(2.08, -4.66) * mm});
            skLineSegment(sketch, "E1505", {"start": v(2.08, -4.66) * mm, "end": v(2.09, -4.64) * mm});
            skLineSegment(sketch, "E1506", {"start": v(2.09, -4.64) * mm, "end": v(2.09, -4.62) * mm});
            skLineSegment(sketch, "E1507", {"start": v(2.09, -4.62) * mm, "end": v(2.09, -4.6) * mm});
            skLineSegment(sketch, "E1508", {"start": v(2.09, -4.6) * mm, "end": v(2.1, -4.58) * mm});
            skLineSegment(sketch, "E1509", {"start": v(2.1, -4.58) * mm, "end": v(2.1, -4.56) * mm});
            skLineSegment(sketch, "E1510", {"start": v(2.1, -4.56) * mm, "end": v(2.1, -4.54) * mm});
            skLineSegment(sketch, "E1511", {"start": v(2.1, -4.54) * mm, "end": v(2.1, -4.52) * mm});
            skLineSegment(sketch, "E1512", {"start": v(2.1, -4.52) * mm, "end": v(2.1, -4.5) * mm});
            skLineSegment(sketch, "E1513", {"start": v(2.1, -4.5) * mm, "end": v(2.1, -4.48) * mm});
            skLineSegment(sketch, "E1514", {"start": v(2.1, -4.48) * mm, "end": v(2.1, -4.46) * mm});
            skLineSegment(sketch, "E1515", {"start": v(2.1, -4.46) * mm, "end": v(2.1, -4.44) * mm});
            skLineSegment(sketch, "E1516", {"start": v(2.1, -4.44) * mm, "end": v(2.1, -4.43) * mm});
            skLineSegment(sketch, "E1517", {"start": v(2.1, -4.43) * mm, "end": v(2.1, -4.4) * mm});
            skLineSegment(sketch, "E1518", {"start": v(2.1, -4.4) * mm, "end": v(2.1, -4.4) * mm});
            skLineSegment(sketch, "E1519", {"start": v(2.1, -4.4) * mm, "end": v(2.1, -4.37) * mm});
            skLineSegment(sketch, "E1520", {"start": v(2.1, -4.37) * mm, "end": v(2.1, -4.36) * mm});
            skLineSegment(sketch, "E1521", {"start": v(2.1, -4.36) * mm, "end": v(2.1, -4.34) * mm});
            skLineSegment(sketch, "E1522", {"start": v(2.1, -4.34) * mm, "end": v(2.09, -4.33) * mm});
            skLineSegment(sketch, "E1523", {"start": v(2.09, -4.33) * mm, "end": v(2.09, -4.31) * mm});
            skLineSegment(sketch, "E1524", {"start": v(2.09, -4.31) * mm, "end": v(2.09, -4.3) * mm});
            skLineSegment(sketch, "E1525", {"start": v(2.09, -4.3) * mm, "end": v(2.09, -4.28) * mm});
            skLineSegment(sketch, "E1526", {"start": v(2.09, -4.28) * mm, "end": v(2.08, -4.27) * mm});
            skLineSegment(sketch, "E1527", {"start": v(2.08, -4.27) * mm, "end": v(2.08, -4.25) * mm});
            skLineSegment(sketch, "E1528", {"start": v(2.08, -4.25) * mm, "end": v(2.08, -4.24) * mm});
            skLineSegment(sketch, "E1529", {"start": v(2.08, -4.24) * mm, "end": v(2.13, -4.21) * mm});
            skLineSegment(sketch, "E1530", {"start": v(2.13, -4.21) * mm, "end": v(2.14, -4.2) * mm});
            skLineSegment(sketch, "E1531", {"start": v(2.14, -4.2) * mm, "end": v(2.2, -4.19) * mm});
            skLineSegment(sketch, "E1532", {"start": v(2.2, -4.19) * mm, "end": v(2.2, -4.2) * mm});
            skLineSegment(sketch, "E1533", {"start": v(2.2, -4.2) * mm, "end": v(2.21, -4.2) * mm});
            skLineSegment(sketch, "E1534", {"start": v(2.21, -4.2) * mm, "end": v(2.22, -4.21) * mm});
            skLineSegment(sketch, "E1535", {"start": v(2.22, -4.21) * mm, "end": v(2.23, -4.22) * mm});
            skLineSegment(sketch, "E1536", {"start": v(2.23, -4.22) * mm, "end": v(2.24, -4.23) * mm});
            skLineSegment(sketch, "E1537", {"start": v(2.24, -4.23) * mm, "end": v(2.26, -4.24) * mm});
            skLineSegment(sketch, "E1538", {"start": v(2.26, -4.24) * mm, "end": v(2.27, -4.25) * mm});
            skLineSegment(sketch, "E1539", {"start": v(2.27, -4.25) * mm, "end": v(2.28, -4.26) * mm});
            skLineSegment(sketch, "E1540", {"start": v(2.28, -4.26) * mm, "end": v(2.3, -4.27) * mm});
            skLineSegment(sketch, "E1541", {"start": v(2.3, -4.27) * mm, "end": v(2.3, -4.28) * mm});
            skLineSegment(sketch, "E1542", {"start": v(2.3, -4.28) * mm, "end": v(2.32, -4.3) * mm});
            skLineSegment(sketch, "E1543", {"start": v(2.32, -4.3) * mm, "end": v(2.33, -4.3) * mm});
            skLineSegment(sketch, "E1544", {"start": v(2.33, -4.3) * mm, "end": v(2.35, -4.31) * mm});
            skLineSegment(sketch, "E1545", {"start": v(2.35, -4.31) * mm, "end": v(2.36, -4.33) * mm});
            skLineSegment(sketch, "E1546", {"start": v(2.36, -4.33) * mm, "end": v(2.38, -4.34) * mm});
            skLineSegment(sketch, "E1547", {"start": v(2.38, -4.34) * mm, "end": v(2.4, -4.35) * mm});
            skLineSegment(sketch, "E1548", {"start": v(2.4, -4.35) * mm, "end": v(2.4, -4.36) * mm});
            skLineSegment(sketch, "E1549", {"start": v(2.4, -4.36) * mm, "end": v(2.43, -4.37) * mm});
            skLineSegment(sketch, "E1550", {"start": v(2.43, -4.37) * mm, "end": v(2.44, -4.38) * mm});
            skLineSegment(sketch, "E1551", {"start": v(2.44, -4.38) * mm, "end": v(2.46, -4.4) * mm});
            skLineSegment(sketch, "E1552", {"start": v(2.46, -4.4) * mm, "end": v(2.48, -4.4) * mm});
            skLineSegment(sketch, "E1553", {"start": v(2.48, -4.4) * mm, "end": v(2.5, -4.41) * mm});
            skLineSegment(sketch, "E1554", {"start": v(2.5, -4.41) * mm, "end": v(2.51, -4.42) * mm});
            skLineSegment(sketch, "E1555", {"start": v(2.51, -4.42) * mm, "end": v(2.53, -4.44) * mm});
            skLineSegment(sketch, "E1556", {"start": v(2.53, -4.44) * mm, "end": v(2.55, -4.45) * mm});
            skLineSegment(sketch, "E1557", {"start": v(2.55, -4.45) * mm, "end": v(2.57, -4.46) * mm});
            skLineSegment(sketch, "E1558", {"start": v(2.57, -4.46) * mm, "end": v(2.59, -4.47) * mm});
            skLineSegment(sketch, "E1559", {"start": v(2.59, -4.47) * mm, "end": v(2.6, -4.48) * mm});
            skLineSegment(sketch, "E1560", {"start": v(2.6, -4.48) * mm, "end": v(2.63, -4.5) * mm});
            skLineSegment(sketch, "E1561", {"start": v(2.63, -4.5) * mm, "end": v(2.65, -4.5) * mm});
            skLineSegment(sketch, "E1562", {"start": v(2.65, -4.5) * mm, "end": v(2.67, -4.52) * mm});
            skLineSegment(sketch, "E1563", {"start": v(2.67, -4.52) * mm, "end": v(2.7, -4.52) * mm});
            skLineSegment(sketch, "E1564", {"start": v(2.7, -4.52) * mm, "end": v(2.79, -4.46) * mm});
            skLineSegment(sketch, "E1565", {"start": v(2.79, -4.46) * mm, "end": v(2.8, -4.44) * mm});
            skLineSegment(sketch, "E1566", {"start": v(2.8, -4.44) * mm, "end": v(2.8, -4.42) * mm});
            skLineSegment(sketch, "E1567", {"start": v(2.8, -4.42) * mm, "end": v(2.8, -4.4) * mm});
            skLineSegment(sketch, "E1568", {"start": v(2.8, -4.4) * mm, "end": v(2.8, -4.37) * mm});
            skLineSegment(sketch, "E1569", {"start": v(2.8, -4.37) * mm, "end": v(2.8, -4.35) * mm});
            skLineSegment(sketch, "E1570", {"start": v(2.8, -4.35) * mm, "end": v(2.8, -4.32) * mm});
            skLineSegment(sketch, "E1571", {"start": v(2.8, -4.32) * mm, "end": v(2.79, -4.3) * mm});
            skLineSegment(sketch, "E1572", {"start": v(2.79, -4.3) * mm, "end": v(2.79, -4.28) * mm});
            skLineSegment(sketch, "E1573", {"start": v(2.79, -4.28) * mm, "end": v(2.79, -4.26) * mm});
            skLineSegment(sketch, "E1574", {"start": v(2.79, -4.26) * mm, "end": v(2.78, -4.24) * mm});
            skLineSegment(sketch, "E1575", {"start": v(2.78, -4.24) * mm, "end": v(2.78, -4.22) * mm});
            skLineSegment(sketch, "E1576", {"start": v(2.78, -4.22) * mm, "end": v(2.78, -4.2) * mm});
            skLineSegment(sketch, "E1577", {"start": v(2.78, -4.2) * mm, "end": v(2.78, -4.17) * mm});
            skLineSegment(sketch, "E1578", {"start": v(2.78, -4.17) * mm, "end": v(2.78, -4.16) * mm});
            skLineSegment(sketch, "E1579", {"start": v(2.78, -4.16) * mm, "end": v(2.77, -4.14) * mm});
            skLineSegment(sketch, "E1580", {"start": v(2.77, -4.14) * mm, "end": v(2.77, -4.12) * mm});
            skLineSegment(sketch, "E1581", {"start": v(2.77, -4.12) * mm, "end": v(2.77, -4.1) * mm});
            skLineSegment(sketch, "E1582", {"start": v(2.77, -4.1) * mm, "end": v(2.77, -4.08) * mm});
            skLineSegment(sketch, "E1583", {"start": v(2.77, -4.08) * mm, "end": v(2.76, -4.06) * mm});
            skLineSegment(sketch, "E1584", {"start": v(2.76, -4.06) * mm, "end": v(2.76, -4.04) * mm});
            skLineSegment(sketch, "E1585", {"start": v(2.76, -4.04) * mm, "end": v(2.76, -4.03) * mm});
            skLineSegment(sketch, "E1586", {"start": v(2.76, -4.03) * mm, "end": v(2.75, -4) * mm});
            skLineSegment(sketch, "E1587", {"start": v(2.75, -4) * mm, "end": v(2.75, -4) * mm});
            skLineSegment(sketch, "E1588", {"start": v(2.75, -4) * mm, "end": v(2.75, -3.98) * mm});
            skLineSegment(sketch, "E1589", {"start": v(2.75, -3.98) * mm, "end": v(2.74, -3.96) * mm});
            skLineSegment(sketch, "E1590", {"start": v(2.74, -3.96) * mm, "end": v(2.74, -3.95) * mm});
            skLineSegment(sketch, "E1591", {"start": v(2.74, -3.95) * mm, "end": v(2.74, -3.93) * mm});
            skLineSegment(sketch, "E1592", {"start": v(2.74, -3.93) * mm, "end": v(2.73, -3.92) * mm});
            skLineSegment(sketch, "E1593", {"start": v(2.73, -3.92) * mm, "end": v(2.73, -3.9) * mm});
            skLineSegment(sketch, "E1594", {"start": v(2.73, -3.9) * mm, "end": v(2.73, -3.89) * mm});
            skLineSegment(sketch, "E1595", {"start": v(2.73, -3.89) * mm, "end": v(2.72, -3.87) * mm});
            skLineSegment(sketch, "E1596", {"start": v(2.72, -3.87) * mm, "end": v(2.72, -3.87) * mm});
            skLineSegment(sketch, "E1597", {"start": v(2.72, -3.87) * mm, "end": v(2.76, -3.83) * mm});
            skLineSegment(sketch, "E1598", {"start": v(2.76, -3.83) * mm, "end": v(2.77, -3.82) * mm});
            skLineSegment(sketch, "E1599", {"start": v(2.77, -3.82) * mm, "end": v(2.82, -3.8) * mm});
            skLineSegment(sketch, "E1600", {"start": v(2.82, -3.8) * mm, "end": v(2.83, -3.8) * mm});
            skLineSegment(sketch, "E1601", {"start": v(2.83, -3.8) * mm, "end": v(2.84, -3.8) * mm});
            skLineSegment(sketch, "E1602", {"start": v(2.84, -3.8) * mm, "end": v(2.85, -3.81) * mm});
            skLineSegment(sketch, "E1603", {"start": v(2.85, -3.81) * mm, "end": v(2.87, -3.82) * mm});
            skLineSegment(sketch, "E1604", {"start": v(2.87, -3.82) * mm, "end": v(2.88, -3.83) * mm});
            skLineSegment(sketch, "E1605", {"start": v(2.88, -3.83) * mm, "end": v(2.9, -3.84) * mm});
            skLineSegment(sketch, "E1606", {"start": v(2.9, -3.84) * mm, "end": v(2.9, -3.84) * mm});
            skLineSegment(sketch, "E1607", {"start": v(2.9, -3.84) * mm, "end": v(2.92, -3.85) * mm});
            skLineSegment(sketch, "E1608", {"start": v(2.92, -3.85) * mm, "end": v(2.93, -3.86) * mm});
            skLineSegment(sketch, "E1609", {"start": v(2.93, -3.86) * mm, "end": v(2.95, -3.87) * mm});
            skLineSegment(sketch, "E1610", {"start": v(2.95, -3.87) * mm, "end": v(2.96, -3.88) * mm});
            skLineSegment(sketch, "E1611", {"start": v(2.96, -3.88) * mm, "end": v(2.98, -3.89) * mm});
            skLineSegment(sketch, "E1612", {"start": v(2.98, -3.89) * mm, "end": v(3, -3.9) * mm});
            skLineSegment(sketch, "E1613", {"start": v(3, -3.9) * mm, "end": v(3.01, -3.9) * mm});
            skLineSegment(sketch, "E1614", {"start": v(3.01, -3.9) * mm, "end": v(3.03, -3.91) * mm});
            skLineSegment(sketch, "E1615", {"start": v(3.03, -3.91) * mm, "end": v(3.04, -3.92) * mm});
            skLineSegment(sketch, "E1616", {"start": v(3.04, -3.92) * mm, "end": v(3.06, -3.93) * mm});
            skLineSegment(sketch, "E1617", {"start": v(3.06, -3.93) * mm, "end": v(3.08, -3.94) * mm});
            skLineSegment(sketch, "E1618", {"start": v(3.08, -3.94) * mm, "end": v(3.1, -3.94) * mm});
            skLineSegment(sketch, "E1619", {"start": v(3.1, -3.94) * mm, "end": v(3.12, -3.95) * mm});
            skLineSegment(sketch, "E1620", {"start": v(3.12, -3.95) * mm, "end": v(3.14, -3.96) * mm});
            skLineSegment(sketch, "E1621", {"start": v(3.14, -3.96) * mm, "end": v(3.15, -3.97) * mm});
            skLineSegment(sketch, "E1622", {"start": v(3.15, -3.97) * mm, "end": v(3.17, -3.98) * mm});
            skLineSegment(sketch, "E1623", {"start": v(3.17, -3.98) * mm, "end": v(3.2, -3.99) * mm});
            skLineSegment(sketch, "E1624", {"start": v(3.2, -3.99) * mm, "end": v(3.21, -4) * mm});
            skLineSegment(sketch, "E1625", {"start": v(3.21, -4) * mm, "end": v(3.24, -4) * mm});
            skLineSegment(sketch, "E1626", {"start": v(3.24, -4) * mm, "end": v(3.26, -4) * mm});
            skLineSegment(sketch, "E1627", {"start": v(3.26, -4) * mm, "end": v(3.28, -4.02) * mm});
            skLineSegment(sketch, "E1628", {"start": v(3.28, -4.02) * mm, "end": v(3.3, -4.03) * mm});
            skLineSegment(sketch, "E1629", {"start": v(3.3, -4.03) * mm, "end": v(3.32, -4.03) * mm});
            skLineSegment(sketch, "E1630", {"start": v(3.32, -4.03) * mm, "end": v(3.35, -4.04) * mm});
            skLineSegment(sketch, "E1631", {"start": v(3.35, -4.04) * mm, "end": v(3.37, -4.04) * mm});
            skLineSegment(sketch, "E1632", {"start": v(3.37, -4.04) * mm, "end": v(3.45, -3.97) * mm});
            skLineSegment(sketch, "E1633", {"start": v(3.45, -3.97) * mm, "end": v(3.45, -3.95) * mm});
            skLineSegment(sketch, "E1634", {"start": v(3.45, -3.95) * mm, "end": v(3.45, -3.92) * mm});
            skLineSegment(sketch, "E1635", {"start": v(3.45, -3.92) * mm, "end": v(3.45, -3.9) * mm});
            skLineSegment(sketch, "E1636", {"start": v(3.45, -3.9) * mm, "end": v(3.44, -3.88) * mm});
            skLineSegment(sketch, "E1637", {"start": v(3.44, -3.88) * mm, "end": v(3.44, -3.86) * mm});
            skLineSegment(sketch, "E1638", {"start": v(3.44, -3.86) * mm, "end": v(3.43, -3.83) * mm});
            skLineSegment(sketch, "E1639", {"start": v(3.43, -3.83) * mm, "end": v(3.43, -3.81) * mm});
            skLineSegment(sketch, "E1640", {"start": v(3.43, -3.81) * mm, "end": v(3.42, -3.8) * mm});
            skLineSegment(sketch, "E1641", {"start": v(3.42, -3.8) * mm, "end": v(3.42, -3.77) * mm});
            skLineSegment(sketch, "E1642", {"start": v(3.42, -3.77) * mm, "end": v(3.41, -3.75) * mm});
            skLineSegment(sketch, "E1643", {"start": v(3.41, -3.75) * mm, "end": v(3.4, -3.73) * mm});
            skLineSegment(sketch, "E1644", {"start": v(3.4, -3.73) * mm, "end": v(3.4, -3.7) * mm});
            skLineSegment(sketch, "E1645", {"start": v(3.4, -3.7) * mm, "end": v(3.4, -3.69) * mm});
            skLineSegment(sketch, "E1646", {"start": v(3.4, -3.69) * mm, "end": v(3.4, -3.67) * mm});
            skLineSegment(sketch, "E1647", {"start": v(3.4, -3.67) * mm, "end": v(3.39, -3.65) * mm});
            skLineSegment(sketch, "E1648", {"start": v(3.39, -3.65) * mm, "end": v(3.38, -3.63) * mm});
            skLineSegment(sketch, "E1649", {"start": v(3.38, -3.63) * mm, "end": v(3.38, -3.61) * mm});
            skLineSegment(sketch, "E1650", {"start": v(3.38, -3.61) * mm, "end": v(3.37, -3.6) * mm});
            skLineSegment(sketch, "E1651", {"start": v(3.37, -3.6) * mm, "end": v(3.36, -3.58) * mm});
            skLineSegment(sketch, "E1652", {"start": v(3.36, -3.58) * mm, "end": v(3.36, -3.56) * mm});
            skLineSegment(sketch, "E1653", {"start": v(3.36, -3.56) * mm, "end": v(3.35, -3.55) * mm});
            skLineSegment(sketch, "E1654", {"start": v(3.35, -3.55) * mm, "end": v(3.35, -3.53) * mm});
            skLineSegment(sketch, "E1655", {"start": v(3.35, -3.53) * mm, "end": v(3.34, -3.51) * mm});
            skLineSegment(sketch, "E1656", {"start": v(3.34, -3.51) * mm, "end": v(3.34, -3.5) * mm});
            skLineSegment(sketch, "E1657", {"start": v(3.34, -3.5) * mm, "end": v(3.33, -3.48) * mm});
            skLineSegment(sketch, "E1658", {"start": v(3.33, -3.48) * mm, "end": v(3.32, -3.47) * mm});
            skLineSegment(sketch, "E1659", {"start": v(3.32, -3.47) * mm, "end": v(3.32, -3.45) * mm});
            skLineSegment(sketch, "E1660", {"start": v(3.32, -3.45) * mm, "end": v(3.31, -3.44) * mm});
            skLineSegment(sketch, "E1661", {"start": v(3.31, -3.44) * mm, "end": v(3.3, -3.43) * mm});
            skLineSegment(sketch, "E1662", {"start": v(3.3, -3.43) * mm, "end": v(3.3, -3.41) * mm});
            skLineSegment(sketch, "E1663", {"start": v(3.3, -3.41) * mm, "end": v(3.3, -3.4) * mm});
            skLineSegment(sketch, "E1664", {"start": v(3.3, -3.4) * mm, "end": v(3.3, -3.4) * mm});
            skLineSegment(sketch, "E1665", {"start": v(3.3, -3.4) * mm, "end": v(3.33, -3.35) * mm});
            skLineSegment(sketch, "E1666", {"start": v(3.33, -3.35) * mm, "end": v(3.34, -3.34) * mm});
            skLineSegment(sketch, "E1667", {"start": v(3.34, -3.34) * mm, "end": v(3.38, -3.3) * mm});
            skLineSegment(sketch, "E1668", {"start": v(3.38, -3.3) * mm, "end": v(3.39, -3.3) * mm});
            skLineSegment(sketch, "E1669", {"start": v(3.39, -3.3) * mm, "end": v(3.4, -3.31) * mm});
            skLineSegment(sketch, "E1670", {"start": v(3.4, -3.31) * mm, "end": v(3.41, -3.32) * mm});
            skLineSegment(sketch, "E1671", {"start": v(3.41, -3.32) * mm, "end": v(3.43, -3.32) * mm});
            skLineSegment(sketch, "E1672", {"start": v(3.43, -3.32) * mm, "end": v(3.44, -3.33) * mm});
            skLineSegment(sketch, "E1673", {"start": v(3.44, -3.33) * mm, "end": v(3.46, -3.34) * mm});
            skLineSegment(sketch, "E1674", {"start": v(3.46, -3.34) * mm, "end": v(3.47, -3.34) * mm});
            skLineSegment(sketch, "E1675", {"start": v(3.47, -3.34) * mm, "end": v(3.49, -3.35) * mm});
            skLineSegment(sketch, "E1676", {"start": v(3.49, -3.35) * mm, "end": v(3.5, -3.35) * mm});
            skLineSegment(sketch, "E1677", {"start": v(3.5, -3.35) * mm, "end": v(3.52, -3.36) * mm});
            skLineSegment(sketch, "E1678", {"start": v(3.52, -3.36) * mm, "end": v(3.53, -3.37) * mm});
            skLineSegment(sketch, "E1679", {"start": v(3.53, -3.37) * mm, "end": v(3.55, -3.37) * mm});
            skLineSegment(sketch, "E1680", {"start": v(3.55, -3.37) * mm, "end": v(3.57, -3.38) * mm});
            skLineSegment(sketch, "E1681", {"start": v(3.57, -3.38) * mm, "end": v(3.58, -3.38) * mm});
            skLineSegment(sketch, "E1682", {"start": v(3.58, -3.38) * mm, "end": v(3.6, -3.39) * mm});
            skLineSegment(sketch, "E1683", {"start": v(3.6, -3.39) * mm, "end": v(3.62, -3.4) * mm});
            skLineSegment(sketch, "E1684", {"start": v(3.62, -3.4) * mm, "end": v(3.64, -3.4) * mm});
            skLineSegment(sketch, "E1685", {"start": v(3.64, -3.4) * mm, "end": v(3.66, -3.4) * mm});
            skLineSegment(sketch, "E1686", {"start": v(3.66, -3.4) * mm, "end": v(3.68, -3.41) * mm});
            skLineSegment(sketch, "E1687", {"start": v(3.68, -3.41) * mm, "end": v(3.7, -3.42) * mm});
            skLineSegment(sketch, "E1688", {"start": v(3.7, -3.42) * mm, "end": v(3.72, -3.42) * mm});
            skLineSegment(sketch, "E1689", {"start": v(3.72, -3.42) * mm, "end": v(3.74, -3.43) * mm});
            skLineSegment(sketch, "E1690", {"start": v(3.74, -3.43) * mm, "end": v(3.76, -3.43) * mm});
            skLineSegment(sketch, "E1691", {"start": v(3.76, -3.43) * mm, "end": v(3.78, -3.44) * mm});
            skLineSegment(sketch, "E1692", {"start": v(3.78, -3.44) * mm, "end": v(3.8, -3.44) * mm});
            skLineSegment(sketch, "E1693", {"start": v(3.8, -3.44) * mm, "end": v(3.82, -3.45) * mm});
            skLineSegment(sketch, "E1694", {"start": v(3.82, -3.45) * mm, "end": v(3.84, -3.45) * mm});
            skLineSegment(sketch, "E1695", {"start": v(3.84, -3.45) * mm, "end": v(3.87, -3.45) * mm});
            skLineSegment(sketch, "E1696", {"start": v(3.87, -3.45) * mm, "end": v(3.89, -3.46) * mm});
            skLineSegment(sketch, "E1697", {"start": v(3.89, -3.46) * mm, "end": v(3.91, -3.46) * mm});
            skLineSegment(sketch, "E1698", {"start": v(3.91, -3.46) * mm, "end": v(3.94, -3.47) * mm});
            skLineSegment(sketch, "E1699", {"start": v(3.94, -3.47) * mm, "end": v(3.96, -3.46) * mm});
            skLineSegment(sketch, "E1700", {"start": v(3.96, -3.46) * mm, "end": v(4.03, -3.38) * mm});
            skLineSegment(sketch, "E1701", {"start": v(4.03, -3.38) * mm, "end": v(4.03, -3.36) * mm});
            skLineSegment(sketch, "E1702", {"start": v(4.03, -3.36) * mm, "end": v(4.02, -3.34) * mm});
            skLineSegment(sketch, "E1703", {"start": v(4.02, -3.34) * mm, "end": v(4.01, -3.31) * mm});
            skLineSegment(sketch, "E1704", {"start": v(4.01, -3.31) * mm, "end": v(4, -3.3) * mm});
            skLineSegment(sketch, "E1705", {"start": v(4, -3.3) * mm, "end": v(4, -3.27) * mm});
            skLineSegment(sketch, "E1706", {"start": v(4, -3.27) * mm, "end": v(3.99, -3.25) * mm});
            skLineSegment(sketch, "E1707", {"start": v(3.99, -3.25) * mm, "end": v(3.98, -3.23) * mm});
            skLineSegment(sketch, "E1708", {"start": v(3.98, -3.23) * mm, "end": v(3.97, -3.2) * mm});
            skLineSegment(sketch, "E1709", {"start": v(3.97, -3.2) * mm, "end": v(3.97, -3.19) * mm});
            skLineSegment(sketch, "E1710", {"start": v(3.97, -3.19) * mm, "end": v(3.96, -3.17) * mm});
            skLineSegment(sketch, "E1711", {"start": v(3.96, -3.17) * mm, "end": v(3.95, -3.15) * mm});
            skLineSegment(sketch, "E1712", {"start": v(3.95, -3.15) * mm, "end": v(3.94, -3.13) * mm});
            skLineSegment(sketch, "E1713", {"start": v(3.94, -3.13) * mm, "end": v(3.93, -3.11) * mm});
            skLineSegment(sketch, "E1714", {"start": v(3.93, -3.11) * mm, "end": v(3.92, -3.1) * mm});
            skLineSegment(sketch, "E1715", {"start": v(3.92, -3.1) * mm, "end": v(3.92, -3.08) * mm});
            skLineSegment(sketch, "E1716", {"start": v(3.92, -3.08) * mm, "end": v(3.9, -3.06) * mm});
            skLineSegment(sketch, "E1717", {"start": v(3.9, -3.06) * mm, "end": v(3.9, -3.04) * mm});
            skLineSegment(sketch, "E1718", {"start": v(3.9, -3.04) * mm, "end": v(3.9, -3.02) * mm});
            skLineSegment(sketch, "E1719", {"start": v(3.9, -3.02) * mm, "end": v(3.88, -3) * mm});
            skLineSegment(sketch, "E1720", {"start": v(3.88, -3) * mm, "end": v(3.87, -3) * mm});
            skLineSegment(sketch, "E1721", {"start": v(3.87, -3) * mm, "end": v(3.87, -2.98) * mm});
            skLineSegment(sketch, "E1722", {"start": v(3.87, -2.98) * mm, "end": v(3.86, -2.96) * mm});
            skLineSegment(sketch, "E1723", {"start": v(3.86, -2.96) * mm, "end": v(3.85, -2.95) * mm});
            skLineSegment(sketch, "E1724", {"start": v(3.85, -2.95) * mm, "end": v(3.84, -2.93) * mm});
            skLineSegment(sketch, "E1725", {"start": v(3.84, -2.93) * mm, "end": v(3.83, -2.92) * mm});
            skLineSegment(sketch, "E1726", {"start": v(3.83, -2.92) * mm, "end": v(3.83, -2.9) * mm});
            skLineSegment(sketch, "E1727", {"start": v(3.83, -2.9) * mm, "end": v(3.82, -2.9) * mm});
            skLineSegment(sketch, "E1728", {"start": v(3.82, -2.9) * mm, "end": v(3.8, -2.88) * mm});
            skLineSegment(sketch, "E1729", {"start": v(3.8, -2.88) * mm, "end": v(3.8, -2.87) * mm});
            skLineSegment(sketch, "E1730", {"start": v(3.8, -2.87) * mm, "end": v(3.8, -2.85) * mm});
            skLineSegment(sketch, "E1731", {"start": v(3.8, -2.85) * mm, "end": v(3.79, -2.84) * mm});
            skLineSegment(sketch, "E1732", {"start": v(3.79, -2.84) * mm, "end": v(3.78, -2.84) * mm});
            skLineSegment(sketch, "E1733", {"start": v(3.78, -2.84) * mm, "end": v(3.81, -2.79) * mm});
            skLineSegment(sketch, "E1734", {"start": v(3.81, -2.79) * mm, "end": v(3.82, -2.78) * mm});
            skLineSegment(sketch, "E1735", {"start": v(3.82, -2.78) * mm, "end": v(3.86, -2.73) * mm});
            skLineSegment(sketch, "E1736", {"start": v(3.86, -2.73) * mm, "end": v(3.86, -2.74) * mm});
            skLineSegment(sketch, "E1737", {"start": v(3.86, -2.74) * mm, "end": v(3.88, -2.74) * mm});
            skLineSegment(sketch, "E1738", {"start": v(3.88, -2.74) * mm, "end": v(3.9, -2.74) * mm});
            skLineSegment(sketch, "E1739", {"start": v(3.9, -2.74) * mm, "end": v(3.9, -2.75) * mm});
            skLineSegment(sketch, "E1740", {"start": v(3.9, -2.75) * mm, "end": v(3.92, -2.75) * mm});
            skLineSegment(sketch, "E1741", {"start": v(3.92, -2.75) * mm, "end": v(3.94, -2.75) * mm});
            skLineSegment(sketch, "E1742", {"start": v(3.94, -2.75) * mm, "end": v(3.95, -2.76) * mm});
            skLineSegment(sketch, "E1743", {"start": v(3.95, -2.76) * mm, "end": v(3.97, -2.76) * mm});
            skLineSegment(sketch, "E1744", {"start": v(3.97, -2.76) * mm, "end": v(3.98, -2.76) * mm});
            skLineSegment(sketch, "E1745", {"start": v(3.98, -2.76) * mm, "end": v(4, -2.77) * mm});
            skLineSegment(sketch, "E1746", {"start": v(4, -2.77) * mm, "end": v(4.02, -2.77) * mm});
            skLineSegment(sketch, "E1747", {"start": v(4.02, -2.77) * mm, "end": v(4.03, -2.77) * mm});
            skLineSegment(sketch, "E1748", {"start": v(4.03, -2.77) * mm, "end": v(4.05, -2.78) * mm});
            skLineSegment(sketch, "E1749", {"start": v(4.05, -2.78) * mm, "end": v(4.07, -2.78) * mm});
            skLineSegment(sketch, "E1750", {"start": v(4.07, -2.78) * mm, "end": v(4.09, -2.78) * mm});
            skLineSegment(sketch, "E1751", {"start": v(4.09, -2.78) * mm, "end": v(4.1, -2.79) * mm});
            skLineSegment(sketch, "E1752", {"start": v(4.1, -2.79) * mm, "end": v(4.13, -2.79) * mm});
            skLineSegment(sketch, "E1753", {"start": v(4.13, -2.79) * mm, "end": v(4.14, -2.8) * mm});
            skLineSegment(sketch, "E1754", {"start": v(4.14, -2.8) * mm, "end": v(4.16, -2.8) * mm});
            skLineSegment(sketch, "E1755", {"start": v(4.16, -2.8) * mm, "end": v(4.18, -2.8) * mm});
            skLineSegment(sketch, "E1756", {"start": v(4.18, -2.8) * mm, "end": v(4.2, -2.8) * mm});
            skLineSegment(sketch, "E1757", {"start": v(4.2, -2.8) * mm, "end": v(4.23, -2.8) * mm});
            skLineSegment(sketch, "E1758", {"start": v(4.23, -2.8) * mm, "end": v(4.25, -2.8) * mm});
            skLineSegment(sketch, "E1759", {"start": v(4.25, -2.8) * mm, "end": v(4.27, -2.8) * mm});
            skLineSegment(sketch, "E1760", {"start": v(4.27, -2.8) * mm, "end": v(4.3, -2.8) * mm});
            skLineSegment(sketch, "E1761", {"start": v(4.3, -2.8) * mm, "end": v(4.31, -2.8) * mm});
            skLineSegment(sketch, "E1762", {"start": v(4.31, -2.8) * mm, "end": v(4.34, -2.8) * mm});
            skLineSegment(sketch, "E1763", {"start": v(4.34, -2.8) * mm, "end": v(4.36, -2.8) * mm});
            skLineSegment(sketch, "E1764", {"start": v(4.36, -2.8) * mm, "end": v(4.38, -2.8) * mm});
            skLineSegment(sketch, "E1765", {"start": v(4.38, -2.8) * mm, "end": v(4.4, -2.8) * mm});
            skLineSegment(sketch, "E1766", {"start": v(4.4, -2.8) * mm, "end": v(4.43, -2.8) * mm});
            skLineSegment(sketch, "E1767", {"start": v(4.43, -2.8) * mm, "end": v(4.45, -2.8) * mm});
            skLineSegment(sketch, "E1768", {"start": v(4.45, -2.8) * mm, "end": v(4.5, -2.71) * mm});
            skLineSegment(sketch, "E1769", {"start": v(4.5, -2.71) * mm, "end": v(4.5, -2.69) * mm});
            skLineSegment(sketch, "E1770", {"start": v(4.5, -2.69) * mm, "end": v(4.5, -2.67) * mm});
            skLineSegment(sketch, "E1771", {"start": v(4.5, -2.67) * mm, "end": v(4.48, -2.65) * mm});
            skLineSegment(sketch, "E1772", {"start": v(4.48, -2.65) * mm, "end": v(4.47, -2.62) * mm});
            skLineSegment(sketch, "E1773", {"start": v(4.47, -2.62) * mm, "end": v(4.46, -2.6) * mm});
            skLineSegment(sketch, "E1774", {"start": v(4.46, -2.6) * mm, "end": v(4.45, -2.59) * mm});
            skLineSegment(sketch, "E1775", {"start": v(4.45, -2.59) * mm, "end": v(4.44, -2.57) * mm});
            skLineSegment(sketch, "E1776", {"start": v(4.44, -2.57) * mm, "end": v(4.43, -2.55) * mm});
            skLineSegment(sketch, "E1777", {"start": v(4.43, -2.55) * mm, "end": v(4.42, -2.53) * mm});
            skLineSegment(sketch, "E1778", {"start": v(4.42, -2.53) * mm, "end": v(4.4, -2.51) * mm});
            skLineSegment(sketch, "E1779", {"start": v(4.4, -2.51) * mm, "end": v(4.4, -2.5) * mm});
            skLineSegment(sketch, "E1780", {"start": v(4.4, -2.5) * mm, "end": v(4.38, -2.48) * mm});
            skLineSegment(sketch, "E1781", {"start": v(4.38, -2.48) * mm, "end": v(4.37, -2.46) * mm});
            skLineSegment(sketch, "E1782", {"start": v(4.37, -2.46) * mm, "end": v(4.36, -2.44) * mm});
            skLineSegment(sketch, "E1783", {"start": v(4.36, -2.44) * mm, "end": v(4.35, -2.43) * mm});
            skLineSegment(sketch, "E1784", {"start": v(4.35, -2.43) * mm, "end": v(4.34, -2.4) * mm});
            skLineSegment(sketch, "E1785", {"start": v(4.34, -2.4) * mm, "end": v(4.33, -2.4) * mm});
            skLineSegment(sketch, "E1786", {"start": v(4.33, -2.4) * mm, "end": v(4.32, -2.38) * mm});
            skLineSegment(sketch, "E1787", {"start": v(4.32, -2.38) * mm, "end": v(4.3, -2.36) * mm});
            skLineSegment(sketch, "E1788", {"start": v(4.3, -2.36) * mm, "end": v(4.3, -2.35) * mm});
            skLineSegment(sketch, "E1789", {"start": v(4.3, -2.35) * mm, "end": v(4.28, -2.34) * mm});
            skLineSegment(sketch, "E1790", {"start": v(4.28, -2.34) * mm, "end": v(4.27, -2.32) * mm});
            skLineSegment(sketch, "E1791", {"start": v(4.27, -2.32) * mm, "end": v(4.26, -2.3) * mm});
            skLineSegment(sketch, "E1792", {"start": v(4.26, -2.3) * mm, "end": v(4.25, -2.3) * mm});
            skLineSegment(sketch, "E1793", {"start": v(4.25, -2.3) * mm, "end": v(4.24, -2.28) * mm});
            skLineSegment(sketch, "E1794", {"start": v(4.24, -2.28) * mm, "end": v(4.23, -2.27) * mm});
            skLineSegment(sketch, "E1795", {"start": v(4.23, -2.27) * mm, "end": v(4.22, -2.26) * mm});
            skLineSegment(sketch, "E1796", {"start": v(4.22, -2.26) * mm, "end": v(4.21, -2.25) * mm});
            skLineSegment(sketch, "E1797", {"start": v(4.21, -2.25) * mm, "end": v(4.2, -2.24) * mm});
            skLineSegment(sketch, "E1798", {"start": v(4.2, -2.24) * mm, "end": v(4.2, -2.23) * mm});
            skLineSegment(sketch, "E1799", {"start": v(4.2, -2.23) * mm, "end": v(4.18, -2.22) * mm});
            skLineSegment(sketch, "E1800", {"start": v(4.18, -2.22) * mm, "end": v(4.18, -2.2) * mm});
            skLineSegment(sketch, "E1801", {"start": v(4.18, -2.2) * mm, "end": v(4.2, -2.16) * mm});
            skLineSegment(sketch, "E1802", {"start": v(4.2, -2.16) * mm, "end": v(4.2, -2.14) * mm});
            skLineSegment(sketch, "E1803", {"start": v(4.2, -2.14) * mm, "end": v(4.24, -2.1) * mm});
            skLineSegment(sketch, "E1804", {"start": v(4.24, -2.1) * mm, "end": v(4.24, -2.1) * mm});
            skLineSegment(sketch, "E1805", {"start": v(4.24, -2.1) * mm, "end": v(4.26, -2.1) * mm});
            skLineSegment(sketch, "E1806", {"start": v(4.26, -2.1) * mm, "end": v(4.27, -2.1) * mm});
            skLineSegment(sketch, "E1807", {"start": v(4.27, -2.1) * mm, "end": v(4.29, -2.1) * mm});
            skLineSegment(sketch, "E1808", {"start": v(4.29, -2.1) * mm, "end": v(4.3, -2.1) * mm});
            skLineSegment(sketch, "E1809", {"start": v(4.3, -2.1) * mm, "end": v(4.32, -2.1) * mm});
            skLineSegment(sketch, "E1810", {"start": v(4.32, -2.1) * mm, "end": v(4.33, -2.1) * mm});
            skLineSegment(sketch, "E1811", {"start": v(4.33, -2.1) * mm, "end": v(4.35, -2.1) * mm});
            skLineSegment(sketch, "E1812", {"start": v(4.35, -2.1) * mm, "end": v(4.37, -2.1) * mm});
            skLineSegment(sketch, "E1813", {"start": v(4.37, -2.1) * mm, "end": v(4.38, -2.1) * mm});
            skLineSegment(sketch, "E1814", {"start": v(4.38, -2.1) * mm, "end": v(4.4, -2.1) * mm});
            skLineSegment(sketch, "E1815", {"start": v(4.4, -2.1) * mm, "end": v(4.42, -2.1) * mm});
            skLineSegment(sketch, "E1816", {"start": v(4.42, -2.1) * mm, "end": v(4.44, -2.1) * mm});
            skLineSegment(sketch, "E1817", {"start": v(4.44, -2.1) * mm, "end": v(4.45, -2.1) * mm});
            skLineSegment(sketch, "E1818", {"start": v(4.45, -2.1) * mm, "end": v(4.47, -2.1) * mm});
            skLineSegment(sketch, "E1819", {"start": v(4.47, -2.1) * mm, "end": v(4.5, -2.1) * mm});
            skLineSegment(sketch, "E1820", {"start": v(4.5, -2.1) * mm, "end": v(4.51, -2.1) * mm});
            skLineSegment(sketch, "E1821", {"start": v(4.51, -2.1) * mm, "end": v(4.53, -2.1) * mm});
            skLineSegment(sketch, "E1822", {"start": v(4.53, -2.1) * mm, "end": v(4.55, -2.1) * mm});
            skLineSegment(sketch, "E1823", {"start": v(4.55, -2.1) * mm, "end": v(4.57, -2.1) * mm});
            skLineSegment(sketch, "E1824", {"start": v(4.57, -2.1) * mm, "end": v(4.6, -2.1) * mm});
            skLineSegment(sketch, "E1825", {"start": v(4.6, -2.1) * mm, "end": v(4.61, -2.1) * mm});
            skLineSegment(sketch, "E1826", {"start": v(4.61, -2.1) * mm, "end": v(4.63, -2.1) * mm});
            skLineSegment(sketch, "E1827", {"start": v(4.63, -2.1) * mm, "end": v(4.65, -2.1) * mm});
            skLineSegment(sketch, "E1828", {"start": v(4.65, -2.1) * mm, "end": v(4.68, -2.1) * mm});
            skLineSegment(sketch, "E1829", {"start": v(4.68, -2.1) * mm, "end": v(4.7, -2.1) * mm});
            skLineSegment(sketch, "E1830", {"start": v(4.7, -2.1) * mm, "end": v(4.72, -2.1) * mm});
            skLineSegment(sketch, "E1831", {"start": v(4.72, -2.1) * mm, "end": v(4.74, -2.1) * mm});
            skLineSegment(sketch, "E1832", {"start": v(4.74, -2.1) * mm, "end": v(4.77, -2.09) * mm});
            skLineSegment(sketch, "E1833", {"start": v(4.77, -2.09) * mm, "end": v(4.8, -2.08) * mm});
            skLineSegment(sketch, "E1834", {"start": v(4.8, -2.08) * mm, "end": v(4.82, -2.08) * mm});
            skLineSegment(sketch, "E1835", {"start": v(4.82, -2.08) * mm, "end": v(4.83, -2.07) * mm});
            skLineSegment(sketch, "E1836", {"start": v(4.83, -2.07) * mm, "end": v(4.88, -1.97) * mm});
            skLineSegment(sketch, "E1837", {"start": v(4.88, -1.97) * mm, "end": v(4.87, -1.95) * mm});
            skLineSegment(sketch, "E1838", {"start": v(4.87, -1.95) * mm, "end": v(4.86, -1.93) * mm});
            skLineSegment(sketch, "E1839", {"start": v(4.86, -1.93) * mm, "end": v(4.84, -1.91) * mm});
            skLineSegment(sketch, "E1840", {"start": v(4.84, -1.91) * mm, "end": v(4.83, -1.9) * mm});
            skLineSegment(sketch, "E1841", {"start": v(4.83, -1.9) * mm, "end": v(4.81, -1.87) * mm});
            skLineSegment(sketch, "E1842", {"start": v(4.81, -1.87) * mm, "end": v(4.8, -1.86) * mm});
            skLineSegment(sketch, "E1843", {"start": v(4.8, -1.86) * mm, "end": v(4.78, -1.84) * mm});
            skLineSegment(sketch, "E1844", {"start": v(4.78, -1.84) * mm, "end": v(4.77, -1.82) * mm});
            skLineSegment(sketch, "E1845", {"start": v(4.77, -1.82) * mm, "end": v(4.76, -1.8) * mm});
            skLineSegment(sketch, "E1846", {"start": v(4.76, -1.8) * mm, "end": v(4.74, -1.8) * mm});
            skLineSegment(sketch, "E1847", {"start": v(4.74, -1.8) * mm, "end": v(4.73, -1.77) * mm});
            skLineSegment(sketch, "E1848", {"start": v(4.73, -1.77) * mm, "end": v(4.72, -1.76) * mm});
            skLineSegment(sketch, "E1849", {"start": v(4.72, -1.76) * mm, "end": v(4.7, -1.74) * mm});
            skLineSegment(sketch, "E1850", {"start": v(4.7, -1.74) * mm, "end": v(4.69, -1.73) * mm});
            skLineSegment(sketch, "E1851", {"start": v(4.69, -1.73) * mm, "end": v(4.67, -1.71) * mm});
            skLineSegment(sketch, "E1852", {"start": v(4.67, -1.71) * mm, "end": v(4.66, -1.7) * mm});
            skLineSegment(sketch, "E1853", {"start": v(4.66, -1.7) * mm, "end": v(4.65, -1.69) * mm});
            skLineSegment(sketch, "E1854", {"start": v(4.65, -1.69) * mm, "end": v(4.64, -1.67) * mm});
            skLineSegment(sketch, "E1855", {"start": v(4.64, -1.67) * mm, "end": v(4.62, -1.66) * mm});
            skLineSegment(sketch, "E1856", {"start": v(4.62, -1.66) * mm, "end": v(4.6, -1.65) * mm});
            skLineSegment(sketch, "E1857", {"start": v(4.6, -1.65) * mm, "end": v(4.6, -1.64) * mm});
            skLineSegment(sketch, "E1858", {"start": v(4.6, -1.64) * mm, "end": v(4.58, -1.62) * mm});
            skLineSegment(sketch, "E1859", {"start": v(4.58, -1.62) * mm, "end": v(4.57, -1.61) * mm});
            skLineSegment(sketch, "E1860", {"start": v(4.57, -1.61) * mm, "end": v(4.56, -1.6) * mm});
            skLineSegment(sketch, "E1861", {"start": v(4.56, -1.6) * mm, "end": v(4.55, -1.6) * mm});
            skLineSegment(sketch, "E1862", {"start": v(4.55, -1.6) * mm, "end": v(4.54, -1.58) * mm});
            skLineSegment(sketch, "E1863", {"start": v(4.54, -1.58) * mm, "end": v(4.52, -1.57) * mm});
            skLineSegment(sketch, "E1864", {"start": v(4.52, -1.57) * mm, "end": v(4.51, -1.56) * mm});
            skLineSegment(sketch, "E1865", {"start": v(4.51, -1.56) * mm, "end": v(4.5, -1.55) * mm});
            skLineSegment(sketch, "E1866", {"start": v(4.5, -1.55) * mm, "end": v(4.5, -1.54) * mm});
            skLineSegment(sketch, "E1867", {"start": v(4.5, -1.54) * mm, "end": v(4.48, -1.53) * mm});
            skLineSegment(sketch, "E1868", {"start": v(4.48, -1.53) * mm, "end": v(4.47, -1.53) * mm});
            skLineSegment(sketch, "E1869", {"start": v(4.47, -1.53) * mm, "end": v(4.49, -1.47) * mm});
            skLineSegment(sketch, "E1870", {"start": v(4.49, -1.47) * mm, "end": v(4.5, -1.46) * mm});
            skLineSegment(sketch, "E1871", {"start": v(4.5, -1.46) * mm, "end": v(4.51, -1.4) * mm});
            skLineSegment(sketch, "E1872", {"start": v(4.51, -1.4) * mm, "end": v(4.52, -1.4) * mm});
            skLineSegment(sketch, "E1873", {"start": v(4.52, -1.4) * mm, "end": v(4.53, -1.4) * mm});
            skLineSegment(sketch, "E1874", {"start": v(4.53, -1.4) * mm, "end": v(4.55, -1.4) * mm});
            skLineSegment(sketch, "E1875", {"start": v(4.55, -1.4) * mm, "end": v(4.56, -1.4) * mm});
            skLineSegment(sketch, "E1876", {"start": v(4.56, -1.4) * mm, "end": v(4.58, -1.4) * mm});
            skLineSegment(sketch, "E1877", {"start": v(4.58, -1.4) * mm, "end": v(4.6, -1.4) * mm});
            skLineSegment(sketch, "E1878", {"start": v(4.6, -1.4) * mm, "end": v(4.6, -1.4) * mm});
            skLineSegment(sketch, "E1879", {"start": v(4.6, -1.4) * mm, "end": v(4.63, -1.4) * mm});
            skLineSegment(sketch, "E1880", {"start": v(4.63, -1.4) * mm, "end": v(4.64, -1.4) * mm});
            skLineSegment(sketch, "E1881", {"start": v(4.64, -1.4) * mm, "end": v(4.66, -1.4) * mm});
            skLineSegment(sketch, "E1882", {"start": v(4.66, -1.4) * mm, "end": v(4.68, -1.4) * mm});
            skLineSegment(sketch, "E1883", {"start": v(4.68, -1.4) * mm, "end": v(4.7, -1.4) * mm});
            skLineSegment(sketch, "E1884", {"start": v(4.7, -1.4) * mm, "end": v(4.71, -1.39) * mm});
            skLineSegment(sketch, "E1885", {"start": v(4.71, -1.39) * mm, "end": v(4.73, -1.39) * mm});
            skLineSegment(sketch, "E1886", {"start": v(4.73, -1.39) * mm, "end": v(4.75, -1.38) * mm});
            skLineSegment(sketch, "E1887", {"start": v(4.75, -1.38) * mm, "end": v(4.77, -1.38) * mm});
            skLineSegment(sketch, "E1888", {"start": v(4.77, -1.38) * mm, "end": v(4.79, -1.38) * mm});
            skLineSegment(sketch, "E1889", {"start": v(4.79, -1.38) * mm, "end": v(4.8, -1.37) * mm});
            skLineSegment(sketch, "E1890", {"start": v(4.8, -1.37) * mm, "end": v(4.82, -1.37) * mm});
            skLineSegment(sketch, "E1891", {"start": v(4.82, -1.37) * mm, "end": v(4.84, -1.37) * mm});
            skLineSegment(sketch, "E1892", {"start": v(4.84, -1.37) * mm, "end": v(4.86, -1.36) * mm});
            skLineSegment(sketch, "E1893", {"start": v(4.86, -1.36) * mm, "end": v(4.88, -1.36) * mm});
            skLineSegment(sketch, "E1894", {"start": v(4.88, -1.36) * mm, "end": v(4.9, -1.35) * mm});
            skLineSegment(sketch, "E1895", {"start": v(4.9, -1.35) * mm, "end": v(4.93, -1.35) * mm});
            skLineSegment(sketch, "E1896", {"start": v(4.93, -1.35) * mm, "end": v(4.95, -1.34) * mm});
            skLineSegment(sketch, "E1897", {"start": v(4.95, -1.34) * mm, "end": v(4.97, -1.34) * mm});
            skLineSegment(sketch, "E1898", {"start": v(4.97, -1.34) * mm, "end": v(5, -1.33) * mm});
            skLineSegment(sketch, "E1899", {"start": v(5, -1.33) * mm, "end": v(5.01, -1.32) * mm});
            skLineSegment(sketch, "E1900", {"start": v(5.01, -1.32) * mm, "end": v(5.04, -1.32) * mm});
            skLineSegment(sketch, "E1901", {"start": v(5.04, -1.32) * mm, "end": v(5.06, -1.3) * mm});
            skLineSegment(sketch, "E1902", {"start": v(5.06, -1.3) * mm, "end": v(5.08, -1.3) * mm});
            skLineSegment(sketch, "E1903", {"start": v(5.08, -1.3) * mm, "end": v(5.1, -1.29) * mm});
            skLineSegment(sketch, "E1904", {"start": v(5.1, -1.29) * mm, "end": v(5.12, -1.18) * mm});
            skLineSegment(sketch, "E1905", {"start": v(5.12, -1.18) * mm, "end": v(5.12, -1.17) * mm});
            skLineSegment(sketch, "E1906", {"start": v(5.12, -1.17) * mm, "end": v(5.1, -1.15) * mm});
            skLineSegment(sketch, "E1907", {"start": v(5.1, -1.15) * mm, "end": v(5.08, -1.13) * mm});
            skLineSegment(sketch, "E1908", {"start": v(5.08, -1.13) * mm, "end": v(5.06, -1.11) * mm});
            skLineSegment(sketch, "E1909", {"start": v(5.06, -1.11) * mm, "end": v(5.05, -1.1) * mm});
            skLineSegment(sketch, "E1910", {"start": v(5.05, -1.1) * mm, "end": v(5.03, -1.08) * mm});
            skLineSegment(sketch, "E1911", {"start": v(5.03, -1.08) * mm, "end": v(5.01, -1.07) * mm});
            skLineSegment(sketch, "E1912", {"start": v(5.01, -1.07) * mm, "end": v(5, -1.05) * mm});
            skLineSegment(sketch, "E1913", {"start": v(5, -1.05) * mm, "end": v(4.98, -1.04) * mm});
            skLineSegment(sketch, "E1914", {"start": v(4.98, -1.04) * mm, "end": v(4.96, -1.03) * mm});
            skLineSegment(sketch, "E1915", {"start": v(4.96, -1.03) * mm, "end": v(4.95, -1.01) * mm});
            skLineSegment(sketch, "E1916", {"start": v(4.95, -1.01) * mm, "end": v(4.93, -1) * mm});
            skLineSegment(sketch, "E1917", {"start": v(4.93, -1) * mm, "end": v(4.92, -0.99) * mm});
            skLineSegment(sketch, "E1918", {"start": v(4.92, -0.99) * mm, "end": v(4.9, -0.97) * mm});
            skLineSegment(sketch, "E1919", {"start": v(4.9, -0.97) * mm, "end": v(4.89, -0.96) * mm});
            skLineSegment(sketch, "E1920", {"start": v(4.89, -0.96) * mm, "end": v(4.87, -0.95) * mm});
            skLineSegment(sketch, "E1921", {"start": v(4.87, -0.95) * mm, "end": v(4.86, -0.94) * mm});
            skLineSegment(sketch, "E1922", {"start": v(4.86, -0.94) * mm, "end": v(4.84, -0.93) * mm});
            skLineSegment(sketch, "E1923", {"start": v(4.84, -0.93) * mm, "end": v(4.83, -0.92) * mm});
            skLineSegment(sketch, "E1924", {"start": v(4.83, -0.92) * mm, "end": v(4.81, -0.9) * mm});
            skLineSegment(sketch, "E1925", {"start": v(4.81, -0.9) * mm, "end": v(4.8, -0.9) * mm});
            skLineSegment(sketch, "E1926", {"start": v(4.8, -0.9) * mm, "end": v(4.78, -0.89) * mm});
            skLineSegment(sketch, "E1927", {"start": v(4.78, -0.89) * mm, "end": v(4.77, -0.88) * mm});
            skLineSegment(sketch, "E1928", {"start": v(4.77, -0.88) * mm, "end": v(4.75, -0.87) * mm});
            skLineSegment(sketch, "E1929", {"start": v(4.75, -0.87) * mm, "end": v(4.74, -0.86) * mm});
            skLineSegment(sketch, "E1930", {"start": v(4.74, -0.86) * mm, "end": v(4.73, -0.85) * mm});
            skLineSegment(sketch, "E1931", {"start": v(4.73, -0.85) * mm, "end": v(4.71, -0.84) * mm});
            skLineSegment(sketch, "E1932", {"start": v(4.71, -0.84) * mm, "end": v(4.7, -0.84) * mm});
            skLineSegment(sketch, "E1933", {"start": v(4.7, -0.84) * mm, "end": v(4.69, -0.83) * mm});
            skLineSegment(sketch, "E1934", {"start": v(4.69, -0.83) * mm, "end": v(4.68, -0.82) * mm});
            skLineSegment(sketch, "E1935", {"start": v(4.68, -0.82) * mm, "end": v(4.66, -0.81) * mm});
            skLineSegment(sketch, "E1936", {"start": v(4.66, -0.81) * mm, "end": v(4.66, -0.8) * mm});
            skLineSegment(sketch, "E1937", {"start": v(4.66, -0.8) * mm, "end": v(4.66, -0.75) * mm});
            skLineSegment(sketch, "E1938", {"start": v(4.66, -0.75) * mm, "end": v(4.66, -0.74) * mm});
            skLineSegment(sketch, "E1939", {"start": v(4.66, -0.74) * mm, "end": v(4.68, -0.69) * mm});
            skLineSegment(sketch, "E1940", {"start": v(4.68, -0.69) * mm, "end": v(4.68, -0.68) * mm});
            skLineSegment(sketch, "E1941", {"start": v(4.68, -0.68) * mm, "end": v(4.7, -0.68) * mm});
            skLineSegment(sketch, "E1942", {"start": v(4.7, -0.68) * mm, "end": v(4.71, -0.68) * mm});
            skLineSegment(sketch, "E1943", {"start": v(4.71, -0.68) * mm, "end": v(4.73, -0.67) * mm});
            skLineSegment(sketch, "E1944", {"start": v(4.73, -0.67) * mm, "end": v(4.74, -0.67) * mm});
            skLineSegment(sketch, "E1945", {"start": v(4.74, -0.67) * mm, "end": v(4.76, -0.67) * mm});
            skLineSegment(sketch, "E1946", {"start": v(4.76, -0.67) * mm, "end": v(4.77, -0.66) * mm});
            skLineSegment(sketch, "E1947", {"start": v(4.77, -0.66) * mm, "end": v(4.79, -0.66) * mm});
            skLineSegment(sketch, "E1948", {"start": v(4.79, -0.66) * mm, "end": v(4.8, -0.65) * mm});
            skLineSegment(sketch, "E1949", {"start": v(4.8, -0.65) * mm, "end": v(4.82, -0.65) * mm});
            skLineSegment(sketch, "E1950", {"start": v(4.82, -0.65) * mm, "end": v(4.84, -0.65) * mm});
            skLineSegment(sketch, "E1951", {"start": v(4.84, -0.65) * mm, "end": v(4.85, -0.64) * mm});
            skLineSegment(sketch, "E1952", {"start": v(4.85, -0.64) * mm, "end": v(4.87, -0.64) * mm});
            skLineSegment(sketch, "E1953", {"start": v(4.87, -0.64) * mm, "end": v(4.89, -0.63) * mm});
            skLineSegment(sketch, "E1954", {"start": v(4.89, -0.63) * mm, "end": v(4.9, -0.62) * mm});
            skLineSegment(sketch, "E1955", {"start": v(4.9, -0.62) * mm, "end": v(4.92, -0.62) * mm});
            skLineSegment(sketch, "E1956", {"start": v(4.92, -0.62) * mm, "end": v(4.94, -0.61) * mm});
            skLineSegment(sketch, "E1957", {"start": v(4.94, -0.61) * mm, "end": v(4.96, -0.6) * mm});
            skLineSegment(sketch, "E1958", {"start": v(4.96, -0.6) * mm, "end": v(4.98, -0.6) * mm});
            skLineSegment(sketch, "E1959", {"start": v(4.98, -0.6) * mm, "end": v(5, -0.6) * mm});
            skLineSegment(sketch, "E1960", {"start": v(5, -0.6) * mm, "end": v(5.02, -0.58) * mm});
            skLineSegment(sketch, "E1961", {"start": v(5.02, -0.58) * mm, "end": v(5.04, -0.58) * mm});
            skLineSegment(sketch, "E1962", {"start": v(5.04, -0.58) * mm, "end": v(5.06, -0.57) * mm});
            skLineSegment(sketch, "E1963", {"start": v(5.06, -0.57) * mm, "end": v(5.08, -0.56) * mm});
            skLineSegment(sketch, "E1964", {"start": v(5.08, -0.56) * mm, "end": v(5.1, -0.55) * mm});
            skLineSegment(sketch, "E1965", {"start": v(5.1, -0.55) * mm, "end": v(5.12, -0.54) * mm});
            skLineSegment(sketch, "E1966", {"start": v(5.12, -0.54) * mm, "end": v(5.14, -0.53) * mm});
            skLineSegment(sketch, "E1967", {"start": v(5.14, -0.53) * mm, "end": v(5.16, -0.52) * mm});
            skLineSegment(sketch, "E1968", {"start": v(5.16, -0.52) * mm, "end": v(5.18, -0.51) * mm});
            skLineSegment(sketch, "E1969", {"start": v(5.18, -0.51) * mm, "end": v(5.2, -0.5) * mm});
            skLineSegment(sketch, "E1970", {"start": v(5.2, -0.5) * mm, "end": v(5.22, -0.5) * mm});
            skLineSegment(sketch, "E1971", {"start": v(5.22, -0.5) * mm, "end": v(5.24, -0.47) * mm});
            skLineSegment(sketch, "E1972", {"start": v(5.24, -0.47) * mm, "end": v(5.25, -0.37) * mm});
            skLineSegment(sketch, "E1973", {"start": v(5.25, -0.37) * mm, "end": v(5.24, -0.35) * mm});
            skLineSegment(sketch, "E1974", {"start": v(5.24, -0.35) * mm, "end": v(5.21, -0.34) * mm});
            skLineSegment(sketch, "E1975", {"start": v(5.21, -0.34) * mm, "end": v(5.2, -0.32) * mm});
            skLineSegment(sketch, "E1976", {"start": v(5.2, -0.32) * mm, "end": v(5.18, -0.3) * mm});
            skLineSegment(sketch, "E1977", {"start": v(5.18, -0.3) * mm, "end": v(5.16, -0.3) * mm});
            skLineSegment(sketch, "E1978", {"start": v(5.16, -0.3) * mm, "end": v(5.14, -0.28) * mm});
            skLineSegment(sketch, "E1979", {"start": v(5.14, -0.28) * mm, "end": v(5.12, -0.27) * mm});
            skLineSegment(sketch, "E1980", {"start": v(5.12, -0.27) * mm, "end": v(5.1, -0.26) * mm});
            skLineSegment(sketch, "E1981", {"start": v(5.1, -0.26) * mm, "end": v(5.08, -0.25) * mm});
            skLineSegment(sketch, "E1982", {"start": v(5.08, -0.25) * mm, "end": v(5.06, -0.24) * mm});
            skLineSegment(sketch, "E1983", {"start": v(5.06, -0.24) * mm, "end": v(5.05, -0.23) * mm});
            skLineSegment(sketch, "E1984", {"start": v(5.05, -0.23) * mm, "end": v(5.03, -0.22) * mm});
            skLineSegment(sketch, "E1985", {"start": v(5.03, -0.22) * mm, "end": v(5.01, -0.2) * mm});
            skLineSegment(sketch, "E1986", {"start": v(5.01, -0.2) * mm, "end": v(5, -0.2) * mm});
            skLineSegment(sketch, "E1987", {"start": v(5, -0.2) * mm, "end": v(4.98, -0.19) * mm});
            skLineSegment(sketch, "E1988", {"start": v(4.98, -0.19) * mm, "end": v(4.96, -0.18) * mm});
            skLineSegment(sketch, "E1989", {"start": v(4.96, -0.18) * mm, "end": v(4.94, -0.17) * mm});
            skLineSegment(sketch, "E1990", {"start": v(4.94, -0.17) * mm, "end": v(4.93, -0.16) * mm});
            skLineSegment(sketch, "E1991", {"start": v(4.93, -0.16) * mm, "end": v(4.9, -0.15) * mm});
            skLineSegment(sketch, "E1992", {"start": v(4.9, -0.15) * mm, "end": v(4.9, -0.14) * mm});
            skLineSegment(sketch, "E1993", {"start": v(4.9, -0.14) * mm, "end": v(4.88, -0.14) * mm});
            skLineSegment(sketch, "E1994", {"start": v(4.88, -0.14) * mm, "end": v(4.86, -0.13) * mm});
            skLineSegment(sketch, "E1995", {"start": v(4.86, -0.13) * mm, "end": v(4.85, -0.12) * mm});
            skLineSegment(sketch, "E1996", {"start": v(4.85, -0.12) * mm, "end": v(4.83, -0.11) * mm});
            skLineSegment(sketch, "E1997", {"start": v(4.83, -0.11) * mm, "end": v(4.82, -0.1) * mm});
            skLineSegment(sketch, "E1998", {"start": v(4.82, -0.1) * mm, "end": v(4.8, -0.1) * mm});
            skLineSegment(sketch, "E1999", {"start": v(4.8, -0.1) * mm, "end": v(4.79, -0.1) * mm});
            skLineSegment(sketch, "E2000", {"start": v(4.79, -0.1) * mm, "end": v(4.77, -0.09) * mm});
            skLineSegment(sketch, "E2001", {"start": v(4.77, -0.09) * mm, "end": v(4.76, -0.08) * mm});
            skLineSegment(sketch, "E2002", {"start": v(4.76, -0.08) * mm, "end": v(4.75, -0.08) * mm});
            skLineSegment(sketch, "E2003", {"start": v(4.75, -0.08) * mm, "end": v(4.73, -0.07) * mm});
            skLineSegment(sketch, "E2004", {"start": v(4.73, -0.07) * mm, "end": v(4.73, -0.07) * mm});
            skLineSegment(sketch, "E2005", {"start": v(4.73, -0.07) * mm, "end": v(4.72, -0.02) * mm});
            skLineSegment(sketch, "E2006", {"start": v(4.72, -0.02) * mm, "end": v(4.72, 0) * mm});
            skLineSegment(sketch, "E2007", {"start": v(4.72, 0) * mm, "end": v(4.73, 0.06) * mm});
            skLineSegment(sketch, "E2008", {"start": v(4.73, 0.06) * mm, "end": v(4.73, 0.06) * mm});
            skLineSegment(sketch, "E2009", {"start": v(4.73, 0.06) * mm, "end": v(4.75, 0.06) * mm});
            skLineSegment(sketch, "E2010", {"start": v(4.75, 0.06) * mm, "end": v(4.76, 0.07) * mm});
            skLineSegment(sketch, "E2011", {"start": v(4.76, 0.07) * mm, "end": v(4.77, 0.07) * mm});
            skLineSegment(sketch, "E2012", {"start": v(4.77, 0.07) * mm, "end": v(4.79, 0.08) * mm});
            skLineSegment(sketch, "E2013", {"start": v(4.79, 0.08) * mm, "end": v(4.8, 0.09) * mm});
            skLineSegment(sketch, "E2014", {"start": v(4.8, 0.09) * mm, "end": v(4.82, 0.1) * mm});
            skLineSegment(sketch, "E2015", {"start": v(4.82, 0.1) * mm, "end": v(4.83, 0.1) * mm});
            skLineSegment(sketch, "E2016", {"start": v(4.83, 0.1) * mm, "end": v(4.85, 0.1) * mm});
            skLineSegment(sketch, "E2017", {"start": v(4.85, 0.1) * mm, "end": v(4.86, 0.11) * mm});
            skLineSegment(sketch, "E2018", {"start": v(4.86, 0.11) * mm, "end": v(4.88, 0.12) * mm});
            skLineSegment(sketch, "E2019", {"start": v(4.88, 0.12) * mm, "end": v(4.9, 0.13) * mm});
            skLineSegment(sketch, "E2020", {"start": v(4.9, 0.13) * mm, "end": v(4.9, 0.13) * mm});
            skLineSegment(sketch, "E2021", {"start": v(4.9, 0.13) * mm, "end": v(4.93, 0.14) * mm});
            skLineSegment(sketch, "E2022", {"start": v(4.93, 0.14) * mm, "end": v(4.94, 0.15) * mm});
            skLineSegment(sketch, "E2023", {"start": v(4.94, 0.15) * mm, "end": v(4.96, 0.16) * mm});
            skLineSegment(sketch, "E2024", {"start": v(4.96, 0.16) * mm, "end": v(4.98, 0.17) * mm});
            skLineSegment(sketch, "E2025", {"start": v(4.98, 0.17) * mm, "end": v(5, 0.18) * mm});
            skLineSegment(sketch, "E2026", {"start": v(5, 0.18) * mm, "end": v(5.01, 0.19) * mm});
            skLineSegment(sketch, "E2027", {"start": v(5.01, 0.19) * mm, "end": v(5.03, 0.2) * mm});
            skLineSegment(sketch, "E2028", {"start": v(5.03, 0.2) * mm, "end": v(5.05, 0.2) * mm});
            skLineSegment(sketch, "E2029", {"start": v(5.05, 0.2) * mm, "end": v(5.06, 0.22) * mm});
            skLineSegment(sketch, "E2030", {"start": v(5.06, 0.22) * mm, "end": v(5.08, 0.23) * mm});
            skLineSegment(sketch, "E2031", {"start": v(5.08, 0.23) * mm, "end": v(5.1, 0.24) * mm});
            skLineSegment(sketch, "E2032", {"start": v(5.1, 0.24) * mm, "end": v(5.12, 0.25) * mm});
            skLineSegment(sketch, "E2033", {"start": v(5.12, 0.25) * mm, "end": v(5.14, 0.27) * mm});
            skLineSegment(sketch, "E2034", {"start": v(5.14, 0.27) * mm, "end": v(5.16, 0.28) * mm});
            skLineSegment(sketch, "E2035", {"start": v(5.16, 0.28) * mm, "end": v(5.18, 0.3) * mm});
            skLineSegment(sketch, "E2036", {"start": v(5.18, 0.3) * mm, "end": v(5.2, 0.3) * mm});
            skLineSegment(sketch, "E2037", {"start": v(5.2, 0.3) * mm, "end": v(5.22, 0.32) * mm});
            skLineSegment(sketch, "E2038", {"start": v(5.22, 0.32) * mm, "end": v(5.24, 0.33) * mm});
            skLineSegment(sketch, "E2039", {"start": v(5.24, 0.33) * mm, "end": v(5.25, 0.35) * mm});
            skLineSegment(sketch, "E2040", {"start": v(5.25, 0.35) * mm, "end": v(5.24, 0.46) * mm});
            skLineSegment(sketch, "E2041", {"start": v(5.24, 0.46) * mm, "end": v(5.23, 0.47) * mm});
            skLineSegment(sketch, "E2042", {"start": v(5.23, 0.47) * mm, "end": v(5.2, 0.48) * mm});
            skLineSegment(sketch, "E2043", {"start": v(5.2, 0.48) * mm, "end": v(5.18, 0.5) * mm});
            skLineSegment(sketch, "E2044", {"start": v(5.18, 0.5) * mm, "end": v(5.16, 0.5) * mm});
            skLineSegment(sketch, "E2045", {"start": v(5.16, 0.5) * mm, "end": v(5.14, 0.51) * mm});
            skLineSegment(sketch, "E2046", {"start": v(5.14, 0.51) * mm, "end": v(5.12, 0.52) * mm});
            skLineSegment(sketch, "E2047", {"start": v(5.12, 0.52) * mm, "end": v(5.1, 0.53) * mm});
            skLineSegment(sketch, "E2048", {"start": v(5.1, 0.53) * mm, "end": v(5.08, 0.54) * mm});
            skLineSegment(sketch, "E2049", {"start": v(5.08, 0.54) * mm, "end": v(5.06, 0.55) * mm});
            skLineSegment(sketch, "E2050", {"start": v(5.06, 0.55) * mm, "end": v(5.04, 0.56) * mm});
            skLineSegment(sketch, "E2051", {"start": v(5.04, 0.56) * mm, "end": v(5.02, 0.57) * mm});
            skLineSegment(sketch, "E2052", {"start": v(5.02, 0.57) * mm, "end": v(5, 0.57) * mm});
            skLineSegment(sketch, "E2053", {"start": v(5, 0.57) * mm, "end": v(4.98, 0.58) * mm});
            skLineSegment(sketch, "E2054", {"start": v(4.98, 0.58) * mm, "end": v(4.96, 0.59) * mm});
            skLineSegment(sketch, "E2055", {"start": v(4.96, 0.59) * mm, "end": v(4.94, 0.6) * mm});
            skLineSegment(sketch, "E2056", {"start": v(4.94, 0.6) * mm, "end": v(4.93, 0.6) * mm});
            skLineSegment(sketch, "E2057", {"start": v(4.93, 0.6) * mm, "end": v(4.9, 0.6) * mm});
            skLineSegment(sketch, "E2058", {"start": v(4.9, 0.6) * mm, "end": v(4.9, 0.61) * mm});
            skLineSegment(sketch, "E2059", {"start": v(4.9, 0.61) * mm, "end": v(4.87, 0.62) * mm});
            skLineSegment(sketch, "E2060", {"start": v(4.87, 0.62) * mm, "end": v(4.86, 0.62) * mm});
            skLineSegment(sketch, "E2061", {"start": v(4.86, 0.62) * mm, "end": v(4.84, 0.63) * mm});
            skLineSegment(sketch, "E2062", {"start": v(4.84, 0.63) * mm, "end": v(4.82, 0.63) * mm});
            skLineSegment(sketch, "E2063", {"start": v(4.82, 0.63) * mm, "end": v(4.8, 0.64) * mm});
            skLineSegment(sketch, "E2064", {"start": v(4.8, 0.64) * mm, "end": v(4.8, 0.64) * mm});
            skLineSegment(sketch, "E2065", {"start": v(4.8, 0.64) * mm, "end": v(4.77, 0.65) * mm});
            skLineSegment(sketch, "E2066", {"start": v(4.77, 0.65) * mm, "end": v(4.76, 0.65) * mm});
            skLineSegment(sketch, "E2067", {"start": v(4.76, 0.65) * mm, "end": v(4.74, 0.65) * mm});
            skLineSegment(sketch, "E2068", {"start": v(4.74, 0.65) * mm, "end": v(4.73, 0.66) * mm});
            skLineSegment(sketch, "E2069", {"start": v(4.73, 0.66) * mm, "end": v(4.71, 0.66) * mm});
            skLineSegment(sketch, "E2070", {"start": v(4.71, 0.66) * mm, "end": v(4.7, 0.66) * mm});
            skLineSegment(sketch, "E2071", {"start": v(4.7, 0.66) * mm, "end": v(4.69, 0.67) * mm});
            skLineSegment(sketch, "E2072", {"start": v(4.69, 0.67) * mm, "end": v(4.68, 0.67) * mm});
            skLineSegment(sketch, "E2073", {"start": v(4.68, 0.67) * mm, "end": v(4.67, 0.72) * mm});
            skLineSegment(sketch, "E2074", {"start": v(4.67, 0.72) * mm, "end": v(4.66, 0.74) * mm});
            skLineSegment(sketch, "E2075", {"start": v(4.66, 0.74) * mm, "end": v(4.66, 0.8) * mm});
            skLineSegment(sketch, "E2076", {"start": v(4.66, 0.8) * mm, "end": v(4.67, 0.8) * mm});
            skLineSegment(sketch, "E2077", {"start": v(4.67, 0.8) * mm, "end": v(4.68, 0.8) * mm});
            skLineSegment(sketch, "E2078", {"start": v(4.68, 0.8) * mm, "end": v(4.7, 0.81) * mm});
            skLineSegment(sketch, "E2079", {"start": v(4.7, 0.81) * mm, "end": v(4.7, 0.82) * mm});
            skLineSegment(sketch, "E2080", {"start": v(4.7, 0.82) * mm, "end": v(4.72, 0.83) * mm});
            skLineSegment(sketch, "E2081", {"start": v(4.72, 0.83) * mm, "end": v(4.73, 0.84) * mm});
            skLineSegment(sketch, "E2082", {"start": v(4.73, 0.84) * mm, "end": v(4.74, 0.84) * mm});
            skLineSegment(sketch, "E2083", {"start": v(4.74, 0.84) * mm, "end": v(4.76, 0.85) * mm});
            skLineSegment(sketch, "E2084", {"start": v(4.76, 0.85) * mm, "end": v(4.77, 0.86) * mm});
            skLineSegment(sketch, "E2085", {"start": v(4.77, 0.86) * mm, "end": v(4.79, 0.87) * mm});
            skLineSegment(sketch, "E2086", {"start": v(4.79, 0.87) * mm, "end": v(4.8, 0.88) * mm});
            skLineSegment(sketch, "E2087", {"start": v(4.8, 0.88) * mm, "end": v(4.81, 0.9) * mm});
            skLineSegment(sketch, "E2088", {"start": v(4.81, 0.9) * mm, "end": v(4.83, 0.9) * mm});
            skLineSegment(sketch, "E2089", {"start": v(4.83, 0.9) * mm, "end": v(4.84, 0.91) * mm});
            skLineSegment(sketch, "E2090", {"start": v(4.84, 0.91) * mm, "end": v(4.86, 0.92) * mm});
            skLineSegment(sketch, "E2091", {"start": v(4.86, 0.92) * mm, "end": v(4.87, 0.93) * mm});
            skLineSegment(sketch, "E2092", {"start": v(4.87, 0.93) * mm, "end": v(4.89, 0.95) * mm});
            skLineSegment(sketch, "E2093", {"start": v(4.89, 0.95) * mm, "end": v(4.9, 0.96) * mm});
            skLineSegment(sketch, "E2094", {"start": v(4.9, 0.96) * mm, "end": v(4.92, 0.97) * mm});
            skLineSegment(sketch, "E2095", {"start": v(4.92, 0.97) * mm, "end": v(4.94, 0.98) * mm});
            skLineSegment(sketch, "E2096", {"start": v(4.94, 0.98) * mm, "end": v(4.95, 1) * mm});
            skLineSegment(sketch, "E2097", {"start": v(4.95, 1) * mm, "end": v(4.97, 1) * mm});
            skLineSegment(sketch, "E2098", {"start": v(4.97, 1) * mm, "end": v(4.98, 1.02) * mm});
            skLineSegment(sketch, "E2099", {"start": v(4.98, 1.02) * mm, "end": v(5, 1.04) * mm});
            skLineSegment(sketch, "E2100", {"start": v(5, 1.04) * mm, "end": v(5.02, 1.05) * mm});
            skLineSegment(sketch, "E2101", {"start": v(5.02, 1.05) * mm, "end": v(5.03, 1.07) * mm});
            skLineSegment(sketch, "E2102", {"start": v(5.03, 1.07) * mm, "end": v(5.05, 1.08) * mm});
            skLineSegment(sketch, "E2103", {"start": v(5.05, 1.08) * mm, "end": v(5.07, 1.1) * mm});
            skLineSegment(sketch, "E2104", {"start": v(5.07, 1.1) * mm, "end": v(5.08, 1.11) * mm});
            skLineSegment(sketch, "E2105", {"start": v(5.08, 1.11) * mm, "end": v(5.1, 1.13) * mm});
            skLineSegment(sketch, "E2106", {"start": v(5.1, 1.13) * mm, "end": v(5.12, 1.15) * mm});
            skLineSegment(sketch, "E2107", {"start": v(5.12, 1.15) * mm, "end": v(5.13, 1.17) * mm});
            skLineSegment(sketch, "E2108", {"start": v(5.13, 1.17) * mm, "end": v(5.1, 1.27) * mm});
            skLineSegment(sketch, "E2109", {"start": v(5.1, 1.27) * mm, "end": v(5.09, 1.28) * mm});
            skLineSegment(sketch, "E2110", {"start": v(5.09, 1.28) * mm, "end": v(5.06, 1.3) * mm});
            skLineSegment(sketch, "E2111", {"start": v(5.06, 1.3) * mm, "end": v(5.04, 1.3) * mm});
            skLineSegment(sketch, "E2112", {"start": v(5.04, 1.3) * mm, "end": v(5.02, 1.3) * mm});
            skLineSegment(sketch, "E2113", {"start": v(5.02, 1.3) * mm, "end": v(5, 1.31) * mm});
            skLineSegment(sketch, "E2114", {"start": v(5, 1.31) * mm, "end": v(4.97, 1.32) * mm});
            skLineSegment(sketch, "E2115", {"start": v(4.97, 1.32) * mm, "end": v(4.95, 1.32) * mm});
            skLineSegment(sketch, "E2116", {"start": v(4.95, 1.32) * mm, "end": v(4.93, 1.33) * mm});
            skLineSegment(sketch, "E2117", {"start": v(4.93, 1.33) * mm, "end": v(4.9, 1.33) * mm});
            skLineSegment(sketch, "E2118", {"start": v(4.9, 1.33) * mm, "end": v(4.89, 1.34) * mm});
            skLineSegment(sketch, "E2119", {"start": v(4.89, 1.34) * mm, "end": v(4.87, 1.34) * mm});
            skLineSegment(sketch, "E2120", {"start": v(4.87, 1.34) * mm, "end": v(4.85, 1.35) * mm});
            skLineSegment(sketch, "E2121", {"start": v(4.85, 1.35) * mm, "end": v(4.83, 1.35) * mm});
            skLineSegment(sketch, "E2122", {"start": v(4.83, 1.35) * mm, "end": v(4.8, 1.36) * mm});
            skLineSegment(sketch, "E2123", {"start": v(4.8, 1.36) * mm, "end": v(4.79, 1.36) * mm});
            skLineSegment(sketch, "E2124", {"start": v(4.79, 1.36) * mm, "end": v(4.77, 1.36) * mm});
            skLineSegment(sketch, "E2125", {"start": v(4.77, 1.36) * mm, "end": v(4.75, 1.37) * mm});
            skLineSegment(sketch, "E2126", {"start": v(4.75, 1.37) * mm, "end": v(4.73, 1.37) * mm});
            skLineSegment(sketch, "E2127", {"start": v(4.73, 1.37) * mm, "end": v(4.72, 1.37) * mm});
            skLineSegment(sketch, "E2128", {"start": v(4.72, 1.37) * mm, "end": v(4.7, 1.38) * mm});
            skLineSegment(sketch, "E2129", {"start": v(4.7, 1.38) * mm, "end": v(4.68, 1.38) * mm});
            skLineSegment(sketch, "E2130", {"start": v(4.68, 1.38) * mm, "end": v(4.66, 1.38) * mm});
            skLineSegment(sketch, "E2131", {"start": v(4.66, 1.38) * mm, "end": v(4.65, 1.38) * mm});
            skLineSegment(sketch, "E2132", {"start": v(4.65, 1.38) * mm, "end": v(4.63, 1.38) * mm});
            skLineSegment(sketch, "E2133", {"start": v(4.63, 1.38) * mm, "end": v(4.61, 1.39) * mm});
            skLineSegment(sketch, "E2134", {"start": v(4.61, 1.39) * mm, "end": v(4.6, 1.39) * mm});
            skLineSegment(sketch, "E2135", {"start": v(4.6, 1.39) * mm, "end": v(4.58, 1.39) * mm});
            skLineSegment(sketch, "E2136", {"start": v(4.58, 1.39) * mm, "end": v(4.57, 1.4) * mm});
            skLineSegment(sketch, "E2137", {"start": v(4.57, 1.4) * mm, "end": v(4.55, 1.4) * mm});
            skLineSegment(sketch, "E2138", {"start": v(4.55, 1.4) * mm, "end": v(4.54, 1.4) * mm});
            skLineSegment(sketch, "E2139", {"start": v(4.54, 1.4) * mm, "end": v(4.52, 1.4) * mm});
            skLineSegment(sketch, "E2140", {"start": v(4.52, 1.4) * mm, "end": v(4.52, 1.4) * mm});
            skLineSegment(sketch, "E2141", {"start": v(4.52, 1.4) * mm, "end": v(4.5, 1.44) * mm});
            skLineSegment(sketch, "E2142", {"start": v(4.5, 1.44) * mm, "end": v(4.5, 1.46) * mm});
            skLineSegment(sketch, "E2143", {"start": v(4.5, 1.46) * mm, "end": v(4.48, 1.51) * mm});
            skLineSegment(sketch, "E2144", {"start": v(4.48, 1.51) * mm, "end": v(4.48, 1.52) * mm});
            skLineSegment(sketch, "E2145", {"start": v(4.48, 1.52) * mm, "end": v(4.5, 1.53) * mm});
            skLineSegment(sketch, "E2146", {"start": v(4.5, 1.53) * mm, "end": v(4.5, 1.54) * mm});
            skLineSegment(sketch, "E2147", {"start": v(4.5, 1.54) * mm, "end": v(4.52, 1.55) * mm});
            skLineSegment(sketch, "E2148", {"start": v(4.52, 1.55) * mm, "end": v(4.53, 1.56) * mm});
            skLineSegment(sketch, "E2149", {"start": v(4.53, 1.56) * mm, "end": v(4.54, 1.57) * mm});
            skLineSegment(sketch, "E2150", {"start": v(4.54, 1.57) * mm, "end": v(4.55, 1.58) * mm});
            skLineSegment(sketch, "E2151", {"start": v(4.55, 1.58) * mm, "end": v(4.57, 1.59) * mm});
            skLineSegment(sketch, "E2152", {"start": v(4.57, 1.59) * mm, "end": v(4.58, 1.6) * mm});
            skLineSegment(sketch, "E2153", {"start": v(4.58, 1.6) * mm, "end": v(4.59, 1.6) * mm});
            skLineSegment(sketch, "E2154", {"start": v(4.59, 1.6) * mm, "end": v(4.6, 1.62) * mm});
            skLineSegment(sketch, "E2155", {"start": v(4.6, 1.62) * mm, "end": v(4.62, 1.63) * mm});
            skLineSegment(sketch, "E2156", {"start": v(4.62, 1.63) * mm, "end": v(4.63, 1.65) * mm});
            skLineSegment(sketch, "E2157", {"start": v(4.63, 1.65) * mm, "end": v(4.64, 1.66) * mm});
            skLineSegment(sketch, "E2158", {"start": v(4.64, 1.66) * mm, "end": v(4.65, 1.67) * mm});
            skLineSegment(sketch, "E2159", {"start": v(4.65, 1.67) * mm, "end": v(4.67, 1.69) * mm});
            skLineSegment(sketch, "E2160", {"start": v(4.67, 1.69) * mm, "end": v(4.68, 1.7) * mm});
            skLineSegment(sketch, "E2161", {"start": v(4.68, 1.7) * mm, "end": v(4.7, 1.71) * mm});
            skLineSegment(sketch, "E2162", {"start": v(4.7, 1.71) * mm, "end": v(4.7, 1.73) * mm});
            skLineSegment(sketch, "E2163", {"start": v(4.7, 1.73) * mm, "end": v(4.72, 1.74) * mm});
            skLineSegment(sketch, "E2164", {"start": v(4.72, 1.74) * mm, "end": v(4.73, 1.76) * mm});
            skLineSegment(sketch, "E2165", {"start": v(4.73, 1.76) * mm, "end": v(4.75, 1.77) * mm});
            skLineSegment(sketch, "E2166", {"start": v(4.75, 1.77) * mm, "end": v(4.76, 1.8) * mm});
            skLineSegment(sketch, "E2167", {"start": v(4.76, 1.8) * mm, "end": v(4.78, 1.8) * mm});
            skLineSegment(sketch, "E2168", {"start": v(4.78, 1.8) * mm, "end": v(4.8, 1.82) * mm});
            skLineSegment(sketch, "E2169", {"start": v(4.8, 1.82) * mm, "end": v(4.8, 1.84) * mm});
            skLineSegment(sketch, "E2170", {"start": v(4.8, 1.84) * mm, "end": v(4.82, 1.86) * mm});
            skLineSegment(sketch, "E2171", {"start": v(4.82, 1.86) * mm, "end": v(4.83, 1.88) * mm});
            skLineSegment(sketch, "E2172", {"start": v(4.83, 1.88) * mm, "end": v(4.85, 1.9) * mm});
            skLineSegment(sketch, "E2173", {"start": v(4.85, 1.9) * mm, "end": v(4.86, 1.91) * mm});
            skLineSegment(sketch, "E2174", {"start": v(4.86, 1.91) * mm, "end": v(4.88, 1.93) * mm});
            skLineSegment(sketch, "E2175", {"start": v(4.88, 1.93) * mm, "end": v(4.88, 1.96) * mm});
            skLineSegment(sketch, "E2176", {"start": v(4.88, 1.96) * mm, "end": v(4.84, 2.05) * mm});
            skLineSegment(sketch, "E2177", {"start": v(4.84, 2.05) * mm, "end": v(4.82, 2.06) * mm});
            skLineSegment(sketch, "E2178", {"start": v(4.82, 2.06) * mm, "end": v(4.8, 2.07) * mm});
            skLineSegment(sketch, "E2179", {"start": v(4.8, 2.07) * mm, "end": v(4.77, 2.07) * mm});
            skLineSegment(sketch, "E2180", {"start": v(4.77, 2.07) * mm, "end": v(4.75, 2.08) * mm});
            skLineSegment(sketch, "E2181", {"start": v(4.75, 2.08) * mm, "end": v(4.73, 2.08) * mm});
            skLineSegment(sketch, "E2182", {"start": v(4.73, 2.08) * mm, "end": v(4.7, 2.08) * mm});
            skLineSegment(sketch, "E2183", {"start": v(4.7, 2.08) * mm, "end": v(4.68, 2.08) * mm});
            skLineSegment(sketch, "E2184", {"start": v(4.68, 2.08) * mm, "end": v(4.66, 2.08) * mm});
            skLineSegment(sketch, "E2185", {"start": v(4.66, 2.08) * mm, "end": v(4.64, 2.09) * mm});
            skLineSegment(sketch, "E2186", {"start": v(4.64, 2.09) * mm, "end": v(4.62, 2.09) * mm});
            skLineSegment(sketch, "E2187", {"start": v(4.62, 2.09) * mm, "end": v(4.6, 2.09) * mm});
            skLineSegment(sketch, "E2188", {"start": v(4.6, 2.09) * mm, "end": v(4.58, 2.1) * mm});
            skLineSegment(sketch, "E2189", {"start": v(4.58, 2.1) * mm, "end": v(4.56, 2.1) * mm});
            skLineSegment(sketch, "E2190", {"start": v(4.56, 2.1) * mm, "end": v(4.54, 2.1) * mm});
            skLineSegment(sketch, "E2191", {"start": v(4.54, 2.1) * mm, "end": v(4.52, 2.1) * mm});
            skLineSegment(sketch, "E2192", {"start": v(4.52, 2.1) * mm, "end": v(4.5, 2.1) * mm});
            skLineSegment(sketch, "E2193", {"start": v(4.5, 2.1) * mm, "end": v(4.48, 2.1) * mm});
            skLineSegment(sketch, "E2194", {"start": v(4.48, 2.1) * mm, "end": v(4.46, 2.1) * mm});
            skLineSegment(sketch, "E2195", {"start": v(4.46, 2.1) * mm, "end": v(4.44, 2.1) * mm});
            skLineSegment(sketch, "E2196", {"start": v(4.44, 2.1) * mm, "end": v(4.43, 2.1) * mm});
            skLineSegment(sketch, "E2197", {"start": v(4.43, 2.1) * mm, "end": v(4.4, 2.1) * mm});
            skLineSegment(sketch, "E2198", {"start": v(4.4, 2.1) * mm, "end": v(4.4, 2.1) * mm});
            skLineSegment(sketch, "E2199", {"start": v(4.4, 2.1) * mm, "end": v(4.37, 2.1) * mm});
            skLineSegment(sketch, "E2200", {"start": v(4.37, 2.1) * mm, "end": v(4.36, 2.1) * mm});
            skLineSegment(sketch, "E2201", {"start": v(4.36, 2.1) * mm, "end": v(4.34, 2.1) * mm});
            skLineSegment(sketch, "E2202", {"start": v(4.34, 2.1) * mm, "end": v(4.32, 2.1) * mm});
            skLineSegment(sketch, "E2203", {"start": v(4.32, 2.1) * mm, "end": v(4.3, 2.09) * mm});
            skLineSegment(sketch, "E2204", {"start": v(4.3, 2.09) * mm, "end": v(4.3, 2.09) * mm});
            skLineSegment(sketch, "E2205", {"start": v(4.3, 2.09) * mm, "end": v(4.28, 2.09) * mm});
            skLineSegment(sketch, "E2206", {"start": v(4.28, 2.09) * mm, "end": v(4.27, 2.09) * mm});
            skLineSegment(sketch, "E2207", {"start": v(4.27, 2.09) * mm, "end": v(4.25, 2.08) * mm});
            skLineSegment(sketch, "E2208", {"start": v(4.25, 2.08) * mm, "end": v(4.24, 2.08) * mm});
            skLineSegment(sketch, "E2209", {"start": v(4.24, 2.08) * mm, "end": v(4.21, 2.13) * mm});
            skLineSegment(sketch, "E2210", {"start": v(4.21, 2.13) * mm, "end": v(4.2, 2.14) * mm});
            skLineSegment(sketch, "E2211", {"start": v(4.2, 2.14) * mm, "end": v(4.19, 2.2) * mm});
            skLineSegment(sketch, "E2212", {"start": v(4.19, 2.2) * mm, "end": v(4.2, 2.2) * mm});
            skLineSegment(sketch, "E2213", {"start": v(4.2, 2.2) * mm, "end": v(4.2, 2.21) * mm});
            skLineSegment(sketch, "E2214", {"start": v(4.2, 2.21) * mm, "end": v(4.21, 2.22) * mm});
            skLineSegment(sketch, "E2215", {"start": v(4.21, 2.22) * mm, "end": v(4.22, 2.23) * mm});
            skLineSegment(sketch, "E2216", {"start": v(4.22, 2.23) * mm, "end": v(4.23, 2.24) * mm});
            skLineSegment(sketch, "E2217", {"start": v(4.23, 2.24) * mm, "end": v(4.24, 2.26) * mm});
            skLineSegment(sketch, "E2218", {"start": v(4.24, 2.26) * mm, "end": v(4.25, 2.27) * mm});
            skLineSegment(sketch, "E2219", {"start": v(4.25, 2.27) * mm, "end": v(4.26, 2.28) * mm});
            skLineSegment(sketch, "E2220", {"start": v(4.26, 2.28) * mm, "end": v(4.27, 2.3) * mm});
            skLineSegment(sketch, "E2221", {"start": v(4.27, 2.3) * mm, "end": v(4.28, 2.3) * mm});
            skLineSegment(sketch, "E2222", {"start": v(4.28, 2.3) * mm, "end": v(4.3, 2.32) * mm});
            skLineSegment(sketch, "E2223", {"start": v(4.3, 2.32) * mm, "end": v(4.3, 2.34) * mm});
            skLineSegment(sketch, "E2224", {"start": v(4.3, 2.34) * mm, "end": v(4.31, 2.35) * mm});
            skLineSegment(sketch, "E2225", {"start": v(4.31, 2.35) * mm, "end": v(4.32, 2.36) * mm});
            skLineSegment(sketch, "E2226", {"start": v(4.32, 2.36) * mm, "end": v(4.34, 2.38) * mm});
            skLineSegment(sketch, "E2227", {"start": v(4.34, 2.38) * mm, "end": v(4.35, 2.4) * mm});
            skLineSegment(sketch, "E2228", {"start": v(4.35, 2.4) * mm, "end": v(4.36, 2.41) * mm});
            skLineSegment(sketch, "E2229", {"start": v(4.36, 2.41) * mm, "end": v(4.37, 2.43) * mm});
            skLineSegment(sketch, "E2230", {"start": v(4.37, 2.43) * mm, "end": v(4.38, 2.44) * mm});
            skLineSegment(sketch, "E2231", {"start": v(4.38, 2.44) * mm, "end": v(4.4, 2.46) * mm});
            skLineSegment(sketch, "E2232", {"start": v(4.4, 2.46) * mm, "end": v(4.4, 2.48) * mm});
            skLineSegment(sketch, "E2233", {"start": v(4.4, 2.48) * mm, "end": v(4.41, 2.5) * mm});
            skLineSegment(sketch, "E2234", {"start": v(4.41, 2.5) * mm, "end": v(4.42, 2.51) * mm});
            skLineSegment(sketch, "E2235", {"start": v(4.42, 2.51) * mm, "end": v(4.44, 2.53) * mm});
            skLineSegment(sketch, "E2236", {"start": v(4.44, 2.53) * mm, "end": v(4.45, 2.55) * mm});
            skLineSegment(sketch, "E2237", {"start": v(4.45, 2.55) * mm, "end": v(4.46, 2.57) * mm});
            skLineSegment(sketch, "E2238", {"start": v(4.46, 2.57) * mm, "end": v(4.47, 2.59) * mm});
            skLineSegment(sketch, "E2239", {"start": v(4.47, 2.59) * mm, "end": v(4.48, 2.6) * mm});
            skLineSegment(sketch, "E2240", {"start": v(4.48, 2.6) * mm, "end": v(4.5, 2.63) * mm});
            skLineSegment(sketch, "E2241", {"start": v(4.5, 2.63) * mm, "end": v(4.5, 2.65) * mm});
            skLineSegment(sketch, "E2242", {"start": v(4.5, 2.65) * mm, "end": v(4.51, 2.67) * mm});
            skLineSegment(sketch, "E2243", {"start": v(4.51, 2.67) * mm, "end": v(4.52, 2.7) * mm});
            skLineSegment(sketch, "E2244", {"start": v(4.52, 2.7) * mm, "end": v(4.46, 2.79) * mm});
            skLineSegment(sketch, "E2245", {"start": v(4.46, 2.79) * mm, "end": v(4.44, 2.8) * mm});
            skLineSegment(sketch, "E2246", {"start": v(4.44, 2.8) * mm, "end": v(4.42, 2.8) * mm});
            skLineSegment(sketch, "E2247", {"start": v(4.42, 2.8) * mm, "end": v(4.4, 2.8) * mm});
            skLineSegment(sketch, "E2248", {"start": v(4.4, 2.8) * mm, "end": v(4.37, 2.8) * mm});
            skLineSegment(sketch, "E2249", {"start": v(4.37, 2.8) * mm, "end": v(4.35, 2.8) * mm});
            skLineSegment(sketch, "E2250", {"start": v(4.35, 2.8) * mm, "end": v(4.32, 2.8) * mm});
            skLineSegment(sketch, "E2251", {"start": v(4.32, 2.8) * mm, "end": v(4.3, 2.79) * mm});
            skLineSegment(sketch, "E2252", {"start": v(4.3, 2.79) * mm, "end": v(4.28, 2.79) * mm});
            skLineSegment(sketch, "E2253", {"start": v(4.28, 2.79) * mm, "end": v(4.26, 2.79) * mm});
            skLineSegment(sketch, "E2254", {"start": v(4.26, 2.79) * mm, "end": v(4.24, 2.79) * mm});
            skLineSegment(sketch, "E2255", {"start": v(4.24, 2.79) * mm, "end": v(4.21, 2.78) * mm});
            skLineSegment(sketch, "E2256", {"start": v(4.21, 2.78) * mm, "end": v(4.2, 2.78) * mm});
            skLineSegment(sketch, "E2257", {"start": v(4.2, 2.78) * mm, "end": v(4.17, 2.78) * mm});
            skLineSegment(sketch, "E2258", {"start": v(4.17, 2.78) * mm, "end": v(4.15, 2.78) * mm});
            skLineSegment(sketch, "E2259", {"start": v(4.15, 2.78) * mm, "end": v(4.13, 2.77) * mm});
            skLineSegment(sketch, "E2260", {"start": v(4.13, 2.77) * mm, "end": v(4.12, 2.77) * mm});
            skLineSegment(sketch, "E2261", {"start": v(4.12, 2.77) * mm, "end": v(4.1, 2.77) * mm});
            skLineSegment(sketch, "E2262", {"start": v(4.1, 2.77) * mm, "end": v(4.08, 2.77) * mm});
            skLineSegment(sketch, "E2263", {"start": v(4.08, 2.77) * mm, "end": v(4.06, 2.76) * mm});
            skLineSegment(sketch, "E2264", {"start": v(4.06, 2.76) * mm, "end": v(4.04, 2.76) * mm});
            skLineSegment(sketch, "E2265", {"start": v(4.04, 2.76) * mm, "end": v(4.03, 2.76) * mm});
            skLineSegment(sketch, "E2266", {"start": v(4.03, 2.76) * mm, "end": v(4, 2.75) * mm});
            skLineSegment(sketch, "E2267", {"start": v(4, 2.75) * mm, "end": v(4, 2.75) * mm});
            skLineSegment(sketch, "E2268", {"start": v(4, 2.75) * mm, "end": v(3.98, 2.75) * mm});
            skLineSegment(sketch, "E2269", {"start": v(3.98, 2.75) * mm, "end": v(3.96, 2.74) * mm});
            skLineSegment(sketch, "E2270", {"start": v(3.96, 2.74) * mm, "end": v(3.94, 2.74) * mm});
            skLineSegment(sketch, "E2271", {"start": v(3.94, 2.74) * mm, "end": v(3.93, 2.74) * mm});
            skLineSegment(sketch, "E2272", {"start": v(3.93, 2.74) * mm, "end": v(3.91, 2.73) * mm});
            skLineSegment(sketch, "E2273", {"start": v(3.91, 2.73) * mm, "end": v(3.9, 2.73) * mm});
            skLineSegment(sketch, "E2274", {"start": v(3.9, 2.73) * mm, "end": v(3.89, 2.73) * mm});
            skLineSegment(sketch, "E2275", {"start": v(3.89, 2.73) * mm, "end": v(3.87, 2.72) * mm});
            skLineSegment(sketch, "E2276", {"start": v(3.87, 2.72) * mm, "end": v(3.87, 2.72) * mm});
            skLineSegment(sketch, "E2277", {"start": v(3.87, 2.72) * mm, "end": v(3.83, 2.76) * mm});
            skLineSegment(sketch, "E2278", {"start": v(3.83, 2.76) * mm, "end": v(3.82, 2.78) * mm});
            skLineSegment(sketch, "E2279", {"start": v(3.82, 2.78) * mm, "end": v(3.8, 2.82) * mm});
            skLineSegment(sketch, "E2280", {"start": v(3.8, 2.82) * mm, "end": v(3.8, 2.83) * mm});
            skLineSegment(sketch, "E2281", {"start": v(3.8, 2.83) * mm, "end": v(3.8, 2.84) * mm});
            skLineSegment(sketch, "E2282", {"start": v(3.8, 2.84) * mm, "end": v(3.81, 2.85) * mm});
            skLineSegment(sketch, "E2283", {"start": v(3.81, 2.85) * mm, "end": v(3.82, 2.87) * mm});
            skLineSegment(sketch, "E2284", {"start": v(3.82, 2.87) * mm, "end": v(3.83, 2.88) * mm});
            skLineSegment(sketch, "E2285", {"start": v(3.83, 2.88) * mm, "end": v(3.84, 2.9) * mm});
            skLineSegment(sketch, "E2286", {"start": v(3.84, 2.9) * mm, "end": v(3.84, 2.9) * mm});
            skLineSegment(sketch, "E2287", {"start": v(3.84, 2.9) * mm, "end": v(3.85, 2.92) * mm});
            skLineSegment(sketch, "E2288", {"start": v(3.85, 2.92) * mm, "end": v(3.86, 2.93) * mm});
            skLineSegment(sketch, "E2289", {"start": v(3.86, 2.93) * mm, "end": v(3.87, 2.95) * mm});
            skLineSegment(sketch, "E2290", {"start": v(3.87, 2.95) * mm, "end": v(3.88, 2.96) * mm});
            skLineSegment(sketch, "E2291", {"start": v(3.88, 2.96) * mm, "end": v(3.88, 2.98) * mm});
            skLineSegment(sketch, "E2292", {"start": v(3.88, 2.98) * mm, "end": v(3.9, 3) * mm});
            skLineSegment(sketch, "E2293", {"start": v(3.9, 3) * mm, "end": v(3.9, 3.01) * mm});
            skLineSegment(sketch, "E2294", {"start": v(3.9, 3.01) * mm, "end": v(3.9, 3.03) * mm});
            skLineSegment(sketch, "E2295", {"start": v(3.9, 3.03) * mm, "end": v(3.92, 3.05) * mm});
            skLineSegment(sketch, "E2296", {"start": v(3.92, 3.05) * mm, "end": v(3.93, 3.06) * mm});
            skLineSegment(sketch, "E2297", {"start": v(3.93, 3.06) * mm, "end": v(3.93, 3.08) * mm});
            skLineSegment(sketch, "E2298", {"start": v(3.93, 3.08) * mm, "end": v(3.94, 3.1) * mm});
            skLineSegment(sketch, "E2299", {"start": v(3.94, 3.1) * mm, "end": v(3.95, 3.12) * mm});
            skLineSegment(sketch, "E2300", {"start": v(3.95, 3.12) * mm, "end": v(3.96, 3.14) * mm});
            skLineSegment(sketch, "E2301", {"start": v(3.96, 3.14) * mm, "end": v(3.97, 3.16) * mm});
            skLineSegment(sketch, "E2302", {"start": v(3.97, 3.16) * mm, "end": v(3.98, 3.17) * mm});
            skLineSegment(sketch, "E2303", {"start": v(3.98, 3.17) * mm, "end": v(3.98, 3.2) * mm});
            skLineSegment(sketch, "E2304", {"start": v(3.98, 3.2) * mm, "end": v(4, 3.22) * mm});
            skLineSegment(sketch, "E2305", {"start": v(4, 3.22) * mm, "end": v(4, 3.24) * mm});
            skLineSegment(sketch, "E2306", {"start": v(4, 3.24) * mm, "end": v(4, 3.26) * mm});
            skLineSegment(sketch, "E2307", {"start": v(4, 3.26) * mm, "end": v(4.02, 3.28) * mm});
            skLineSegment(sketch, "E2308", {"start": v(4.02, 3.28) * mm, "end": v(4.02, 3.3) * mm});
            skLineSegment(sketch, "E2309", {"start": v(4.02, 3.3) * mm, "end": v(4.03, 3.32) * mm});
            skLineSegment(sketch, "E2310", {"start": v(4.03, 3.32) * mm, "end": v(4.04, 3.35) * mm});
            skLineSegment(sketch, "E2311", {"start": v(4.04, 3.35) * mm, "end": v(4.04, 3.37) * mm});
            skLineSegment(sketch, "E2312", {"start": v(4.04, 3.37) * mm, "end": v(3.97, 3.45) * mm});
            skLineSegment(sketch, "E2313", {"start": v(3.97, 3.45) * mm, "end": v(3.95, 3.45) * mm});
            skLineSegment(sketch, "E2314", {"start": v(3.95, 3.45) * mm, "end": v(3.92, 3.45) * mm});
            skLineSegment(sketch, "E2315", {"start": v(3.92, 3.45) * mm, "end": v(3.9, 3.45) * mm});
            skLineSegment(sketch, "E2316", {"start": v(3.9, 3.45) * mm, "end": v(3.88, 3.44) * mm});
            skLineSegment(sketch, "E2317", {"start": v(3.88, 3.44) * mm, "end": v(3.85, 3.44) * mm});
            skLineSegment(sketch, "E2318", {"start": v(3.85, 3.44) * mm, "end": v(3.83, 3.43) * mm});
            skLineSegment(sketch, "E2319", {"start": v(3.83, 3.43) * mm, "end": v(3.81, 3.43) * mm});
            skLineSegment(sketch, "E2320", {"start": v(3.81, 3.43) * mm, "end": v(3.79, 3.42) * mm});
            skLineSegment(sketch, "E2321", {"start": v(3.79, 3.42) * mm, "end": v(3.77, 3.42) * mm});
            skLineSegment(sketch, "E2322", {"start": v(3.77, 3.42) * mm, "end": v(3.75, 3.41) * mm});
            skLineSegment(sketch, "E2323", {"start": v(3.75, 3.41) * mm, "end": v(3.73, 3.4) * mm});
            skLineSegment(sketch, "E2324", {"start": v(3.73, 3.4) * mm, "end": v(3.7, 3.4) * mm});
            skLineSegment(sketch, "E2325", {"start": v(3.7, 3.4) * mm, "end": v(3.69, 3.4) * mm});
            skLineSegment(sketch, "E2326", {"start": v(3.69, 3.4) * mm, "end": v(3.67, 3.4) * mm});
            skLineSegment(sketch, "E2327", {"start": v(3.67, 3.4) * mm, "end": v(3.65, 3.39) * mm});
            skLineSegment(sketch, "E2328", {"start": v(3.65, 3.39) * mm, "end": v(3.63, 3.38) * mm});
            skLineSegment(sketch, "E2329", {"start": v(3.63, 3.38) * mm, "end": v(3.61, 3.38) * mm});
            skLineSegment(sketch, "E2330", {"start": v(3.61, 3.38) * mm, "end": v(3.6, 3.37) * mm});
            skLineSegment(sketch, "E2331", {"start": v(3.6, 3.37) * mm, "end": v(3.58, 3.37) * mm});
            skLineSegment(sketch, "E2332", {"start": v(3.58, 3.37) * mm, "end": v(3.56, 3.36) * mm});
            skLineSegment(sketch, "E2333", {"start": v(3.56, 3.36) * mm, "end": v(3.54, 3.35) * mm});
            skLineSegment(sketch, "E2334", {"start": v(3.54, 3.35) * mm, "end": v(3.53, 3.35) * mm});
            skLineSegment(sketch, "E2335", {"start": v(3.53, 3.35) * mm, "end": v(3.51, 3.34) * mm});
            skLineSegment(sketch, "E2336", {"start": v(3.51, 3.34) * mm, "end": v(3.5, 3.34) * mm});
            skLineSegment(sketch, "E2337", {"start": v(3.5, 3.34) * mm, "end": v(3.48, 3.33) * mm});
            skLineSegment(sketch, "E2338", {"start": v(3.48, 3.33) * mm, "end": v(3.47, 3.32) * mm});
            skLineSegment(sketch, "E2339", {"start": v(3.47, 3.32) * mm, "end": v(3.45, 3.32) * mm});
            skLineSegment(sketch, "E2340", {"start": v(3.45, 3.32) * mm, "end": v(3.44, 3.31) * mm});
            skLineSegment(sketch, "E2341", {"start": v(3.44, 3.31) * mm, "end": v(3.43, 3.3) * mm});
            skLineSegment(sketch, "E2342", {"start": v(3.43, 3.3) * mm, "end": v(3.41, 3.3) * mm});
            skLineSegment(sketch, "E2343", {"start": v(3.41, 3.3) * mm, "end": v(3.4, 3.3) * mm});
            skLineSegment(sketch, "E2344", {"start": v(3.4, 3.3) * mm, "end": v(3.4, 3.3) * mm});
            skLineSegment(sketch, "E2345", {"start": v(3.4, 3.3) * mm, "end": v(3.35, 3.33) * mm});
            skLineSegment(sketch, "E2346", {"start": v(3.35, 3.33) * mm, "end": v(3.34, 3.34) * mm});
            skLineSegment(sketch, "E2347", {"start": v(3.34, 3.34) * mm, "end": v(3.3, 3.38) * mm});
            skLineSegment(sketch, "E2348", {"start": v(3.3, 3.38) * mm, "end": v(3.3, 3.39) * mm});
            skLineSegment(sketch, "E2349", {"start": v(3.3, 3.39) * mm, "end": v(3.31, 3.4) * mm});
            skLineSegment(sketch, "E2350", {"start": v(3.31, 3.4) * mm, "end": v(3.32, 3.41) * mm});
            skLineSegment(sketch, "E2351", {"start": v(3.32, 3.41) * mm, "end": v(3.32, 3.43) * mm});
            skLineSegment(sketch, "E2352", {"start": v(3.32, 3.43) * mm, "end": v(3.33, 3.44) * mm});
            skLineSegment(sketch, "E2353", {"start": v(3.33, 3.44) * mm, "end": v(3.34, 3.46) * mm});
            skLineSegment(sketch, "E2354", {"start": v(3.34, 3.46) * mm, "end": v(3.34, 3.47) * mm});
            skLineSegment(sketch, "E2355", {"start": v(3.34, 3.47) * mm, "end": v(3.35, 3.49) * mm});
            skLineSegment(sketch, "E2356", {"start": v(3.35, 3.49) * mm, "end": v(3.35, 3.5) * mm});
            skLineSegment(sketch, "E2357", {"start": v(3.35, 3.5) * mm, "end": v(3.36, 3.52) * mm});
            skLineSegment(sketch, "E2358", {"start": v(3.36, 3.52) * mm, "end": v(3.36, 3.53) * mm});
            skLineSegment(sketch, "E2359", {"start": v(3.36, 3.53) * mm, "end": v(3.37, 3.55) * mm});
            skLineSegment(sketch, "E2360", {"start": v(3.37, 3.55) * mm, "end": v(3.38, 3.57) * mm});
            skLineSegment(sketch, "E2361", {"start": v(3.38, 3.57) * mm, "end": v(3.38, 3.59) * mm});
            skLineSegment(sketch, "E2362", {"start": v(3.38, 3.59) * mm, "end": v(3.39, 3.6) * mm});
            skLineSegment(sketch, "E2363", {"start": v(3.39, 3.6) * mm, "end": v(3.4, 3.62) * mm});
            skLineSegment(sketch, "E2364", {"start": v(3.4, 3.62) * mm, "end": v(3.4, 3.64) * mm});
            skLineSegment(sketch, "E2365", {"start": v(3.4, 3.64) * mm, "end": v(3.4, 3.66) * mm});
            skLineSegment(sketch, "E2366", {"start": v(3.4, 3.66) * mm, "end": v(3.4, 3.68) * mm});
            skLineSegment(sketch, "E2367", {"start": v(3.4, 3.68) * mm, "end": v(3.42, 3.7) * mm});
            skLineSegment(sketch, "E2368", {"start": v(3.42, 3.7) * mm, "end": v(3.42, 3.72) * mm});
            skLineSegment(sketch, "E2369", {"start": v(3.42, 3.72) * mm, "end": v(3.43, 3.74) * mm});
            skLineSegment(sketch, "E2370", {"start": v(3.43, 3.74) * mm, "end": v(3.43, 3.76) * mm});
            skLineSegment(sketch, "E2371", {"start": v(3.43, 3.76) * mm, "end": v(3.44, 3.78) * mm});
            skLineSegment(sketch, "E2372", {"start": v(3.44, 3.78) * mm, "end": v(3.44, 3.8) * mm});
            skLineSegment(sketch, "E2373", {"start": v(3.44, 3.8) * mm, "end": v(3.45, 3.82) * mm});
            skLineSegment(sketch, "E2374", {"start": v(3.45, 3.82) * mm, "end": v(3.45, 3.84) * mm});
            skLineSegment(sketch, "E2375", {"start": v(3.45, 3.84) * mm, "end": v(3.45, 3.87) * mm});
            skLineSegment(sketch, "E2376", {"start": v(3.45, 3.87) * mm, "end": v(3.46, 3.89) * mm});
            skLineSegment(sketch, "E2377", {"start": v(3.46, 3.89) * mm, "end": v(3.46, 3.91) * mm});
            skLineSegment(sketch, "E2378", {"start": v(3.46, 3.91) * mm, "end": v(3.47, 3.94) * mm});
            skLineSegment(sketch, "E2379", {"start": v(3.47, 3.94) * mm, "end": v(3.46, 3.96) * mm});
            skLineSegment(sketch, "E2380", {"start": v(3.46, 3.96) * mm, "end": v(3.38, 4.03) * mm});
            skLineSegment(sketch, "E2381", {"start": v(3.38, 4.03) * mm, "end": v(3.36, 4.03) * mm});
            skLineSegment(sketch, "E2382", {"start": v(3.36, 4.03) * mm, "end": v(3.34, 4.02) * mm});
            skLineSegment(sketch, "E2383", {"start": v(3.34, 4.02) * mm, "end": v(3.31, 4.01) * mm});
            skLineSegment(sketch, "E2384", {"start": v(3.31, 4.01) * mm, "end": v(3.3, 4) * mm});
            skLineSegment(sketch, "E2385", {"start": v(3.3, 4) * mm, "end": v(3.27, 4) * mm});
            skLineSegment(sketch, "E2386", {"start": v(3.27, 4) * mm, "end": v(3.25, 4) * mm});
            skLineSegment(sketch, "E2387", {"start": v(3.25, 4) * mm, "end": v(3.23, 3.98) * mm});
            skLineSegment(sketch, "E2388", {"start": v(3.23, 3.98) * mm, "end": v(3.2, 3.97) * mm});
            skLineSegment(sketch, "E2389", {"start": v(3.2, 3.97) * mm, "end": v(3.19, 3.97) * mm});
            skLineSegment(sketch, "E2390", {"start": v(3.19, 3.97) * mm, "end": v(3.17, 3.96) * mm});
            skLineSegment(sketch, "E2391", {"start": v(3.17, 3.96) * mm, "end": v(3.15, 3.95) * mm});
            skLineSegment(sketch, "E2392", {"start": v(3.15, 3.95) * mm, "end": v(3.13, 3.94) * mm});
            skLineSegment(sketch, "E2393", {"start": v(3.13, 3.94) * mm, "end": v(3.11, 3.93) * mm});
            skLineSegment(sketch, "E2394", {"start": v(3.11, 3.93) * mm, "end": v(3.1, 3.93) * mm});
            skLineSegment(sketch, "E2395", {"start": v(3.1, 3.93) * mm, "end": v(3.08, 3.92) * mm});
            skLineSegment(sketch, "E2396", {"start": v(3.08, 3.92) * mm, "end": v(3.06, 3.9) * mm});
            skLineSegment(sketch, "E2397", {"start": v(3.06, 3.9) * mm, "end": v(3.04, 3.9) * mm});
            skLineSegment(sketch, "E2398", {"start": v(3.04, 3.9) * mm, "end": v(3.02, 3.9) * mm});
            skLineSegment(sketch, "E2399", {"start": v(3.02, 3.9) * mm, "end": v(3, 3.88) * mm});
            skLineSegment(sketch, "E2400", {"start": v(3, 3.88) * mm, "end": v(3, 3.88) * mm});
            skLineSegment(sketch, "E2401", {"start": v(3, 3.88) * mm, "end": v(2.98, 3.87) * mm});
            skLineSegment(sketch, "E2402", {"start": v(2.98, 3.87) * mm, "end": v(2.96, 3.86) * mm});
            skLineSegment(sketch, "E2403", {"start": v(2.96, 3.86) * mm, "end": v(2.95, 3.85) * mm});
            skLineSegment(sketch, "E2404", {"start": v(2.95, 3.85) * mm, "end": v(2.93, 3.84) * mm});
            skLineSegment(sketch, "E2405", {"start": v(2.93, 3.84) * mm, "end": v(2.92, 3.83) * mm});
            skLineSegment(sketch, "E2406", {"start": v(2.92, 3.83) * mm, "end": v(2.9, 3.83) * mm});
            skLineSegment(sketch, "E2407", {"start": v(2.9, 3.83) * mm, "end": v(2.9, 3.82) * mm});
            skLineSegment(sketch, "E2408", {"start": v(2.9, 3.82) * mm, "end": v(2.88, 3.81) * mm});
            skLineSegment(sketch, "E2409", {"start": v(2.88, 3.81) * mm, "end": v(2.87, 3.8) * mm});
            skLineSegment(sketch, "E2410", {"start": v(2.87, 3.8) * mm, "end": v(2.85, 3.8) * mm});
            skLineSegment(sketch, "E2411", {"start": v(2.85, 3.8) * mm, "end": v(2.84, 3.79) * mm});
            skLineSegment(sketch, "E2412", {"start": v(2.84, 3.79) * mm, "end": v(2.84, 3.78) * mm});
            skLineSegment(sketch, "E2413", {"start": v(2.84, 3.78) * mm, "end": v(2.79, 3.81) * mm});
            skLineSegment(sketch, "E2414", {"start": v(2.79, 3.81) * mm, "end": v(2.78, 3.82) * mm});
            skLineSegment(sketch, "E2415", {"start": v(2.78, 3.82) * mm, "end": v(2.73, 3.86) * mm});
            skLineSegment(sketch, "E2416", {"start": v(2.73, 3.86) * mm, "end": v(2.74, 3.86) * mm});
            skLineSegment(sketch, "E2417", {"start": v(2.74, 3.86) * mm, "end": v(2.74, 3.88) * mm});
            skLineSegment(sketch, "E2418", {"start": v(2.74, 3.88) * mm, "end": v(2.74, 3.9) * mm});
            skLineSegment(sketch, "E2419", {"start": v(2.74, 3.9) * mm, "end": v(2.75, 3.9) * mm});
            skLineSegment(sketch, "E2420", {"start": v(2.75, 3.9) * mm, "end": v(2.75, 3.92) * mm});
            skLineSegment(sketch, "E2421", {"start": v(2.75, 3.92) * mm, "end": v(2.75, 3.94) * mm});
            skLineSegment(sketch, "E2422", {"start": v(2.75, 3.94) * mm, "end": v(2.76, 3.95) * mm});
            skLineSegment(sketch, "E2423", {"start": v(2.76, 3.95) * mm, "end": v(2.76, 3.97) * mm});
            skLineSegment(sketch, "E2424", {"start": v(2.76, 3.97) * mm, "end": v(2.76, 3.98) * mm});
            skLineSegment(sketch, "E2425", {"start": v(2.76, 3.98) * mm, "end": v(2.77, 4) * mm});
            skLineSegment(sketch, "E2426", {"start": v(2.77, 4) * mm, "end": v(2.77, 4.02) * mm});
            skLineSegment(sketch, "E2427", {"start": v(2.77, 4.02) * mm, "end": v(2.77, 4.03) * mm});
            skLineSegment(sketch, "E2428", {"start": v(2.77, 4.03) * mm, "end": v(2.78, 4.05) * mm});
            skLineSegment(sketch, "E2429", {"start": v(2.78, 4.05) * mm, "end": v(2.78, 4.07) * mm});
            skLineSegment(sketch, "E2430", {"start": v(2.78, 4.07) * mm, "end": v(2.78, 4.09) * mm});
            skLineSegment(sketch, "E2431", {"start": v(2.78, 4.09) * mm, "end": v(2.79, 4.1) * mm});
            skLineSegment(sketch, "E2432", {"start": v(2.79, 4.1) * mm, "end": v(2.79, 4.13) * mm});
            skLineSegment(sketch, "E2433", {"start": v(2.79, 4.13) * mm, "end": v(2.8, 4.15) * mm});
            skLineSegment(sketch, "E2434", {"start": v(2.8, 4.15) * mm, "end": v(2.8, 4.17) * mm});
            skLineSegment(sketch, "E2435", {"start": v(2.8, 4.17) * mm, "end": v(2.8, 4.19) * mm});
            skLineSegment(sketch, "E2436", {"start": v(2.8, 4.19) * mm, "end": v(2.8, 4.2) * mm});
            skLineSegment(sketch, "E2437", {"start": v(2.8, 4.2) * mm, "end": v(2.8, 4.23) * mm});
            skLineSegment(sketch, "E2438", {"start": v(2.8, 4.23) * mm, "end": v(2.8, 4.25) * mm});
            skLineSegment(sketch, "E2439", {"start": v(2.8, 4.25) * mm, "end": v(2.8, 4.27) * mm});
            skLineSegment(sketch, "E2440", {"start": v(2.8, 4.27) * mm, "end": v(2.8, 4.3) * mm});
            skLineSegment(sketch, "E2441", {"start": v(2.8, 4.3) * mm, "end": v(2.8, 4.31) * mm});
            skLineSegment(sketch, "E2442", {"start": v(2.8, 4.31) * mm, "end": v(2.8, 4.34) * mm});
            skLineSegment(sketch, "E2443", {"start": v(2.8, 4.34) * mm, "end": v(2.8, 4.36) * mm});
            skLineSegment(sketch, "E2444", {"start": v(2.8, 4.36) * mm, "end": v(2.8, 4.38) * mm});
            skLineSegment(sketch, "E2445", {"start": v(2.8, 4.38) * mm, "end": v(2.8, 4.4) * mm});
            skLineSegment(sketch, "E2446", {"start": v(2.8, 4.4) * mm, "end": v(2.8, 4.43) * mm});
            skLineSegment(sketch, "E2447", {"start": v(2.8, 4.43) * mm, "end": v(2.8, 4.45) * mm});
            skLineSegment(sketch, "E2448", {"start": v(2.8, 4.45) * mm, "end": v(2.7, 4.5) * mm});
            skLineSegment(sketch, "E2449", {"start": v(2.7, 4.5) * mm, "end": v(2.69, 4.5) * mm});
            skLineSegment(sketch, "E2450", {"start": v(2.69, 4.5) * mm, "end": v(2.67, 4.5) * mm});
            skLineSegment(sketch, "E2451", {"start": v(2.67, 4.5) * mm, "end": v(2.64, 4.48) * mm});
            skLineSegment(sketch, "E2452", {"start": v(2.64, 4.48) * mm, "end": v(2.62, 4.47) * mm});
            skLineSegment(sketch, "E2453", {"start": v(2.62, 4.47) * mm, "end": v(2.6, 4.46) * mm});
            skLineSegment(sketch, "E2454", {"start": v(2.6, 4.46) * mm, "end": v(2.58, 4.45) * mm});
            skLineSegment(sketch, "E2455", {"start": v(2.58, 4.45) * mm, "end": v(2.56, 4.44) * mm});
            skLineSegment(sketch, "E2456", {"start": v(2.56, 4.44) * mm, "end": v(2.55, 4.43) * mm});
            skLineSegment(sketch, "E2457", {"start": v(2.55, 4.43) * mm, "end": v(2.53, 4.42) * mm});
            skLineSegment(sketch, "E2458", {"start": v(2.53, 4.42) * mm, "end": v(2.5, 4.4) * mm});
            skLineSegment(sketch, "E2459", {"start": v(2.5, 4.4) * mm, "end": v(2.5, 4.4) * mm});
            skLineSegment(sketch, "E2460", {"start": v(2.5, 4.4) * mm, "end": v(2.47, 4.38) * mm});
            skLineSegment(sketch, "E2461", {"start": v(2.47, 4.38) * mm, "end": v(2.46, 4.37) * mm});
            skLineSegment(sketch, "E2462", {"start": v(2.46, 4.37) * mm, "end": v(2.44, 4.36) * mm});
            skLineSegment(sketch, "E2463", {"start": v(2.44, 4.36) * mm, "end": v(2.42, 4.35) * mm});
            skLineSegment(sketch, "E2464", {"start": v(2.42, 4.35) * mm, "end": v(2.4, 4.34) * mm});
            skLineSegment(sketch, "E2465", {"start": v(2.4, 4.34) * mm, "end": v(2.4, 4.33) * mm});
            skLineSegment(sketch, "E2466", {"start": v(2.4, 4.33) * mm, "end": v(2.38, 4.32) * mm});
            skLineSegment(sketch, "E2467", {"start": v(2.38, 4.32) * mm, "end": v(2.36, 4.3) * mm});
            skLineSegment(sketch, "E2468", {"start": v(2.36, 4.3) * mm, "end": v(2.35, 4.3) * mm});
            skLineSegment(sketch, "E2469", {"start": v(2.35, 4.3) * mm, "end": v(2.33, 4.29) * mm});
            skLineSegment(sketch, "E2470", {"start": v(2.33, 4.29) * mm, "end": v(2.32, 4.27) * mm});
            skLineSegment(sketch, "E2471", {"start": v(2.32, 4.27) * mm, "end": v(2.3, 4.26) * mm});
            skLineSegment(sketch, "E2472", {"start": v(2.3, 4.26) * mm, "end": v(2.3, 4.25) * mm});
            skLineSegment(sketch, "E2473", {"start": v(2.3, 4.25) * mm, "end": v(2.28, 4.24) * mm});
            skLineSegment(sketch, "E2474", {"start": v(2.28, 4.24) * mm, "end": v(2.27, 4.23) * mm});
            skLineSegment(sketch, "E2475", {"start": v(2.27, 4.23) * mm, "end": v(2.26, 4.22) * mm});
            skLineSegment(sketch, "E2476", {"start": v(2.26, 4.22) * mm, "end": v(2.25, 4.21) * mm});
            skLineSegment(sketch, "E2477", {"start": v(2.25, 4.21) * mm, "end": v(2.24, 4.2) * mm});
            skLineSegment(sketch, "E2478", {"start": v(2.24, 4.2) * mm, "end": v(2.22, 4.2) * mm});
            skLineSegment(sketch, "E2479", {"start": v(2.22, 4.2) * mm, "end": v(2.21, 4.18) * mm});
            skLineSegment(sketch, "E2480", {"start": v(2.21, 4.18) * mm, "end": v(2.2, 4.18) * mm});
            skLineSegment(sketch, "E2481", {"start": v(2.2, 4.18) * mm, "end": v(2.16, 4.2) * mm});
            skLineSegment(sketch, "E2482", {"start": v(2.16, 4.2) * mm, "end": v(2.14, 4.2) * mm});
            skLineSegment(sketch, "E2483", {"start": v(2.14, 4.2) * mm, "end": v(2.1, 4.24) * mm});
            skLineSegment(sketch, "E2484", {"start": v(2.1, 4.24) * mm, "end": v(2.1, 4.24) * mm});
            skLineSegment(sketch, "E2485", {"start": v(2.1, 4.24) * mm, "end": v(2.1, 4.26) * mm});
            skLineSegment(sketch, "E2486", {"start": v(2.1, 4.26) * mm, "end": v(2.1, 4.27) * mm});
            skLineSegment(sketch, "E2487", {"start": v(2.1, 4.27) * mm, "end": v(2.1, 4.29) * mm});
            skLineSegment(sketch, "E2488", {"start": v(2.1, 4.29) * mm, "end": v(2.1, 4.3) * mm});
            skLineSegment(sketch, "E2489", {"start": v(2.1, 4.3) * mm, "end": v(2.1, 4.32) * mm});
            skLineSegment(sketch, "E2490", {"start": v(2.1, 4.32) * mm, "end": v(2.1, 4.33) * mm});
            skLineSegment(sketch, "E2491", {"start": v(2.1, 4.33) * mm, "end": v(2.1, 4.35) * mm});
            skLineSegment(sketch, "E2492", {"start": v(2.1, 4.35) * mm, "end": v(2.1, 4.37) * mm});
            skLineSegment(sketch, "E2493", {"start": v(2.1, 4.37) * mm, "end": v(2.1, 4.38) * mm});
            skLineSegment(sketch, "E2494", {"start": v(2.1, 4.38) * mm, "end": v(2.1, 4.4) * mm});
            skLineSegment(sketch, "E2495", {"start": v(2.1, 4.4) * mm, "end": v(2.1, 4.42) * mm});
            skLineSegment(sketch, "E2496", {"start": v(2.1, 4.42) * mm, "end": v(2.1, 4.44) * mm});
            skLineSegment(sketch, "E2497", {"start": v(2.1, 4.44) * mm, "end": v(2.1, 4.46) * mm});
            skLineSegment(sketch, "E2498", {"start": v(2.1, 4.46) * mm, "end": v(2.1, 4.47) * mm});
            skLineSegment(sketch, "E2499", {"start": v(2.1, 4.47) * mm, "end": v(2.1, 4.5) * mm});
            skLineSegment(sketch, "E2500", {"start": v(2.1, 4.5) * mm, "end": v(2.1, 4.51) * mm});
            skLineSegment(sketch, "E2501", {"start": v(2.1, 4.51) * mm, "end": v(2.1, 4.53) * mm});
            skLineSegment(sketch, "E2502", {"start": v(2.1, 4.53) * mm, "end": v(2.1, 4.55) * mm});
            skLineSegment(sketch, "E2503", {"start": v(2.1, 4.55) * mm, "end": v(2.1, 4.57) * mm});
            skLineSegment(sketch, "E2504", {"start": v(2.1, 4.57) * mm, "end": v(2.1, 4.6) * mm});
            skLineSegment(sketch, "E2505", {"start": v(2.1, 4.6) * mm, "end": v(2.1, 4.61) * mm});
            skLineSegment(sketch, "E2506", {"start": v(2.1, 4.61) * mm, "end": v(2.1, 4.63) * mm});
            skLineSegment(sketch, "E2507", {"start": v(2.1, 4.63) * mm, "end": v(2.1, 4.66) * mm});
            skLineSegment(sketch, "E2508", {"start": v(2.1, 4.66) * mm, "end": v(2.1, 4.68) * mm});
            skLineSegment(sketch, "E2509", {"start": v(2.1, 4.68) * mm, "end": v(2.1, 4.7) * mm});
            skLineSegment(sketch, "E2510", {"start": v(2.1, 4.7) * mm, "end": v(2.1, 4.72) * mm});
            skLineSegment(sketch, "E2511", {"start": v(2.1, 4.72) * mm, "end": v(2.1, 4.75) * mm});
            skLineSegment(sketch, "E2512", {"start": v(2.1, 4.75) * mm, "end": v(2.09, 4.77) * mm});
            skLineSegment(sketch, "E2513", {"start": v(2.09, 4.77) * mm, "end": v(2.08, 4.8) * mm});
            skLineSegment(sketch, "E2514", {"start": v(2.08, 4.8) * mm, "end": v(2.08, 4.82) * mm});
            skLineSegment(sketch, "E2515", {"start": v(2.08, 4.82) * mm, "end": v(2.07, 4.84) * mm});
            skLineSegment(sketch, "E2516", {"start": v(2.07, 4.84) * mm, "end": v(1.97, 4.88) * mm});
            skLineSegment(sketch, "E2517", {"start": v(1.97, 4.88) * mm, "end": v(1.95, 4.87) * mm});
            skLineSegment(sketch, "E2518", {"start": v(1.95, 4.87) * mm, "end": v(1.93, 4.86) * mm});
            skLineSegment(sketch, "E2519", {"start": v(1.93, 4.86) * mm, "end": v(1.91, 4.84) * mm});
            skLineSegment(sketch, "E2520", {"start": v(1.91, 4.84) * mm, "end": v(1.9, 4.83) * mm});
            skLineSegment(sketch, "E2521", {"start": v(1.9, 4.83) * mm, "end": v(1.87, 4.81) * mm});
            skLineSegment(sketch, "E2522", {"start": v(1.87, 4.81) * mm, "end": v(1.86, 4.8) * mm});
            skLineSegment(sketch, "E2523", {"start": v(1.86, 4.8) * mm, "end": v(1.84, 4.79) * mm});
            skLineSegment(sketch, "E2524", {"start": v(1.84, 4.79) * mm, "end": v(1.82, 4.77) * mm});
            skLineSegment(sketch, "E2525", {"start": v(1.82, 4.77) * mm, "end": v(1.8, 4.76) * mm});
            skLineSegment(sketch, "E2526", {"start": v(1.8, 4.76) * mm, "end": v(1.79, 4.74) * mm});
            skLineSegment(sketch, "E2527", {"start": v(1.79, 4.74) * mm, "end": v(1.77, 4.73) * mm});
            skLineSegment(sketch, "E2528", {"start": v(1.77, 4.73) * mm, "end": v(1.76, 4.72) * mm});
            skLineSegment(sketch, "E2529", {"start": v(1.76, 4.72) * mm, "end": v(1.74, 4.7) * mm});
            skLineSegment(sketch, "E2530", {"start": v(1.74, 4.7) * mm, "end": v(1.73, 4.69) * mm});
            skLineSegment(sketch, "E2531", {"start": v(1.73, 4.69) * mm, "end": v(1.71, 4.68) * mm});
            skLineSegment(sketch, "E2532", {"start": v(1.71, 4.68) * mm, "end": v(1.7, 4.66) * mm});
            skLineSegment(sketch, "E2533", {"start": v(1.7, 4.66) * mm, "end": v(1.69, 4.65) * mm});
            skLineSegment(sketch, "E2534", {"start": v(1.69, 4.65) * mm, "end": v(1.67, 4.64) * mm});
            skLineSegment(sketch, "E2535", {"start": v(1.67, 4.64) * mm, "end": v(1.66, 4.62) * mm});
            skLineSegment(sketch, "E2536", {"start": v(1.66, 4.62) * mm, "end": v(1.65, 4.61) * mm});
            skLineSegment(sketch, "E2537", {"start": v(1.65, 4.61) * mm, "end": v(1.64, 4.6) * mm});
            skLineSegment(sketch, "E2538", {"start": v(1.64, 4.6) * mm, "end": v(1.62, 4.59) * mm});
            skLineSegment(sketch, "E2539", {"start": v(1.62, 4.59) * mm, "end": v(1.61, 4.57) * mm});
            skLineSegment(sketch, "E2540", {"start": v(1.61, 4.57) * mm, "end": v(1.6, 4.56) * mm});
            skLineSegment(sketch, "E2541", {"start": v(1.6, 4.56) * mm, "end": v(1.6, 4.55) * mm});
            skLineSegment(sketch, "E2542", {"start": v(1.6, 4.55) * mm, "end": v(1.58, 4.54) * mm});
            skLineSegment(sketch, "E2543", {"start": v(1.58, 4.54) * mm, "end": v(1.57, 4.53) * mm});
            skLineSegment(sketch, "E2544", {"start": v(1.57, 4.53) * mm, "end": v(1.56, 4.51) * mm});
            skLineSegment(sketch, "E2545", {"start": v(1.56, 4.51) * mm, "end": v(1.55, 4.5) * mm});
            skLineSegment(sketch, "E2546", {"start": v(1.55, 4.5) * mm, "end": v(1.54, 4.5) * mm});
            skLineSegment(sketch, "E2547", {"start": v(1.54, 4.5) * mm, "end": v(1.53, 4.48) * mm});
            skLineSegment(sketch, "E2548", {"start": v(1.53, 4.48) * mm, "end": v(1.53, 4.47) * mm});
            skLineSegment(sketch, "E2549", {"start": v(1.53, 4.47) * mm, "end": v(1.47, 4.49) * mm});
            skLineSegment(sketch, "E2550", {"start": v(1.47, 4.49) * mm, "end": v(1.46, 4.5) * mm});
            skLineSegment(sketch, "E2551", {"start": v(1.46, 4.5) * mm, "end": v(1.4, 4.51) * mm});
            skLineSegment(sketch, "E2552", {"start": v(1.4, 4.51) * mm, "end": v(1.4, 4.52) * mm});
            skLineSegment(sketch, "E2553", {"start": v(1.4, 4.52) * mm, "end": v(1.4, 4.53) * mm});
            skLineSegment(sketch, "E2554", {"start": v(1.4, 4.53) * mm, "end": v(1.4, 4.55) * mm});
            skLineSegment(sketch, "E2555", {"start": v(1.4, 4.55) * mm, "end": v(1.4, 4.56) * mm});
            skLineSegment(sketch, "E2556", {"start": v(1.4, 4.56) * mm, "end": v(1.4, 4.58) * mm});
            skLineSegment(sketch, "E2557", {"start": v(1.4, 4.58) * mm, "end": v(1.4, 4.6) * mm});
            skLineSegment(sketch, "E2558", {"start": v(1.4, 4.6) * mm, "end": v(1.4, 4.61) * mm});
            skLineSegment(sketch, "E2559", {"start": v(1.4, 4.61) * mm, "end": v(1.4, 4.63) * mm});
            skLineSegment(sketch, "E2560", {"start": v(1.4, 4.63) * mm, "end": v(1.4, 4.64) * mm});
            skLineSegment(sketch, "E2561", {"start": v(1.4, 4.64) * mm, "end": v(1.4, 4.66) * mm});
            skLineSegment(sketch, "E2562", {"start": v(1.4, 4.66) * mm, "end": v(1.4, 4.68) * mm});
            skLineSegment(sketch, "E2563", {"start": v(1.4, 4.68) * mm, "end": v(1.4, 4.7) * mm});
            skLineSegment(sketch, "E2564", {"start": v(1.4, 4.7) * mm, "end": v(1.39, 4.71) * mm});
            skLineSegment(sketch, "E2565", {"start": v(1.39, 4.71) * mm, "end": v(1.39, 4.73) * mm});
            skLineSegment(sketch, "E2566", {"start": v(1.39, 4.73) * mm, "end": v(1.38, 4.75) * mm});
            skLineSegment(sketch, "E2567", {"start": v(1.38, 4.75) * mm, "end": v(1.38, 4.77) * mm});
            skLineSegment(sketch, "E2568", {"start": v(1.38, 4.77) * mm, "end": v(1.38, 4.79) * mm});
            skLineSegment(sketch, "E2569", {"start": v(1.38, 4.79) * mm, "end": v(1.37, 4.8) * mm});
            skLineSegment(sketch, "E2570", {"start": v(1.37, 4.8) * mm, "end": v(1.37, 4.82) * mm});
            skLineSegment(sketch, "E2571", {"start": v(1.37, 4.82) * mm, "end": v(1.36, 4.84) * mm});
            skLineSegment(sketch, "E2572", {"start": v(1.36, 4.84) * mm, "end": v(1.36, 4.86) * mm});
            skLineSegment(sketch, "E2573", {"start": v(1.36, 4.86) * mm, "end": v(1.36, 4.89) * mm});
            skLineSegment(sketch, "E2574", {"start": v(1.36, 4.89) * mm, "end": v(1.35, 4.9) * mm});
            skLineSegment(sketch, "E2575", {"start": v(1.35, 4.9) * mm, "end": v(1.35, 4.93) * mm});
            skLineSegment(sketch, "E2576", {"start": v(1.35, 4.93) * mm, "end": v(1.34, 4.95) * mm});
            skLineSegment(sketch, "E2577", {"start": v(1.34, 4.95) * mm, "end": v(1.33, 4.97) * mm});
            skLineSegment(sketch, "E2578", {"start": v(1.33, 4.97) * mm, "end": v(1.33, 5) * mm});
            skLineSegment(sketch, "E2579", {"start": v(1.33, 5) * mm, "end": v(1.32, 5.01) * mm});
            skLineSegment(sketch, "E2580", {"start": v(1.32, 5.01) * mm, "end": v(1.32, 5.04) * mm});
            skLineSegment(sketch, "E2581", {"start": v(1.32, 5.04) * mm, "end": v(1.3, 5.06) * mm});
            skLineSegment(sketch, "E2582", {"start": v(1.3, 5.06) * mm, "end": v(1.3, 5.08) * mm});
            skLineSegment(sketch, "E2583", {"start": v(1.3, 5.08) * mm, "end": v(1.29, 5.1) * mm});
            skLineSegment(sketch, "E2584", {"start": v(1.29, 5.1) * mm, "end": v(1.18, 5.12) * mm});
            skLineSegment(sketch, "E2585", {"start": v(1.18, 5.12) * mm, "end": v(1.16, 5.12) * mm});
            skLineSegment(sketch, "E2586", {"start": v(1.16, 5.12) * mm, "end": v(1.15, 5.1) * mm});
            skLineSegment(sketch, "E2587", {"start": v(1.15, 5.1) * mm, "end": v(1.13, 5.08) * mm});
            skLineSegment(sketch, "E2588", {"start": v(1.13, 5.08) * mm, "end": v(1.11, 5.06) * mm});
            skLineSegment(sketch, "E2589", {"start": v(1.11, 5.06) * mm, "end": v(1.1, 5.05) * mm});
            skLineSegment(sketch, "E2590", {"start": v(1.1, 5.05) * mm, "end": v(1.08, 5.03) * mm});
            skLineSegment(sketch, "E2591", {"start": v(1.08, 5.03) * mm, "end": v(1.07, 5.01) * mm});
            skLineSegment(sketch, "E2592", {"start": v(1.07, 5.01) * mm, "end": v(1.05, 5) * mm});
            skLineSegment(sketch, "E2593", {"start": v(1.05, 5) * mm, "end": v(1.04, 4.98) * mm});
            skLineSegment(sketch, "E2594", {"start": v(1.04, 4.98) * mm, "end": v(1.03, 4.97) * mm});
            skLineSegment(sketch, "E2595", {"start": v(1.03, 4.97) * mm, "end": v(1.01, 4.95) * mm});
            skLineSegment(sketch, "E2596", {"start": v(1.01, 4.95) * mm, "end": v(1, 4.93) * mm});
            skLineSegment(sketch, "E2597", {"start": v(1, 4.93) * mm, "end": v(0.99, 4.92) * mm});
            skLineSegment(sketch, "E2598", {"start": v(0.99, 4.92) * mm, "end": v(0.97, 4.9) * mm});
            skLineSegment(sketch, "E2599", {"start": v(0.97, 4.9) * mm, "end": v(0.96, 4.89) * mm});
            skLineSegment(sketch, "E2600", {"start": v(0.96, 4.89) * mm, "end": v(0.95, 4.87) * mm});
            skLineSegment(sketch, "E2601", {"start": v(0.95, 4.87) * mm, "end": v(0.94, 4.86) * mm});
            skLineSegment(sketch, "E2602", {"start": v(0.94, 4.86) * mm, "end": v(0.93, 4.84) * mm});
            skLineSegment(sketch, "E2603", {"start": v(0.93, 4.84) * mm, "end": v(0.92, 4.83) * mm});
            skLineSegment(sketch, "E2604", {"start": v(0.92, 4.83) * mm, "end": v(0.9, 4.81) * mm});
            skLineSegment(sketch, "E2605", {"start": v(0.9, 4.81) * mm, "end": v(0.9, 4.8) * mm});
            skLineSegment(sketch, "E2606", {"start": v(0.9, 4.8) * mm, "end": v(0.89, 4.78) * mm});
            skLineSegment(sketch, "E2607", {"start": v(0.89, 4.78) * mm, "end": v(0.88, 4.77) * mm});
            skLineSegment(sketch, "E2608", {"start": v(0.88, 4.77) * mm, "end": v(0.87, 4.76) * mm});
            skLineSegment(sketch, "E2609", {"start": v(0.87, 4.76) * mm, "end": v(0.86, 4.74) * mm});
            skLineSegment(sketch, "E2610", {"start": v(0.86, 4.74) * mm, "end": v(0.85, 4.73) * mm});
            skLineSegment(sketch, "E2611", {"start": v(0.85, 4.73) * mm, "end": v(0.84, 4.72) * mm});
            skLineSegment(sketch, "E2612", {"start": v(0.84, 4.72) * mm, "end": v(0.83, 4.7) * mm});
            skLineSegment(sketch, "E2613", {"start": v(0.83, 4.7) * mm, "end": v(0.83, 4.69) * mm});
            skLineSegment(sketch, "E2614", {"start": v(0.83, 4.69) * mm, "end": v(0.82, 4.68) * mm});
            skLineSegment(sketch, "E2615", {"start": v(0.82, 4.68) * mm, "end": v(0.81, 4.66) * mm});
            skLineSegment(sketch, "E2616", {"start": v(0.81, 4.66) * mm, "end": v(0.8, 4.66) * mm});
            skLineSegment(sketch, "E2617", {"start": v(0.8, 4.66) * mm, "end": v(0.75, 4.66) * mm});
            skLineSegment(sketch, "E2618", {"start": v(0.75, 4.66) * mm, "end": v(0.74, 4.66) * mm});
            skLineSegment(sketch, "E2619", {"start": v(0.74, 4.66) * mm, "end": v(0.68, 4.68) * mm});
            skLineSegment(sketch, "E2620", {"start": v(0.68, 4.68) * mm, "end": v(0.68, 4.69) * mm});
            skLineSegment(sketch, "E2621", {"start": v(0.68, 4.69) * mm, "end": v(0.68, 4.7) * mm});
            skLineSegment(sketch, "E2622", {"start": v(0.68, 4.7) * mm, "end": v(0.68, 4.71) * mm});
            skLineSegment(sketch, "E2623", {"start": v(0.68, 4.71) * mm, "end": v(0.67, 4.73) * mm});
            skLineSegment(sketch, "E2624", {"start": v(0.67, 4.73) * mm, "end": v(0.67, 4.74) * mm});
            skLineSegment(sketch, "E2625", {"start": v(0.67, 4.74) * mm, "end": v(0.67, 4.76) * mm});
            skLineSegment(sketch, "E2626", {"start": v(0.67, 4.76) * mm, "end": v(0.66, 4.77) * mm});
            skLineSegment(sketch, "E2627", {"start": v(0.66, 4.77) * mm, "end": v(0.66, 4.79) * mm});
            skLineSegment(sketch, "E2628", {"start": v(0.66, 4.79) * mm, "end": v(0.65, 4.8) * mm});
            skLineSegment(sketch, "E2629", {"start": v(0.65, 4.8) * mm, "end": v(0.65, 4.82) * mm});
            skLineSegment(sketch, "E2630", {"start": v(0.65, 4.82) * mm, "end": v(0.64, 4.84) * mm});
            skLineSegment(sketch, "E2631", {"start": v(0.64, 4.84) * mm, "end": v(0.64, 4.85) * mm});
            skLineSegment(sketch, "E2632", {"start": v(0.64, 4.85) * mm, "end": v(0.63, 4.87) * mm});
            skLineSegment(sketch, "E2633", {"start": v(0.63, 4.87) * mm, "end": v(0.63, 4.89) * mm});
            skLineSegment(sketch, "E2634", {"start": v(0.63, 4.89) * mm, "end": v(0.62, 4.9) * mm});
            skLineSegment(sketch, "E2635", {"start": v(0.62, 4.9) * mm, "end": v(0.62, 4.92) * mm});
            skLineSegment(sketch, "E2636", {"start": v(0.62, 4.92) * mm, "end": v(0.61, 4.94) * mm});
            skLineSegment(sketch, "E2637", {"start": v(0.61, 4.94) * mm, "end": v(0.6, 4.96) * mm});
            skLineSegment(sketch, "E2638", {"start": v(0.6, 4.96) * mm, "end": v(0.6, 4.98) * mm});
            skLineSegment(sketch, "E2639", {"start": v(0.6, 4.98) * mm, "end": v(0.59, 5) * mm});
            skLineSegment(sketch, "E2640", {"start": v(0.59, 5) * mm, "end": v(0.58, 5.02) * mm});
            skLineSegment(sketch, "E2641", {"start": v(0.58, 5.02) * mm, "end": v(0.57, 5.04) * mm});
            skLineSegment(sketch, "E2642", {"start": v(0.57, 5.04) * mm, "end": v(0.57, 5.06) * mm});
            skLineSegment(sketch, "E2643", {"start": v(0.57, 5.06) * mm, "end": v(0.56, 5.08) * mm});
            skLineSegment(sketch, "E2644", {"start": v(0.56, 5.08) * mm, "end": v(0.55, 5.1) * mm});
            skLineSegment(sketch, "E2645", {"start": v(0.55, 5.1) * mm, "end": v(0.54, 5.12) * mm});
            skLineSegment(sketch, "E2646", {"start": v(0.54, 5.12) * mm, "end": v(0.53, 5.14) * mm});
            skLineSegment(sketch, "E2647", {"start": v(0.53, 5.14) * mm, "end": v(0.52, 5.16) * mm});
            skLineSegment(sketch, "E2648", {"start": v(0.52, 5.16) * mm, "end": v(0.51, 5.18) * mm});
            skLineSegment(sketch, "E2649", {"start": v(0.51, 5.18) * mm, "end": v(0.5, 5.2) * mm});
            skLineSegment(sketch, "E2650", {"start": v(0.5, 5.2) * mm, "end": v(0.49, 5.22) * mm});
            skLineSegment(sketch, "E2651", {"start": v(0.49, 5.22) * mm, "end": v(0.47, 5.24) * mm});
            skLineSegment(sketch, "E2652", {"start": v(0.47, 5.24) * mm, "end": v(0.37, 5.25) * mm});
            skLineSegment(sketch, "E2653", {"start": v(0.37, 5.25) * mm, "end": v(0.35, 5.24) * mm});
            skLineSegment(sketch, "E2654", {"start": v(0.35, 5.24) * mm, "end": v(0.33, 5.21) * mm});
            skLineSegment(sketch, "E2655", {"start": v(0.33, 5.21) * mm, "end": v(0.32, 5.2) * mm});
            skLineSegment(sketch, "E2656", {"start": v(0.32, 5.2) * mm, "end": v(0.3, 5.18) * mm});
            skLineSegment(sketch, "E2657", {"start": v(0.3, 5.18) * mm, "end": v(0.3, 5.16) * mm});
            skLineSegment(sketch, "E2658", {"start": v(0.3, 5.16) * mm, "end": v(0.28, 5.14) * mm});
            skLineSegment(sketch, "E2659", {"start": v(0.28, 5.14) * mm, "end": v(0.27, 5.12) * mm});
            skLineSegment(sketch, "E2660", {"start": v(0.27, 5.12) * mm, "end": v(0.26, 5.1) * mm});
            skLineSegment(sketch, "E2661", {"start": v(0.26, 5.1) * mm, "end": v(0.25, 5.08) * mm});
            skLineSegment(sketch, "E2662", {"start": v(0.25, 5.08) * mm, "end": v(0.24, 5.06) * mm});
            skLineSegment(sketch, "E2663", {"start": v(0.24, 5.06) * mm, "end": v(0.23, 5.05) * mm});
            skLineSegment(sketch, "E2664", {"start": v(0.23, 5.05) * mm, "end": v(0.21, 5.03) * mm});
            skLineSegment(sketch, "E2665", {"start": v(0.21, 5.03) * mm, "end": v(0.2, 5.01) * mm});
            skLineSegment(sketch, "E2666", {"start": v(0.2, 5.01) * mm, "end": v(0.2, 5) * mm});
            skLineSegment(sketch, "E2667", {"start": v(0.2, 5) * mm, "end": v(0.19, 4.98) * mm});
            skLineSegment(sketch, "E2668", {"start": v(0.19, 4.98) * mm, "end": v(0.18, 4.96) * mm});
            skLineSegment(sketch, "E2669", {"start": v(0.18, 4.96) * mm, "end": v(0.17, 4.94) * mm});
            skLineSegment(sketch, "E2670", {"start": v(0.17, 4.94) * mm, "end": v(0.16, 4.93) * mm});
            skLineSegment(sketch, "E2671", {"start": v(0.16, 4.93) * mm, "end": v(0.15, 4.91) * mm});
            skLineSegment(sketch, "E2672", {"start": v(0.15, 4.91) * mm, "end": v(0.14, 4.9) * mm});
            skLineSegment(sketch, "E2673", {"start": v(0.14, 4.9) * mm, "end": v(0.13, 4.88) * mm});
            skLineSegment(sketch, "E2674", {"start": v(0.13, 4.88) * mm, "end": v(0.13, 4.86) * mm});
            skLineSegment(sketch, "E2675", {"start": v(0.13, 4.86) * mm, "end": v(0.12, 4.85) * mm});
            skLineSegment(sketch, "E2676", {"start": v(0.12, 4.85) * mm, "end": v(0.11, 4.83) * mm});
            skLineSegment(sketch, "E2677", {"start": v(0.11, 4.83) * mm, "end": v(0.1, 4.82) * mm});
            skLineSegment(sketch, "E2678", {"start": v(0.1, 4.82) * mm, "end": v(0.1, 4.8) * mm});
            skLineSegment(sketch, "E2679", {"start": v(0.1, 4.8) * mm, "end": v(0.1, 4.79) * mm});
            skLineSegment(sketch, "E2680", {"start": v(0.1, 4.79) * mm, "end": v(0.09, 4.77) * mm});
            skLineSegment(sketch, "E2681", {"start": v(0.09, 4.77) * mm, "end": v(0.08, 4.76) * mm});
            skLineSegment(sketch, "E2682", {"start": v(0.08, 4.76) * mm, "end": v(0.08, 4.75) * mm});
            skLineSegment(sketch, "E2683", {"start": v(0.08, 4.75) * mm, "end": v(0.07, 4.73) * mm});
            skLineSegment(sketch, "E2684", {"start": v(0.07, 4.73) * mm, "end": v(0.07, 4.73) * mm});
            skLineSegment(sketch, "E2685", {"start": v(0.07, 4.73) * mm, "end": v(0.01, 4.72) * mm});
            skLineSegment(sketch, "E2686", {"start": v(0.01, 4.72) * mm, "end": v(0, 4.72) * mm});
            skLineSegment(sketch, "E2687", {"start": v(0, 4.72) * mm, "end": v(-0.06, 4.73) * mm});
            skLineSegment(sketch, "E2688", {"start": v(-0.06, 4.73) * mm, "end": v(-0.06, 4.73) * mm});
            skLineSegment(sketch, "E2689", {"start": v(-0.06, 4.73) * mm, "end": v(-0.06, 4.75) * mm});
            skLineSegment(sketch, "E2690", {"start": v(-0.06, 4.75) * mm, "end": v(-0.07, 4.76) * mm});
            skLineSegment(sketch, "E2691", {"start": v(-0.07, 4.76) * mm, "end": v(-0.07, 4.78) * mm});
            skLineSegment(sketch, "E2692", {"start": v(-0.07, 4.78) * mm, "end": v(-0.08, 4.79) * mm});
            skLineSegment(sketch, "E2693", {"start": v(-0.08, 4.79) * mm, "end": v(-0.09, 4.8) * mm});
            skLineSegment(sketch, "E2694", {"start": v(-0.09, 4.8) * mm, "end": v(-0.1, 4.82) * mm});
            skLineSegment(sketch, "E2695", {"start": v(-0.1, 4.82) * mm, "end": v(-0.1, 4.83) * mm});
            skLineSegment(sketch, "E2696", {"start": v(-0.1, 4.83) * mm, "end": v(-0.1, 4.85) * mm});
            skLineSegment(sketch, "E2697", {"start": v(-0.1, 4.85) * mm, "end": v(-0.11, 4.86) * mm});
            skLineSegment(sketch, "E2698", {"start": v(-0.11, 4.86) * mm, "end": v(-0.12, 4.88) * mm});
            skLineSegment(sketch, "E2699", {"start": v(-0.12, 4.88) * mm, "end": v(-0.13, 4.9) * mm});
            skLineSegment(sketch, "E2700", {"start": v(-0.13, 4.9) * mm, "end": v(-0.14, 4.91) * mm});
            skLineSegment(sketch, "E2701", {"start": v(-0.14, 4.91) * mm, "end": v(-0.14, 4.93) * mm});
            skLineSegment(sketch, "E2702", {"start": v(-0.14, 4.93) * mm, "end": v(-0.15, 4.94) * mm});
            skLineSegment(sketch, "E2703", {"start": v(-0.15, 4.94) * mm, "end": v(-0.16, 4.96) * mm});
            skLineSegment(sketch, "E2704", {"start": v(-0.16, 4.96) * mm, "end": v(-0.17, 4.98) * mm});
            skLineSegment(sketch, "E2705", {"start": v(-0.17, 4.98) * mm, "end": v(-0.18, 5) * mm});
            skLineSegment(sketch, "E2706", {"start": v(-0.18, 5) * mm, "end": v(-0.19, 5.01) * mm});
            skLineSegment(sketch, "E2707", {"start": v(-0.19, 5.01) * mm, "end": v(-0.2, 5.03) * mm});
            skLineSegment(sketch, "E2708", {"start": v(-0.2, 5.03) * mm, "end": v(-0.2, 5.05) * mm});
            skLineSegment(sketch, "E2709", {"start": v(-0.2, 5.05) * mm, "end": v(-0.22, 5.07) * mm});
            skLineSegment(sketch, "E2710", {"start": v(-0.22, 5.07) * mm, "end": v(-0.23, 5.08) * mm});
            skLineSegment(sketch, "E2711", {"start": v(-0.23, 5.08) * mm, "end": v(-0.24, 5.1) * mm});
            skLineSegment(sketch, "E2712", {"start": v(-0.24, 5.1) * mm, "end": v(-0.25, 5.12) * mm});
            skLineSegment(sketch, "E2713", {"start": v(-0.25, 5.12) * mm, "end": v(-0.27, 5.14) * mm});
            skLineSegment(sketch, "E2714", {"start": v(-0.27, 5.14) * mm, "end": v(-0.28, 5.16) * mm});
            skLineSegment(sketch, "E2715", {"start": v(-0.28, 5.16) * mm, "end": v(-0.3, 5.18) * mm});
            skLineSegment(sketch, "E2716", {"start": v(-0.3, 5.18) * mm, "end": v(-0.3, 5.2) * mm});
            skLineSegment(sketch, "E2717", {"start": v(-0.3, 5.2) * mm, "end": v(-0.32, 5.22) * mm});
            skLineSegment(sketch, "E2718", {"start": v(-0.32, 5.22) * mm, "end": v(-0.33, 5.24) * mm});
            skLineSegment(sketch, "E2719", {"start": v(-0.33, 5.24) * mm, "end": v(-0.35, 5.25) * mm});
            skLineSegment(sketch, "E2720", {"start": v(0.2, 0) * mm, "end": v(-0.2, 0) * mm});
            skLineSegment(sketch, "E2721", {"start": v(0, -0.2) * mm, "end": v(0, 0.2) * mm});
            skSolve(sketch);
        }
        {
            var Q0;
            Q0=qCreatedBy(makeId("Top.planeOp"),FACE);
            var sketch = newSketch(context, id + "F1", { "sketchPlane" : qUnion([Q0])});
            skCircle(sketch, "E2722", {"center": v(0, 0) * mm, "radius": 1.55 * mm});
            skSolve(sketch);
        }
        {
            var Q0;
            Q0=makeQuery(id+"F0.imprint","IMPRINT",FACE,{"disambiguationData":[TD([[makeQuery(id+"F0.imprint","IMPRINT",EDGE,{"derivedFrom":sQuery(id+"F0.wireOp",EDGE,"E0")}),1.0]])]});
            extrude(context, id + "F2", {"entities" : qUnion([Q0]), "depth" : 10 * mm});
        }
        {
            var Q0;
            Q0 = qSketchRegion(id + "F1", true);
            extrude(context, id + "F3", {"entities" : qUnion([Q0]), "operationType" : NewBodyOperationType.REMOVE, "depth" : 25 * mm});
        }
    });
